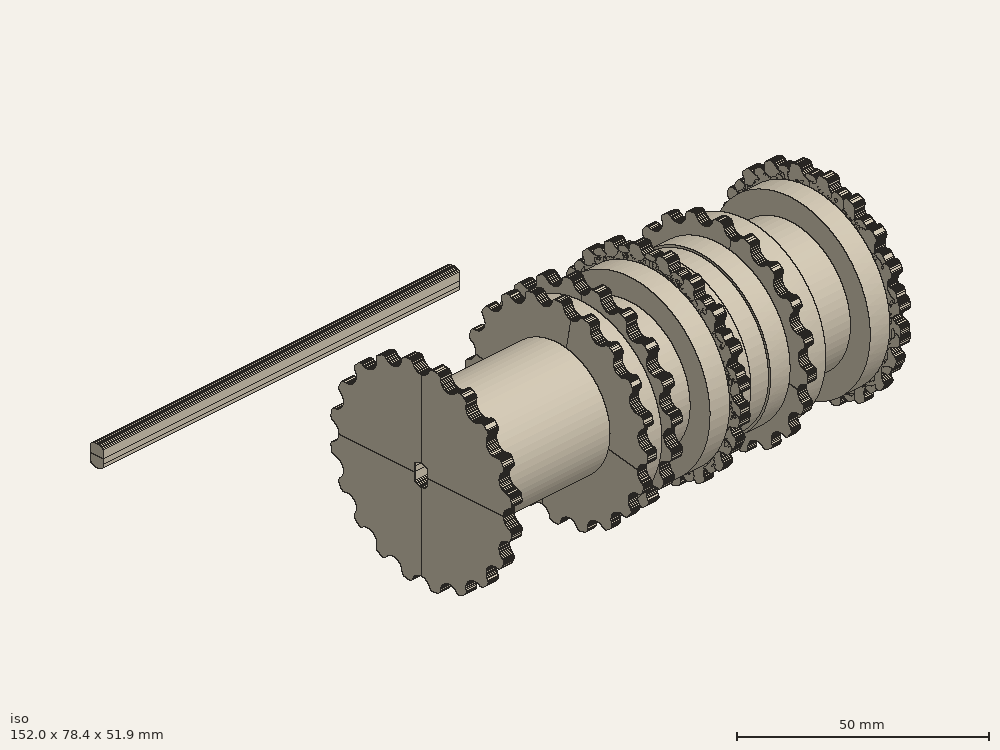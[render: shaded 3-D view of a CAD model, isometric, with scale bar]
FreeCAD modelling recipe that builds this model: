
FCSTD DOCUMENT  (FreeCAD 0.18R4 (GitTag))
Label: ведущий каток
License: All rights reserved
LicenseURL: http://en.wikipedia.org/wiki/All_rights_reserved
objects: Sketcher::SketchObject×33, PartDesign::Pad×23, PartDesign::PolarPattern×19, PartDesign::Body×15, Part::Cut×10, Part::Cylinder×8, Part::MultiFuse×6, App::MeasureDistance×4, PartDesign::Pocket×4, Mesh::Feature×3
note: 145 computed .brp shape members not serialized (recipe doc carries the construction recipe); baked Part::Feature solids carry a one-line shape summary decoded from their .brp

FEATURE [Mesh::Feature] vedushhee_koleso_WALL_E  label="vedushhee_koleso_WALL-E"
FEATURE [Sketcher::SketchObject] Sketch001
  MapMode = 5
  Placement = pos=(0,0,0) rot=(0.57735,0.57735,0.57735;2.0944rad)
  Support = -> [YZ_Plane001]
  sketch-geometry (20):
    g0: LineSegment StartX=1.84977 StartY=-2.03462 StartZ=0 EndX=1.64219 EndY=-2.20542 EndZ=0
    g1: LineSegment StartX=1.64219 StartY=-2.20542 StartZ=0 EndX=1.4178 EndY=-2.35642 EndZ=0
    g2: LineSegment StartX=1.4178 StartY=-2.35642 StartZ=0 EndX=1.1786 EndY=-2.48192 EndZ=0
    g3: LineSegment StartX=1.1786 StartY=-2.48192 StartZ=0 EndX=0.933165 EndY=-2.58946 EndZ=0
    g4: LineSegment StartX=0.933165 StartY=-2.58946 StartZ=0 EndX=0.669297 EndY=-2.66615 EndZ=0
    g5: LineSegment StartX=0.669297 StartY=-2.66615 StartZ=0 EndX=0.401357 EndY=-2.72007 EndZ=0
    g6: LineSegment StartX=0.401357 StartY=-2.72007 StartZ=0 EndX=0.133198 EndY=-2.74689 EndZ=0
    g7: LineSegment StartX=0.133198 StartY=-2.74689 StartZ=0 EndX=-0.13715 EndY=-2.74708 EndZ=0
    g8: LineSegment StartX=-0.13715 StartY=-2.74708 StartZ=0 EndX=-0.688499 EndY=-2.66151 EndZ=0
    g9: LineSegment StartX=-0.688499 StartY=-2.66151 StartZ=0 EndX=-0.94393 EndY=-2.58392 EndZ=0
    g10: LineSegment StartX=-0.94393 StartY=-2.58392 StartZ=0 EndX=-1.18786 EndY=-2.4818 EndZ=0
    g11: LineSegment StartX=-1.18786 StartY=-2.4818 StartZ=0 EndX=-1.42897 EndY=-2.34335 EndZ=0
    g12: LineSegment StartX=-1.42897 StartY=-2.34335 StartZ=0 EndX=-1.64859 EndY=-2.19653 EndZ=0
    g13: LineSegment StartX=-1.64859 StartY=-2.19653 StartZ=0 EndX=-1.84554 EndY=-2.0342 EndZ=0
    g14: LineSegment StartX=-1.84554 StartY=-2.0342 StartZ=0 EndX=-1.84465 EndY=-1.22163 EndZ=0
    g15: LineSegment StartX=-1.84465 StartY=-1.22163 StartZ=0 EndX=-1.84999 EndY=-0.000151 EndZ=0
    g16: LineSegment StartX=-1.84999 StartY=-0.000151 StartZ=0 EndX=-1.85002 EndY=0.00099 EndZ=0
    g17: LineSegment StartX=-1.85002 StartY=0.00099 StartZ=0 EndX=1.85015 EndY=0.005067 EndZ=0
    g18: LineSegment StartX=1.84931 StartY=-2.02283 StartZ=0 EndX=1.84977 EndY=-2.03462 EndZ=0
    g19: LineSegment StartX=1.85015 StartY=0.005067 StartZ=0 EndX=1.84931 EndY=-2.02283 EndZ=0
  constraints (20):
    c: Coincident(g0,g1)
    c: Coincident(g1,g2)
    c: Coincident(g2,g3)
    c: Coincident(g3,g4)
    c: Coincident(g4,g5)
    c: Coincident(g5,g6)
    c: Coincident(g8,g9)
    c: Coincident(g9,g10)
    c: Coincident(g10,g11)
    c: Coincident(g11,g12)
    c: Coincident(g12,g13)
    c: Coincident(g13,g14)
    c: Coincident(g14,g15)
    c: Coincident(g15,g16)
    c: Coincident(g16,g17)
    c: Coincident(g0,g18)
    c: Coincident(g7,g8)
    c: Coincident(g6,g7)
    c: Coincident(g18,g19)
    c: Coincident(g17,g19)
FEATURE [PartDesign::Pad] Pad001
  Length = 100
  Length2 = 100
  Midplane = true
  Placement = pos=(0,0,0) rot=(0.57735,0.57735,0.57735;2.0944rad)
  Profile = -> Sketch001
  Type = 0
FEATURE [PartDesign::PolarPattern] PolarPattern001
  Angle = 360
  Axis = -> Sketch001 [N_Axis]
  BaseFeature = -> Pad001
  Occurrences = 2
  Originals = -> [Pad001]
  Placement = pos=(0,0,0) rot=(0.57735,0.57735,0.57735;2.0944rad)
FEATURE [PartDesign::Body] Body001
  Group = -> [Sketch001,Pad001,PolarPattern001]
  Origin = -> Origin001
  Tip = -> PolarPattern001
FEATURE [Sketcher::SketchObject] Sketch002
  MapMode = 5
  Placement = pos=(0,0,0) rot=(0.57735,0.57735,0.57735;2.0944rad)
  Support = -> [YZ_Plane002]
  sketch-geometry (20):
    g0: LineSegment StartX=1.84977 StartY=-2.03462 StartZ=0 EndX=1.64219 EndY=-2.20542 EndZ=0
    g1: LineSegment StartX=1.64219 StartY=-2.20542 StartZ=0 EndX=1.4178 EndY=-2.35642 EndZ=0
    g2: LineSegment StartX=1.4178 StartY=-2.35642 StartZ=0 EndX=1.1786 EndY=-2.48192 EndZ=0
    g3: LineSegment StartX=1.1786 StartY=-2.48192 StartZ=0 EndX=0.933165 EndY=-2.58946 EndZ=0
    g4: LineSegment StartX=0.933165 StartY=-2.58946 StartZ=0 EndX=0.669297 EndY=-2.66615 EndZ=0
    g5: LineSegment StartX=0.669297 StartY=-2.66615 StartZ=0 EndX=0.401357 EndY=-2.72007 EndZ=0
    g6: LineSegment StartX=0.401357 StartY=-2.72007 StartZ=0 EndX=0.133198 EndY=-2.74689 EndZ=0
    g7: LineSegment StartX=0.133198 StartY=-2.74689 StartZ=0 EndX=-0.13715 EndY=-2.74708 EndZ=0
    g8: LineSegment StartX=-0.13715 StartY=-2.74708 StartZ=0 EndX=-0.688499 EndY=-2.66151 EndZ=0
    g9: LineSegment StartX=-0.688499 StartY=-2.66151 StartZ=0 EndX=-0.94393 EndY=-2.58392 EndZ=0
    g10: LineSegment StartX=-0.94393 StartY=-2.58392 StartZ=0 EndX=-1.18786 EndY=-2.4818 EndZ=0
    g11: LineSegment StartX=-1.18786 StartY=-2.4818 StartZ=0 EndX=-1.42897 EndY=-2.34335 EndZ=0
    g12: LineSegment StartX=-1.42897 StartY=-2.34335 StartZ=0 EndX=-1.64859 EndY=-2.19653 EndZ=0
    g13: LineSegment StartX=-1.64859 StartY=-2.19653 StartZ=0 EndX=-1.84554 EndY=-2.0342 EndZ=0
    g14: LineSegment StartX=-1.84554 StartY=-2.0342 StartZ=0 EndX=-1.84465 EndY=-1.22163 EndZ=0
    g15: LineSegment StartX=-1.84465 StartY=-1.22163 StartZ=0 EndX=-1.84999 EndY=-0.000151 EndZ=0
    g16: LineSegment StartX=-1.84999 StartY=-0.000151 StartZ=0 EndX=-1.85002 EndY=0.00099 EndZ=0
    g17: LineSegment StartX=-1.85002 StartY=0.00099 StartZ=0 EndX=1.85015 EndY=0.005067 EndZ=0
    g18: LineSegment StartX=1.84931 StartY=-2.02283 StartZ=0 EndX=1.84977 EndY=-2.03462 EndZ=0
    g19: LineSegment StartX=1.85015 StartY=0.005067 StartZ=0 EndX=1.84931 EndY=-2.02283 EndZ=0
  constraints (20):
    c: Coincident(g0,g1)
    c: Coincident(g1,g2)
    c: Coincident(g2,g3)
    c: Coincident(g3,g4)
    c: Coincident(g4,g5)
    c: Coincident(g5,g6)
    c: Coincident(g8,g9)
    c: Coincident(g9,g10)
    c: Coincident(g10,g11)
    c: Coincident(g11,g12)
    c: Coincident(g12,g13)
    c: Coincident(g13,g14)
    c: Coincident(g14,g15)
    c: Coincident(g15,g16)
    c: Coincident(g16,g17)
    c: Coincident(g0,g18)
    c: Coincident(g7,g8)
    c: Coincident(g6,g7)
    c: Coincident(g18,g19)
    c: Coincident(g17,g19)
FEATURE [PartDesign::Pad] Pad002
  Length = 100
  Length2 = 100
  Midplane = true
  Placement = pos=(0,0,0) rot=(0.57735,0.57735,0.57735;2.0944rad)
  Profile = -> Sketch002
  Type = 0
FEATURE [PartDesign::PolarPattern] PolarPattern002
  Angle = 360
  Axis = -> Sketch002 [N_Axis]
  BaseFeature = -> Pad002
  Occurrences = 2
  Originals = -> [Pad002]
  Placement = pos=(0,0,0) rot=(0.57735,0.57735,0.57735;2.0944rad)
FEATURE [PartDesign::Body] Body002
  Group = -> [Sketch002,Pad002,PolarPattern002]
  Origin = -> Origin002
  Placement = pos=(-47,0,1) rot=(0,0,1;0rad)
  Tip = -> PolarPattern002
FEATURE [Part::Cylinder] Cylinder  label="Цилиндр"
  Angle = 360
  AttacherType = Attacher::AttachEngine3D
  Height = 45
  Placement = pos=(0.123253,0,1.01304) rot=(0,-1,0;1.5708rad)
  Radius = 15
FEATURE [Sketcher::SketchObject] Sketch003
  MapMode = 5
  Placement = pos=(0,0,0) rot=(0.57735,0.57735,0.57735;2.0944rad)
  Support = -> [YZ_Plane003]
  sketch-geometry (211):
    g0: LineSegment StartX=0 StartY=0 StartZ=0 EndX=23.0775 EndY=-0.007725 EndZ=0
    g1: LineSegment StartX=23.0775 StartY=-0.007725 StartZ=0 EndX=23.0915 EndY=0.254478 EndZ=0
    g2: LineSegment StartX=23.0915 StartY=0.254478 StartZ=0 EndX=23.1284 EndY=0.508391 EndZ=0
    g3: LineSegment StartX=23.1284 StartY=0.508391 StartZ=0 EndX=23.1869 EndY=0.740712 EndZ=0
    g4: LineSegment StartX=23.1869 StartY=0.740712 StartZ=0 EndX=23.2782 EndY=0.973565 EndZ=0
    g5: LineSegment StartX=23.2782 StartY=0.973565 StartZ=0 EndX=23.3963 EndY=1.22031 EndZ=0
    g6: LineSegment StartX=23.3963 StartY=1.22031 StartZ=0 EndX=23.5215 EndY=1.42239 EndZ=0
    g7: LineSegment StartX=23.5215 StartY=1.42239 StartZ=0 EndX=23.6745 EndY=1.62203 EndZ=0
    g8: LineSegment StartX=23.6745 StartY=1.62203 StartZ=0 EndX=23.8622 EndY=1.81795 EndZ=0
    g9: LineSegment StartX=23.8622 StartY=1.81795 StartZ=0 EndX=24.0428 EndY=1.97182 EndZ=0
    g10: LineSegment StartX=24.0428 StartY=1.97182 StartZ=0 EndX=24.2535 EndY=2.11914 EndZ=0
    g11: LineSegment StartX=24.2535 StartY=2.11914 StartZ=0 EndX=24.4771 EndY=2.24429 EndZ=0
    g12: LineSegment StartX=24.4771 StartY=2.24429 StartZ=0 EndX=24.7643 EndY=2.36841 EndZ=0
    g13: LineSegment StartX=24.7643 StartY=2.36841 StartZ=0 EndX=24.8553 EndY=2.41105 EndZ=0
    g14: LineSegment StartX=24.8553 StartY=2.41105 StartZ=0 EndX=24.9955 EndY=2.50386 EndZ=0
    g15: LineSegment StartX=24.9955 StartY=2.50386 StartZ=0 EndX=25.1151 EndY=2.62736 EndZ=0
    g16: LineSegment StartX=25.1151 StartY=2.62736 StartZ=0 EndX=25.2142 EndY=2.76003 EndZ=0
    g17: LineSegment StartX=25.2142 StartY=2.76003 StartZ=0 EndX=25.2969 EndY=2.93426 EndZ=0
    g18: LineSegment StartX=25.2969 StartY=2.93426 StartZ=0 EndX=25.3426 EndY=3.08419 EndZ=0
    g19: LineSegment StartX=25.3426 StartY=3.08419 StartZ=0 EndX=25.3551 EndY=3.24413 EndZ=0
    g20: LineSegment StartX=25.3551 StartY=3.24413 StartZ=0 EndX=25.349 EndY=3.41794 EndZ=0
    g21: LineSegment StartX=25.349 StartY=3.41794 StartZ=0 EndX=25.3326 EndY=3.53796 EndZ=0
    g22: LineSegment StartX=25.3326 StartY=3.53796 StartZ=0 EndX=25.2546 EndY=4.05249 EndZ=0
    g23: LineSegment StartX=25.2546 StartY=4.05249 StartZ=0 EndX=25.1642 EndY=4.58451 EndZ=0
    g24: LineSegment StartX=25.1642 StartY=4.58451 StartZ=0 EndX=25.1211 EndY=4.74519 EndZ=0
    g25: LineSegment StartX=25.1211 StartY=4.74519 StartZ=0 EndX=25.0493 EndY=4.90009 EndZ=0
    g26: LineSegment StartX=25.0493 StartY=4.90009 StartZ=0 EndX=24.9559 EndY=5.03652 EndZ=0
    g27: LineSegment StartX=24.9559 StartY=5.03652 StartZ=0 EndX=24.8359 EndY=5.16166 EndZ=0
    g28: LineSegment StartX=24.8359 StartY=5.16166 StartZ=0 EndX=24.7064 EndY=5.26066 EndZ=0
    g29: LineSegment StartX=24.7064 StartY=5.26066 StartZ=0 EndX=24.5515 EndY=5.33657 EndZ=0
    g30: LineSegment StartX=24.5515 StartY=5.33657 StartZ=0 EndX=24.3854 EndY=5.38889 EndZ=0
    g31: LineSegment StartX=24.3854 StartY=5.38889 StartZ=0 EndX=23.9661 EndY=5.429 EndZ=0
    g32: LineSegment StartX=23.9661 StartY=5.429 StartZ=0 EndX=23.7168 EndY=5.47721 EndZ=0
    g33: LineSegment StartX=23.7168 StartY=5.47721 StartZ=0 EndX=23.4789 EndY=5.55004 EndZ=0
    g34: LineSegment StartX=23.4789 StartY=5.55004 StartZ=0 EndX=23.244 EndY=5.64749 EndZ=0
    g35: LineSegment StartX=23.244 StartY=5.64749 StartZ=0 EndX=23.0141 EndY=5.77459 EndZ=0
    g36: LineSegment StartX=23.0141 StartY=5.77459 StartZ=0 EndX=22.81 EndY=5.91307 EndZ=0
    g37: LineSegment StartX=22.81 StartY=5.91307 StartZ=0 EndX=22.6171 EndY=6.07925 EndZ=0
    g38: LineSegment StartX=22.6171 StartY=6.07925 StartZ=0 EndX=22.4499 EndY=6.25158 EndZ=0
    g39: LineSegment StartX=22.4499 StartY=6.25158 StartZ=0 EndX=22.2897 EndY=6.45644 EndZ=0
    g40: LineSegment StartX=22.2897 StartY=6.45644 StartZ=0 EndX=22.1484 EndY=6.67133 EndZ=0
    g41: LineSegment StartX=22.1484 StartY=6.67133 StartZ=0 EndX=22.0413 EndY=6.89628 EndZ=0
    g42: LineSegment StartX=22.0413 StartY=6.89628 StartZ=0 EndX=21.9449 EndY=7.13041 EndZ=0
    g43: LineSegment StartX=21.9449 StartY=7.13041 StartZ=0 EndX=21.883 EndY=7.36574 EndZ=0
    g44: LineSegment StartX=21.883 StartY=7.36574 StartZ=0 EndX=21.842 EndY=7.61808 EndZ=0
    g45: LineSegment StartX=21.842 StartY=7.61808 StartZ=0 EndX=21.8244 EndY=7.88752 EndZ=0
    g46: LineSegment StartX=21.8244 StartY=7.88752 StartZ=0 EndX=21.8388 EndY=8.12242 EndZ=0
    g47: LineSegment StartX=21.8388 StartY=8.12242 StartZ=0 EndX=21.8716 EndY=8.3765 EndZ=0
    g48: LineSegment StartX=21.8716 StartY=8.3765 StartZ=0 EndX=21.9322 EndY=8.62371 EndZ=0
    g49: LineSegment StartX=21.9322 StartY=8.62371 StartZ=0 EndX=22.0085 EndY=8.85622 EndZ=0
    g50: LineSegment StartX=22.0085 StartY=8.85622 StartZ=0 EndX=22.1095 EndY=9.0873 EndZ=0
    g51: LineSegment StartX=22.1095 StartY=9.0873 StartZ=0 EndX=22.2564 EndY=9.30001 EndZ=0
    g52: LineSegment StartX=22.2564 StartY=9.30001 StartZ=0 EndX=22.4222 EndY=9.51816 EndZ=0
    g53: LineSegment StartX=22.4222 StartY=9.51816 StartZ=0 EndX=22.5814 EndY=9.69568 EndZ=0
    g54: LineSegment StartX=22.5814 StartY=9.69568 StartZ=0 EndX=22.7773 EndY=9.86401 EndZ=0
    g55: LineSegment StartX=22.7773 StartY=9.86401 StartZ=0 EndX=22.8829 EndY=9.96654 EndZ=0
    g56: LineSegment StartX=22.8829 StartY=9.96654 StartZ=0 EndX=22.9946 EndY=10.1027 EndZ=0
    g57: LineSegment StartX=22.9946 StartY=10.1027 StartZ=0 EndX=23.0728 EndY=10.2473 EndZ=0
    g58: LineSegment StartX=23.0728 StartY=10.2473 StartZ=0 EndX=23.1295 EndY=10.4111 EndZ=0
    g59: LineSegment StartX=23.1295 StartY=10.4111 StartZ=0 EndX=23.1555 EndY=10.5871 EndZ=0
    g60: LineSegment StartX=23.1555 StartY=10.5871 StartZ=0 EndX=23.1416 EndY=10.7621 EndZ=0
    g61: LineSegment StartX=23.1416 StartY=10.7621 StartZ=0 EndX=23.1095 EndY=10.9289 EndZ=0
    g62: LineSegment StartX=23.1095 StartY=10.9289 StartZ=0 EndX=23.0483 EndY=11.0865 EndZ=0
    g63: LineSegment StartX=23.0483 StartY=11.0865 StartZ=0 EndX=22.8718 EndY=11.4442 EndZ=0
    g64: LineSegment StartX=22.8718 StartY=11.4442 StartZ=0 EndX=22.5688 EndY=12.0257 EndZ=0
    g65: LineSegment StartX=22.5688 StartY=12.0257 StartZ=0 EndX=22.5075 EndY=12.152 EndZ=0
    g66: LineSegment StartX=22.5075 StartY=12.152 StartZ=0 EndX=22.4248 EndY=12.279 EndZ=0
    g67: LineSegment StartX=22.4248 StartY=12.279 StartZ=0 EndX=22.3208 EndY=12.3999 EndZ=0
    g68: LineSegment StartX=22.3208 StartY=12.3999 StartZ=0 EndX=22.1769 EndY=12.5009 EndZ=0
    g69: LineSegment StartX=22.1769 StartY=12.5009 StartZ=0 EndX=22.0254 EndY=12.5805 EndZ=0
    g70: LineSegment StartX=22.0254 StartY=12.5805 StartZ=0 EndX=21.8678 EndY=12.6325 EndZ=0
    g71: LineSegment StartX=21.8678 StartY=12.6325 StartZ=0 EndX=21.6949 EndY=12.6601 EndZ=0
    g72: LineSegment StartX=21.6949 StartY=12.6601 StartZ=0 EndX=21.5327 EndY=12.6555 EndZ=0
    g73: LineSegment StartX=21.5327 StartY=12.6555 StartZ=0 EndX=21.1061 EndY=12.5612 EndZ=0
    g74: LineSegment StartX=21.1061 StartY=12.5612 StartZ=0 EndX=20.8582 EndY=12.5352 EndZ=0
    g75: LineSegment StartX=20.8582 StartY=12.5352 StartZ=0 EndX=20.6087 EndY=12.5337 EndZ=0
    g76: LineSegment StartX=20.6087 StartY=12.5337 StartZ=0 EndX=20.3501 EndY=12.5536 EndZ=0
    g77: LineSegment StartX=20.3501 StartY=12.5536 StartZ=0 EndX=20.0854 EndY=12.5979 EndZ=0
    g78: LineSegment StartX=20.0854 StartY=12.5979 StartZ=0 EndX=19.8665 EndY=12.6699 EndZ=0
    g79: LineSegment StartX=19.8665 StartY=12.6699 StartZ=0 EndX=19.614 EndY=12.7678 EndZ=0
    g80: LineSegment StartX=19.614 StartY=12.7678 StartZ=0 EndX=19.4105 EndY=12.881 EndZ=0
    g81: LineSegment StartX=19.4105 StartY=12.881 StartZ=0 EndX=19.1993 EndY=13.0264 EndZ=0
    g82: LineSegment StartX=19.1993 StartY=13.0264 StartZ=0 EndX=18.9927 EndY=13.2018 EndZ=0
    g83: LineSegment StartX=18.9927 StartY=13.2018 StartZ=0 EndX=18.8259 EndY=13.3625 EndZ=0
    g84: LineSegment StartX=18.8259 StartY=13.3625 StartZ=0 EndX=18.6714 EndY=13.5553 EndZ=0
    g85: LineSegment StartX=18.6714 StartY=13.5553 StartZ=0 EndX=18.5367 EndY=13.768 EndZ=0
    g86: LineSegment StartX=18.5367 StartY=13.768 StartZ=0 EndX=18.4051 EndY=14.0083 EndZ=0
    g87: LineSegment StartX=18.4051 StartY=14.0083 StartZ=0 EndX=18.3225 EndY=14.2255 EndZ=0
    g88: LineSegment StartX=18.3225 StartY=14.2255 StartZ=0 EndX=18.2506 EndY=14.4903 EndZ=0
    g89: LineSegment StartX=18.2506 StartY=14.4903 StartZ=0 EndX=18.2154 EndY=14.7183 EndZ=0
    g90: LineSegment StartX=18.2154 StartY=14.7183 StartZ=0 EndX=18.2017 EndY=14.9876 EndZ=0
    g91: LineSegment StartX=18.2017 StartY=14.9876 StartZ=0 EndX=18.1828 EndY=15.2236 EndZ=0
    g92: LineSegment StartX=18.1828 StartY=15.2236 StartZ=0 EndX=18.2304 EndY=15.4722 EndZ=0
    g93: LineSegment StartX=18.2304 StartY=15.4722 StartZ=0 EndX=18.2815 EndY=15.714 EndZ=0
    g94: LineSegment StartX=18.2815 StartY=15.714 StartZ=0 EndX=18.3735 EndY=15.9865 EndZ=0
    g95: LineSegment StartX=18.3735 StartY=15.9865 StartZ=0 EndX=18.4796 EndY=16.216 EndZ=0
    g96: LineSegment StartX=18.4796 StartY=16.216 StartZ=0 EndX=18.6771 EndY=16.5429 EndZ=0
    g97: LineSegment StartX=18.6771 StartY=16.5429 StartZ=0 EndX=18.7452 EndY=16.7132 EndZ=0
    g98: LineSegment StartX=18.7452 StartY=16.7132 StartZ=0 EndX=18.7725 EndY=16.8562 EndZ=0
    g99: LineSegment StartX=18.7725 StartY=16.8562 StartZ=0 EndX=18.7793 EndY=17.0538 EndZ=0
    g100: LineSegment StartX=18.7793 StartY=17.0538 StartZ=0 EndX=18.7515 EndY=17.1989 EndZ=0
    g101: LineSegment StartX=18.7515 StartY=17.1989 StartZ=0 EndX=18.7073 EndY=17.3454 EndZ=0
    g102: LineSegment StartX=18.7073 StartY=17.3454 StartZ=0 EndX=18.6221 EndY=17.4986 EndZ=0
    g103: LineSegment StartX=18.6221 StartY=17.4986 StartZ=0 EndX=18.5404 EndY=17.6076 EndZ=0
    g104: LineSegment StartX=18.5404 StartY=17.6076 StartZ=0 EndX=18.4484 EndY=17.7132 EndZ=0
    g105: LineSegment StartX=18.4484 StartY=17.7132 StartZ=0 EndX=17.7843 EndY=18.3841 EndZ=0
    g106: LineSegment StartX=17.7843 StartY=18.3841 StartZ=0 EndX=17.6004 EndY=18.5476 EndZ=0
    g107: LineSegment StartX=17.6004 StartY=18.5476 StartZ=0 EndX=17.5187 EndY=18.6089 EndZ=0
    g108: LineSegment StartX=17.5187 StartY=18.6089 StartZ=0 EndX=17.3654 EndY=18.6872 EndZ=0
    g109: LineSegment StartX=17.3654 StartY=18.6872 StartZ=0 EndX=17.2156 EndY=18.7383 EndZ=0
    g110: LineSegment StartX=17.2156 StartY=18.7383 StartZ=0 EndX=17.0487 EndY=18.7621 EndZ=0
    g111: LineSegment StartX=17.0487 StartY=18.7621 StartZ=0 EndX=16.8852 EndY=18.7724 EndZ=0
    g112: LineSegment StartX=16.8852 StartY=18.7724 StartZ=0 EndX=16.7183 EndY=18.7417 EndZ=0
    g113: LineSegment StartX=16.7183 StartY=18.7417 StartZ=0 EndX=16.5651 EndY=18.694 EndZ=0
    g114: LineSegment StartX=16.5651 StartY=18.694 StartZ=0 EndX=16.3709 EndY=18.5851 EndZ=0
    g115: LineSegment StartX=16.3709 StartY=18.5851 StartZ=0 EndX=16.1496 EndY=18.4522 EndZ=0
    g116: LineSegment StartX=16.1496 StartY=18.4522 StartZ=0 EndX=15.9752 EndY=18.3739 EndZ=0
    g117: LineSegment StartX=15.9752 StartY=18.3739 StartZ=0 EndX=15.7423 EndY=18.2963 EndZ=0
    g118: LineSegment StartX=15.7423 StartY=18.2963 StartZ=0 EndX=15.5003 EndY=18.2233 EndZ=0
    g119: LineSegment StartX=15.5003 StartY=18.2233 StartZ=0 EndX=15.2492 EndY=18.1982 EndZ=0
    g120: LineSegment StartX=15.2492 StartY=18.1982 StartZ=0 EndX=14.973 EndY=18.2004 EndZ=0
    g121: LineSegment StartX=14.973 StartY=18.2004 StartZ=0 EndX=14.7241 EndY=18.2141 EndZ=0
    g122: LineSegment StartX=14.7241 StartY=18.2141 StartZ=0 EndX=14.4685 EndY=18.2484 EndZ=0
    g123: LineSegment StartX=14.4685 StartY=18.2484 StartZ=0 EndX=14.2265 EndY=18.3192 EndZ=0
    g124: LineSegment StartX=14.2265 StartY=18.3192 StartZ=0 EndX=13.9799 EndY=18.4196 EndZ=0
    g125: LineSegment StartX=13.9799 StartY=18.4196 StartZ=0 EndX=13.7736 EndY=18.5304 EndZ=0
    g126: LineSegment StartX=13.7736 StartY=18.5304 StartZ=0 EndX=13.5557 EndY=18.6666 EndZ=0
    g127: LineSegment StartX=13.5557 StartY=18.6666 StartZ=0 EndX=13.3683 EndY=18.8267 EndZ=0
    g128: LineSegment StartX=13.3683 StartY=18.8267 StartZ=0 EndX=13.1844 EndY=18.997 EndZ=0
    g129: LineSegment StartX=13.1844 StartY=18.997 StartZ=0 EndX=13.0175 EndY=19.2047 EndZ=0
    g130: LineSegment StartX=13.0175 StartY=19.2047 StartZ=0 EndX=12.9086 EndY=19.4227 EndZ=0
    g131: LineSegment StartX=12.9086 StartY=19.4227 StartZ=0 EndX=12.694 EndY=19.8518 EndZ=0
    g132: LineSegment StartX=12.694 StartY=19.8518 StartZ=0 EndX=12.5986 EndY=20.1266 EndZ=0
    g133: LineSegment StartX=12.5986 StartY=20.1266 StartZ=0 EndX=12.5373 EndY=20.3616 EndZ=0
    g134: LineSegment StartX=12.5373 StartY=20.3616 StartZ=0 EndX=12.5305 EndY=20.6613 EndZ=0
    g135: LineSegment StartX=12.5305 StartY=20.6613 StartZ=0 EndX=12.527 EndY=20.852 EndZ=0
    g136: LineSegment StartX=12.527 StartY=20.852 StartZ=0 EndX=12.5713 EndY=21.1177 EndZ=0
    g137: LineSegment StartX=12.5713 StartY=21.1177 StartZ=0 EndX=12.6565 EndY=21.5025 EndZ=0
    g138: LineSegment StartX=12.6565 StartY=21.5025 StartZ=0 EndX=12.6531 EndY=21.7205 EndZ=0
    g139: LineSegment StartX=12.6531 StartY=21.7205 StartZ=0 EndX=12.6258 EndY=21.8771 EndZ=0
    g140: LineSegment StartX=12.6258 StartY=21.8771 StartZ=0 EndX=12.5747 EndY=22.0542 EndZ=0
    g141: LineSegment StartX=12.5747 StartY=22.0542 StartZ=0 EndX=12.5027 EndY=22.1813 EndZ=0
    g142: LineSegment StartX=12.5027 StartY=22.1813 StartZ=0 EndX=12.3937 EndY=22.3278 EndZ=0
    g143: LineSegment StartX=12.3937 StartY=22.3278 StartZ=0 EndX=12.278 EndY=22.4299 EndZ=0
    g144: LineSegment StartX=12.278 StartY=22.4299 StartZ=0 EndX=12.1179 EndY=22.5287 EndZ=0
    g145: LineSegment StartX=12.1179 StartY=22.5287 StartZ=0 EndX=11.7535 EndY=22.716 EndZ=0
    g146: LineSegment StartX=11.7535 StartY=22.716 StartZ=0 EndX=11.2792 EndY=22.9552 EndZ=0
    g147: LineSegment StartX=11.2792 StartY=22.9552 StartZ=0 EndX=11.0374 EndY=23.0607 EndZ=0
    g148: LineSegment StartX=11.0374 StartY=23.0607 StartZ=0 EndX=10.8875 EndY=23.1289 EndZ=0
    g149: LineSegment StartX=10.8875 StartY=23.1289 StartZ=0 EndX=10.7036 EndY=23.1527 EndZ=0
    g150: LineSegment StartX=10.7036 StartY=23.1527 StartZ=0 EndX=10.5571 EndY=23.1391 EndZ=0
    g151: LineSegment StartX=10.5571 StartY=23.1391 StartZ=0 EndX=10.38 EndY=23.1084 EndZ=0
    g152: LineSegment StartX=10.38 StartY=23.1084 StartZ=0 EndX=10.2643 EndY=23.0641 EndZ=0
    g153: LineSegment StartX=10.2643 StartY=23.0641 StartZ=0 EndX=10.1042 EndY=22.9892 EndZ=0
    g154: LineSegment StartX=10.1042 StartY=22.9892 StartZ=0 EndX=9.97817 EndY=22.9041 EndZ=0
    g155: LineSegment StartX=9.97817 StartY=22.9041 StartZ=0 EndX=9.8181 EndY=22.727 EndZ=0
    g156: LineSegment StartX=9.8181 StartY=22.727 StartZ=0 EndX=9.68528 EndY=22.5839 EndZ=0
    g157: LineSegment StartX=9.68528 StartY=22.5839 StartZ=0 EndX=9.5184 EndY=22.4068 EndZ=0
    g158: LineSegment StartX=9.5184 StartY=22.4068 StartZ=0 EndX=9.29702 EndY=22.2672 EndZ=0
    g159: LineSegment StartX=9.29702 StartY=22.2672 StartZ=0 EndX=9.09042 EndY=22.1273 EndZ=0
    g160: LineSegment StartX=9.09042 StartY=22.1273 StartZ=0 EndX=8.85883 EndY=22.0183 EndZ=0
    g161: LineSegment StartX=8.85883 StartY=22.0183 StartZ=0 EndX=8.60681 EndY=21.9332 EndZ=0
    g162: LineSegment StartX=8.60681 StartY=21.9332 StartZ=0 EndX=8.36841 EndY=21.8719 EndZ=0
    g163: LineSegment StartX=8.36841 StartY=21.8719 StartZ=0 EndX=8.11979 EndY=21.8344 EndZ=0
    g164: LineSegment StartX=8.11979 StartY=21.8344 StartZ=0 EndX=7.84392 EndY=21.8242 EndZ=0
    g165: LineSegment StartX=7.84392 StartY=21.8242 StartZ=0 EndX=7.61915 EndY=21.8446 EndZ=0
    g166: LineSegment StartX=7.61915 StartY=21.8446 StartZ=0 EndX=7.39096 EndY=21.8753 EndZ=0
    g167: LineSegment StartX=7.39096 StartY=21.8753 StartZ=0 EndX=7.10488 EndY=21.9536 EndZ=0
    g168: LineSegment StartX=7.10488 StartY=21.9536 StartZ=0 EndX=6.8801 EndY=22.0387 EndZ=0
    g169: LineSegment StartX=6.8801 StartY=22.0387 StartZ=0 EndX=6.66554 EndY=22.1613 EndZ=0
    g170: LineSegment StartX=6.66554 StartY=22.1613 StartZ=0 EndX=6.44417 EndY=22.2908 EndZ=0
    g171: LineSegment StartX=6.44417 StartY=22.2908 StartZ=0 EndX=6.19215 EndY=22.5087 EndZ=0
    g172: LineSegment StartX=6.19215 StartY=22.5087 StartZ=0 EndX=6.02186 EndY=22.6688 EndZ=0
    g173: LineSegment StartX=6.02186 StartY=22.6688 StartZ=0 EndX=5.87882 EndY=22.8391 EndZ=0
    g174: LineSegment StartX=5.87882 StartY=22.8391 StartZ=0 EndX=5.74259 EndY=23.0809 EndZ=0
    g175: LineSegment StartX=5.74259 StartY=23.0809 StartZ=0 EndX=5.62679 EndY=23.2989 EndZ=0
    g176: LineSegment StartX=5.62679 StartY=23.2989 StartZ=0 EndX=5.54923 EndY=23.4812 EndZ=0
    g177: LineSegment StartX=5.54923 StartY=23.4812 StartZ=0 EndX=5.48987 EndY=23.7141 EndZ=0
    g178: LineSegment StartX=5.48987 StartY=23.7141 StartZ=0 EndX=5.43965 EndY=23.931 EndZ=0
    g179: LineSegment StartX=5.43965 StartY=23.931 StartZ=0 EndX=5.38283 EndY=24.3702 EndZ=0
    g180: LineSegment StartX=5.38283 StartY=24.3702 StartZ=0 EndX=5.34402 EndY=24.5505 EndZ=0
    g181: LineSegment StartX=5.34402 StartY=24.5505 StartZ=0 EndX=5.26412 EndY=24.7012 EndZ=0
    g182: LineSegment StartX=5.26412 StartY=24.7012 StartZ=0 EndX=5.15662 EndY=24.8433 EndZ=0
    g183: LineSegment StartX=5.15662 StartY=24.8433 StartZ=0 EndX=5.03563 EndY=24.9643 EndZ=0
    g184: LineSegment StartX=5.03563 StartY=24.9643 StartZ=0 EndX=4.9055 EndY=25.0534 EndZ=0
    g185: LineSegment StartX=4.9055 StartY=25.0534 StartZ=0 EndX=4.76168 EndY=25.115 EndZ=0
    g186: LineSegment StartX=4.76168 StartY=25.115 StartZ=0 EndX=4.56991 EndY=25.1698 EndZ=0
    g187: LineSegment StartX=4.56991 StartY=25.1698 StartZ=0 EndX=4.22291 EndY=25.2269 EndZ=0
    g188: LineSegment StartX=4.22291 StartY=25.2269 StartZ=0 EndX=3.72501 EndY=25.306 EndZ=0
    g189: LineSegment StartX=3.72501 StartY=25.306 StartZ=0 EndX=3.40823 EndY=25.3504 EndZ=0
    g190: LineSegment StartX=3.40823 StartY=25.3504 StartZ=0 EndX=3.25674 EndY=25.3565 EndZ=0
    g191: LineSegment StartX=3.25674 StartY=25.3565 StartZ=0 EndX=3.08534 EndY=25.3351 EndZ=0
    g192: LineSegment StartX=3.08534 StartY=25.3351 StartZ=0 EndX=2.91854 EndY=25.2876 EndZ=0
    g193: LineSegment StartX=2.91854 StartY=25.2876 StartZ=0 EndX=2.76092 EndY=25.2111 EndZ=0
    g194: LineSegment StartX=2.76092 StartY=25.2111 StartZ=0 EndX=2.62472 EndY=25.1116 EndZ=0
    g195: LineSegment StartX=2.62472 StartY=25.1116 StartZ=0 EndX=2.50842 EndY=24.9984 EndZ=0
    g196: LineSegment StartX=2.50842 StartY=24.9984 StartZ=0 EndX=2.41174 EndY=24.8483 EndZ=0
    g197: LineSegment StartX=2.41174 StartY=24.8483 StartZ=0 EndX=2.30308 EndY=24.582 EndZ=0
    g198: LineSegment StartX=2.30308 StartY=24.582 StartZ=0 EndX=2.25622 EndY=24.4788 EndZ=0
    g199: LineSegment StartX=2.25622 StartY=24.4788 StartZ=0 EndX=2.13227 EndY=24.2646 EndZ=0
    g200: LineSegment StartX=2.13227 StartY=24.2646 StartZ=0 EndX=1.96394 EndY=24.0365 EndZ=0
    g201: LineSegment StartX=1.96394 StartY=24.0365 StartZ=0 EndX=1.80479 EndY=23.856 EndZ=0
    g202: LineSegment StartX=1.80479 StartY=23.856 StartZ=0 EndX=1.62573 EndY=23.6797 EndZ=0
    g203: LineSegment StartX=1.62573 StartY=23.6797 StartZ=0 EndX=1.41955 EndY=23.5197 EndZ=0
    g204: LineSegment StartX=1.41955 StartY=23.5197 StartZ=0 EndX=1.20904 EndY=23.3867 EndZ=0
    g205: LineSegment StartX=1.20904 StartY=23.3867 StartZ=0 EndX=0.984393 EndY=23.2759 EndZ=0
    g206: LineSegment StartX=0.984393 StartY=23.2759 StartZ=0 EndX=0.742307 EndY=23.1856 EndZ=0
    g207: LineSegment StartX=0.742307 StartY=23.1856 StartZ=0 EndX=0.498622 EndY=23.1238 EndZ=0
    g208: LineSegment StartX=0.498622 StartY=23.1238 StartZ=0 EndX=0.250381 EndY=23.0889 EndZ=0
    g209: LineSegment StartX=0.250381 StartY=23.0889 StartZ=0 EndX=-0.006065 EndY=23.0756 EndZ=0
    g210: LineSegment StartX=-0.006065 StartY=23.0756 StartZ=0 EndX=0 EndY=0 EndZ=0
  constraints (212):
    c: Coincident(g0,g1)
    c: Coincident(g1,g2)
    c: Coincident(g2,g3)
    c: Coincident(g3,g4)
    c: Coincident(g4,g5)
    c: Coincident(g5,g6)
    c: Coincident(g6,g7)
    c: Coincident(g7,g8)
    c: Coincident(g8,g9)
    c: Coincident(g9,g10)
    c: Coincident(g10,g11)
    c: Coincident(g11,g12)
    c: Coincident(g12,g13)
    c: Coincident(g13,g14)
    c: Coincident(g14,g15)
    c: Coincident(g15,g16)
    c: Coincident(g16,g17)
    c: Coincident(g17,g18)
    c: Coincident(g18,g19)
    c: Coincident(g19,g20)
    c: Coincident(g20,g21)
    c: Coincident(g21,g22)
    c: Coincident(g22,g23)
    c: Coincident(g23,g24)
    c: Coincident(g24,g25)
    c: Coincident(g25,g26)
    c: Coincident(g26,g27)
    c: Coincident(g27,g28)
    c: Coincident(g28,g29)
    c: Coincident(g29,g30)
    c: Coincident(g30,g31)
    c: Coincident(g31,g32)
    c: Coincident(g32,g33)
    c: Coincident(g33,g34)
    c: Coincident(g34,g35)
    c: Coincident(g35,g36)
    c: Coincident(g36,g37)
    c: Coincident(g37,g38)
    c: Coincident(g38,g39)
    c: Coincident(g39,g40)
    c: Coincident(g40,g41)
    c: Coincident(g41,g42)
    c: Coincident(g42,g43)
    c: Coincident(g43,g44)
    c: Coincident(g44,g45)
    c: Coincident(g45,g46)
    c: Coincident(g46,g47)
    c: Coincident(g47,g48)
    c: Coincident(g48,g49)
    c: Coincident(g49,g50)
    c: Coincident(g50,g51)
    c: Coincident(g51,g52)
    c: Coincident(g52,g53)
    c: Coincident(g53,g54)
    c: Coincident(g54,g55)
    c: Coincident(g55,g56)
    c: Coincident(g56,g57)
    c: Coincident(g57,g58)
    c: Coincident(g58,g59)
    c: Coincident(g59,g60)
    c: Coincident(g60,g61)
    c: Coincident(g61,g62)
    c: Coincident(g62,g63)
    c: Coincident(g63,g64)
    c: Coincident(g64,g65)
    c: Coincident(g65,g66)
    c: Coincident(g66,g67)
    c: Coincident(g67,g68)
    c: Coincident(g68,g69)
    c: Coincident(g69,g70)
    c: Coincident(g70,g71)
    c: Coincident(g71,g72)
    c: Coincident(g72,g73)
    c: Coincident(g73,g74)
    c: Coincident(g74,g75)
    c: Coincident(g75,g76)
    c: Coincident(g76,g77)
    c: Coincident(g77,g78)
    c: Coincident(g78,g79)
    c: Coincident(g79,g80)
    c: Coincident(g80,g81)
    c: Coincident(g81,g82)
    c: Coincident(g82,g83)
    c: Coincident(g83,g84)
    c: Coincident(g84,g85)
    c: Coincident(g85,g86)
    c: Coincident(g86,g87)
    c: Coincident(g87,g88)
    c: Coincident(g88,g89)
    c: Coincident(g89,g90)
    c: Coincident(g90,g91)
    c: Coincident(g91,g92)
    c: Coincident(g92,g93)
    c: Coincident(g93,g94)
    c: Coincident(g94,g95)
    c: Coincident(g95,g96)
    c: Coincident(g96,g97)
    c: Coincident(g97,g98)
    c: Coincident(g98,g99)
    c: Coincident(g99,g100)
    c: Coincident(g100,g101)
    c: Coincident(g101,g102)
    c: Coincident(g102,g103)
    c: Coincident(g103,g104)
    c: Coincident(g104,g105)
    c: Coincident(g105,g106)
    c: Coincident(g106,g107)
    c: Coincident(g107,g108)
    c: Coincident(g108,g109)
    c: Coincident(g109,g110)
    c: Coincident(g110,g111)
    c: Coincident(g111,g112)
    c: Coincident(g112,g113)
    c: Coincident(g113,g114)
    c: Coincident(g114,g115)
    c: Coincident(g115,g116)
    c: Coincident(g116,g117)
    c: Coincident(g117,g118)
    c: Coincident(g118,g119)
    c: Coincident(g119,g120)
    c: Coincident(g120,g121)
    c: Coincident(g121,g122)
    c: Coincident(g122,g123)
    c: Coincident(g123,g124)
    c: Coincident(g124,g125)
    c: Coincident(g125,g126)
    c: Coincident(g126,g127)
    c: Coincident(g127,g128)
    c: Coincident(g128,g129)
    c: Coincident(g129,g130)
    c: Coincident(g130,g131)
    c: Coincident(g131,g132)
    c: Coincident(g132,g133)
    c: Coincident(g133,g134)
    c: Coincident(g134,g135)
    c: Coincident(g135,g136)
    c: Coincident(g136,g137)
    c: Coincident(g137,g138)
    c: Coincident(g138,g139)
    c: Coincident(g139,g140)
    c: Coincident(g140,g141)
    c: Coincident(g141,g142)
    c: Coincident(g142,g143)
    c: Coincident(g143,g144)
    c: Coincident(g144,g145)
    c: Coincident(g145,g146)
    c: Coincident(g146,g147)
    c: Coincident(g147,g148)
    c: Coincident(g148,g149)
    c: Coincident(g149,g150)
    c: Coincident(g150,g151)
    c: Coincident(g151,g152)
    c: Coincident(g152,g153)
    c: Coincident(g153,g154)
    c: Coincident(g154,g155)
    c: Coincident(g155,g156)
    c: Coincident(g156,g157)
    c: Coincident(g157,g158)
    c: Coincident(g158,g159)
    c: Coincident(g159,g160)
    c: Coincident(g160,g161)
    c: Coincident(g161,g162)
    c: Coincident(g162,g163)
    c: Coincident(g163,g164)
    c: Coincident(g164,g165)
    c: Coincident(g165,g166)
    c: Coincident(g166,g167)
    c: Coincident(g167,g168)
    c: Coincident(g168,g169)
    c: Coincident(g169,g170)
    c: Coincident(g170,g171)
    c: Coincident(g171,g172)
    c: Coincident(g172,g173)
    c: Coincident(g173,g174)
    c: Coincident(g174,g175)
    c: Coincident(g175,g176)
    c: Coincident(g176,g177)
    c: Coincident(g177,g178)
    c: Coincident(g178,g179)
    c: Coincident(g179,g180)
    c: Coincident(g180,g181)
    c: Coincident(g181,g182)
    c: Coincident(g182,g183)
    c: Coincident(g183,g184)
    c: Coincident(g184,g185)
    c: Coincident(g185,g186)
    c: Coincident(g186,g187)
    c: Coincident(g187,g188)
    c: Coincident(g188,g189)
    c: Coincident(g189,g190)
    c: Coincident(g190,g191)
    c: Coincident(g191,g192)
    c: Coincident(g192,g193)
    c: Coincident(g193,g194)
    c: Coincident(g194,g195)
    c: Coincident(g195,g196)
    c: Coincident(g196,g197)
    c: Coincident(g197,g198)
    c: Coincident(g198,g199)
    c: Coincident(g199,g200)
    c: Coincident(g200,g201)
    c: Coincident(g201,g202)
    c: Coincident(g202,g203)
    c: Coincident(g203,g204)
    c: Coincident(g204,g205)
    c: Coincident(g205,g206)
    c: Coincident(g206,g207)
    c: Coincident(g207,g208)
    c: Coincident(g208,g209)
    c: Coincident(g0,g210)
    c: Coincident(g0,g-1)
    c: Coincident(g209,g210)
FEATURE [PartDesign::Pad] Pad004
  Length = 3
  Length2 = 100
  Placement = pos=(0,0,0) rot=(0.57735,0.57735,0.57735;2.0944rad)
  Profile = -> Sketch003
  Type = 0
FEATURE [Sketcher::SketchObject] Sketch004
  MapMode = 5
  Placement = pos=(0,0,0) rot=(0.57735,0.57735,0.57735;2.0944rad)
  Support = -> [YZ_Plane004]
  sketch-geometry (20):
    g0: LineSegment StartX=1.84977 StartY=-2.03462 StartZ=0 EndX=1.64219 EndY=-2.20542 EndZ=0
    g1: LineSegment StartX=1.64219 StartY=-2.20542 StartZ=0 EndX=1.4178 EndY=-2.35642 EndZ=0
    g2: LineSegment StartX=1.4178 StartY=-2.35642 StartZ=0 EndX=1.1786 EndY=-2.48192 EndZ=0
    g3: LineSegment StartX=1.1786 StartY=-2.48192 StartZ=0 EndX=0.933165 EndY=-2.58946 EndZ=0
    g4: LineSegment StartX=0.933165 StartY=-2.58946 StartZ=0 EndX=0.669297 EndY=-2.66615 EndZ=0
    g5: LineSegment StartX=0.669297 StartY=-2.66615 StartZ=0 EndX=0.401357 EndY=-2.72007 EndZ=0
    g6: LineSegment StartX=0.401357 StartY=-2.72007 StartZ=0 EndX=0.133198 EndY=-2.74689 EndZ=0
    g7: LineSegment StartX=0.133198 StartY=-2.74689 StartZ=0 EndX=-0.13715 EndY=-2.74708 EndZ=0
    g8: LineSegment StartX=-0.13715 StartY=-2.74708 StartZ=0 EndX=-0.688499 EndY=-2.66151 EndZ=0
    g9: LineSegment StartX=-0.688499 StartY=-2.66151 StartZ=0 EndX=-0.94393 EndY=-2.58392 EndZ=0
    g10: LineSegment StartX=-0.94393 StartY=-2.58392 StartZ=0 EndX=-1.18786 EndY=-2.4818 EndZ=0
    g11: LineSegment StartX=-1.18786 StartY=-2.4818 StartZ=0 EndX=-1.42897 EndY=-2.34335 EndZ=0
    g12: LineSegment StartX=-1.42897 StartY=-2.34335 StartZ=0 EndX=-1.64859 EndY=-2.19653 EndZ=0
    g13: LineSegment StartX=-1.64859 StartY=-2.19653 StartZ=0 EndX=-1.84554 EndY=-2.0342 EndZ=0
    g14: LineSegment StartX=-1.84554 StartY=-2.0342 StartZ=0 EndX=-1.84465 EndY=-1.22163 EndZ=0
    g15: LineSegment StartX=-1.84465 StartY=-1.22163 StartZ=0 EndX=-1.84999 EndY=-0.000151 EndZ=0
    g16: LineSegment StartX=-1.84999 StartY=-0.000151 StartZ=0 EndX=-1.85002 EndY=0.00099 EndZ=0
    g17: LineSegment StartX=-1.85002 StartY=0.00099 StartZ=0 EndX=1.85015 EndY=0.005067 EndZ=0
    g18: LineSegment StartX=1.84931 StartY=-2.02283 StartZ=0 EndX=1.84977 EndY=-2.03462 EndZ=0
    g19: LineSegment StartX=1.85015 StartY=0.005067 StartZ=0 EndX=1.84931 EndY=-2.02283 EndZ=0
  constraints (20):
    c: Coincident(g0,g1)
    c: Coincident(g1,g2)
    c: Coincident(g2,g3)
    c: Coincident(g3,g4)
    c: Coincident(g4,g5)
    c: Coincident(g5,g6)
    c: Coincident(g8,g9)
    c: Coincident(g9,g10)
    c: Coincident(g10,g11)
    c: Coincident(g11,g12)
    c: Coincident(g12,g13)
    c: Coincident(g13,g14)
    c: Coincident(g14,g15)
    c: Coincident(g15,g16)
    c: Coincident(g16,g17)
    c: Coincident(g0,g18)
    c: Coincident(g7,g8)
    c: Coincident(g6,g7)
    c: Coincident(g18,g19)
    c: Coincident(g17,g19)
FEATURE [PartDesign::Pad] Pad003
  Length = 100
  Length2 = 100
  Midplane = true
  Placement = pos=(0,0,0) rot=(0.57735,0.57735,0.57735;2.0944rad)
  Profile = -> Sketch004
  Type = 0
FEATURE [PartDesign::PolarPattern] PolarPattern003
  Angle = 360
  Axis = -> Sketch004 [N_Axis]
  BaseFeature = -> Pad003
  Occurrences = 2
  Originals = -> [Pad003]
  Placement = pos=(0,0,0) rot=(0.57735,0.57735,0.57735;2.0944rad)
FEATURE [PartDesign::Body] Body003
  Group = -> [Sketch004,Pad003,PolarPattern003]
  Origin = -> Origin003
  Tip = -> PolarPattern003
FEATURE [PartDesign::PolarPattern] PolarPattern004
  Angle = 360
  Axis = -> Sketch003 [N_Axis]
  BaseFeature = -> Pad004
  Occurrences = 4
  Originals = -> [Pad004]
  Placement = pos=(0,0,0) rot=(0.57735,0.57735,0.57735;2.0944rad)
FEATURE [PartDesign::Body] Body004
  Group = -> [Sketch003,Pad004,PolarPattern004]
  Origin = -> Origin004
  Tip = -> PolarPattern004
FEATURE [Part::Cut] Cut001
  Base = -> Body004
  Placement = pos=(-45,0,1) rot=(0,0,1;0rad)
  Tool = -> Body003
FEATURE [App::MeasureDistance] Distance  label="Distance: 45,00 mm"
  Distance = 45.0011
  P1 = (-42,-17.3454,19.7073)
  P2 = (3,-17.6076,19.5404)
FEATURE [Part::Cylinder] Cylinder001  label="Цилиндр001"
  Angle = 360
  AttacherType = Attacher::AttachEngine3D
  Height = 45
  Placement = pos=(0.123253,0,1.01304) rot=(0,-1,0;1.5708rad)
  Radius = 15
FEATURE [Sketcher::SketchObject] Sketch005
  MapMode = 5
  Placement = pos=(0,0,0) rot=(0.57735,0.57735,0.57735;2.0944rad)
  Support = -> [YZ_Plane007]
  sketch-geometry (211):
    g0: LineSegment StartX=0 StartY=0 StartZ=0 EndX=23.0775 EndY=-0.007725 EndZ=0
    g1: LineSegment StartX=23.0775 StartY=-0.007725 StartZ=0 EndX=23.0915 EndY=0.254478 EndZ=0
    g2: LineSegment StartX=23.0915 StartY=0.254478 StartZ=0 EndX=23.1284 EndY=0.508391 EndZ=0
    g3: LineSegment StartX=23.1284 StartY=0.508391 StartZ=0 EndX=23.1869 EndY=0.740712 EndZ=0
    g4: LineSegment StartX=23.1869 StartY=0.740712 StartZ=0 EndX=23.2782 EndY=0.973565 EndZ=0
    g5: LineSegment StartX=23.2782 StartY=0.973565 StartZ=0 EndX=23.3963 EndY=1.22031 EndZ=0
    g6: LineSegment StartX=23.3963 StartY=1.22031 StartZ=0 EndX=23.5215 EndY=1.42239 EndZ=0
    g7: LineSegment StartX=23.5215 StartY=1.42239 StartZ=0 EndX=23.6745 EndY=1.62203 EndZ=0
    g8: LineSegment StartX=23.6745 StartY=1.62203 StartZ=0 EndX=23.8622 EndY=1.81795 EndZ=0
    g9: LineSegment StartX=23.8622 StartY=1.81795 StartZ=0 EndX=24.0428 EndY=1.97182 EndZ=0
    g10: LineSegment StartX=24.0428 StartY=1.97182 StartZ=0 EndX=24.2535 EndY=2.11914 EndZ=0
    g11: LineSegment StartX=24.2535 StartY=2.11914 StartZ=0 EndX=24.4771 EndY=2.24429 EndZ=0
    g12: LineSegment StartX=24.4771 StartY=2.24429 StartZ=0 EndX=24.7643 EndY=2.36841 EndZ=0
    g13: LineSegment StartX=24.7643 StartY=2.36841 StartZ=0 EndX=24.8553 EndY=2.41105 EndZ=0
    g14: LineSegment StartX=24.8553 StartY=2.41105 StartZ=0 EndX=24.9955 EndY=2.50386 EndZ=0
    g15: LineSegment StartX=24.9955 StartY=2.50386 StartZ=0 EndX=25.1151 EndY=2.62736 EndZ=0
    g16: LineSegment StartX=25.1151 StartY=2.62736 StartZ=0 EndX=25.2142 EndY=2.76003 EndZ=0
    g17: LineSegment StartX=25.2142 StartY=2.76003 StartZ=0 EndX=25.2969 EndY=2.93426 EndZ=0
    g18: LineSegment StartX=25.2969 StartY=2.93426 StartZ=0 EndX=25.3426 EndY=3.08419 EndZ=0
    g19: LineSegment StartX=25.3426 StartY=3.08419 StartZ=0 EndX=25.3551 EndY=3.24413 EndZ=0
    g20: LineSegment StartX=25.3551 StartY=3.24413 StartZ=0 EndX=25.349 EndY=3.41794 EndZ=0
    g21: LineSegment StartX=25.349 StartY=3.41794 StartZ=0 EndX=25.3326 EndY=3.53796 EndZ=0
    g22: LineSegment StartX=25.3326 StartY=3.53796 StartZ=0 EndX=25.2546 EndY=4.05249 EndZ=0
    g23: LineSegment StartX=25.2546 StartY=4.05249 StartZ=0 EndX=25.1642 EndY=4.58451 EndZ=0
    g24: LineSegment StartX=25.1642 StartY=4.58451 StartZ=0 EndX=25.1211 EndY=4.74519 EndZ=0
    g25: LineSegment StartX=25.1211 StartY=4.74519 StartZ=0 EndX=25.0493 EndY=4.90009 EndZ=0
    g26: LineSegment StartX=25.0493 StartY=4.90009 StartZ=0 EndX=24.9559 EndY=5.03652 EndZ=0
    g27: LineSegment StartX=24.9559 StartY=5.03652 StartZ=0 EndX=24.8359 EndY=5.16166 EndZ=0
    g28: LineSegment StartX=24.8359 StartY=5.16166 StartZ=0 EndX=24.7064 EndY=5.26066 EndZ=0
    g29: LineSegment StartX=24.7064 StartY=5.26066 StartZ=0 EndX=24.5515 EndY=5.33657 EndZ=0
    g30: LineSegment StartX=24.5515 StartY=5.33657 StartZ=0 EndX=24.3854 EndY=5.38889 EndZ=0
    g31: LineSegment StartX=24.3854 StartY=5.38889 StartZ=0 EndX=23.9661 EndY=5.429 EndZ=0
    g32: LineSegment StartX=23.9661 StartY=5.429 StartZ=0 EndX=23.7168 EndY=5.47721 EndZ=0
    g33: LineSegment StartX=23.7168 StartY=5.47721 StartZ=0 EndX=23.4789 EndY=5.55004 EndZ=0
    g34: LineSegment StartX=23.4789 StartY=5.55004 StartZ=0 EndX=23.244 EndY=5.64749 EndZ=0
    g35: LineSegment StartX=23.244 StartY=5.64749 StartZ=0 EndX=23.0141 EndY=5.77459 EndZ=0
    g36: LineSegment StartX=23.0141 StartY=5.77459 StartZ=0 EndX=22.81 EndY=5.91307 EndZ=0
    g37: LineSegment StartX=22.81 StartY=5.91307 StartZ=0 EndX=22.6171 EndY=6.07925 EndZ=0
    g38: LineSegment StartX=22.6171 StartY=6.07925 StartZ=0 EndX=22.4499 EndY=6.25158 EndZ=0
    g39: LineSegment StartX=22.4499 StartY=6.25158 StartZ=0 EndX=22.2897 EndY=6.45644 EndZ=0
    g40: LineSegment StartX=22.2897 StartY=6.45644 StartZ=0 EndX=22.1484 EndY=6.67133 EndZ=0
    g41: LineSegment StartX=22.1484 StartY=6.67133 StartZ=0 EndX=22.0413 EndY=6.89628 EndZ=0
    g42: LineSegment StartX=22.0413 StartY=6.89628 StartZ=0 EndX=21.9449 EndY=7.13041 EndZ=0
    g43: LineSegment StartX=21.9449 StartY=7.13041 StartZ=0 EndX=21.883 EndY=7.36574 EndZ=0
    g44: LineSegment StartX=21.883 StartY=7.36574 StartZ=0 EndX=21.842 EndY=7.61808 EndZ=0
    g45: LineSegment StartX=21.842 StartY=7.61808 StartZ=0 EndX=21.8244 EndY=7.88752 EndZ=0
    g46: LineSegment StartX=21.8244 StartY=7.88752 StartZ=0 EndX=21.8388 EndY=8.12242 EndZ=0
    g47: LineSegment StartX=21.8388 StartY=8.12242 StartZ=0 EndX=21.8716 EndY=8.3765 EndZ=0
    g48: LineSegment StartX=21.8716 StartY=8.3765 StartZ=0 EndX=21.9322 EndY=8.62371 EndZ=0
    g49: LineSegment StartX=21.9322 StartY=8.62371 StartZ=0 EndX=22.0085 EndY=8.85622 EndZ=0
    g50: LineSegment StartX=22.0085 StartY=8.85622 StartZ=0 EndX=22.1095 EndY=9.0873 EndZ=0
    g51: LineSegment StartX=22.1095 StartY=9.0873 StartZ=0 EndX=22.2564 EndY=9.30001 EndZ=0
    g52: LineSegment StartX=22.2564 StartY=9.30001 StartZ=0 EndX=22.4222 EndY=9.51816 EndZ=0
    g53: LineSegment StartX=22.4222 StartY=9.51816 StartZ=0 EndX=22.5814 EndY=9.69568 EndZ=0
    g54: LineSegment StartX=22.5814 StartY=9.69568 StartZ=0 EndX=22.7773 EndY=9.86401 EndZ=0
    g55: LineSegment StartX=22.7773 StartY=9.86401 StartZ=0 EndX=22.8829 EndY=9.96654 EndZ=0
    g56: LineSegment StartX=22.8829 StartY=9.96654 StartZ=0 EndX=22.9946 EndY=10.1027 EndZ=0
    g57: LineSegment StartX=22.9946 StartY=10.1027 StartZ=0 EndX=23.0728 EndY=10.2473 EndZ=0
    g58: LineSegment StartX=23.0728 StartY=10.2473 StartZ=0 EndX=23.1295 EndY=10.4111 EndZ=0
    g59: LineSegment StartX=23.1295 StartY=10.4111 StartZ=0 EndX=23.1555 EndY=10.5871 EndZ=0
    g60: LineSegment StartX=23.1555 StartY=10.5871 StartZ=0 EndX=23.1416 EndY=10.7621 EndZ=0
    g61: LineSegment StartX=23.1416 StartY=10.7621 StartZ=0 EndX=23.1095 EndY=10.9289 EndZ=0
    g62: LineSegment StartX=23.1095 StartY=10.9289 StartZ=0 EndX=23.0483 EndY=11.0865 EndZ=0
    g63: LineSegment StartX=23.0483 StartY=11.0865 StartZ=0 EndX=22.8718 EndY=11.4442 EndZ=0
    g64: LineSegment StartX=22.8718 StartY=11.4442 StartZ=0 EndX=22.5688 EndY=12.0257 EndZ=0
    g65: LineSegment StartX=22.5688 StartY=12.0257 StartZ=0 EndX=22.5075 EndY=12.152 EndZ=0
    g66: LineSegment StartX=22.5075 StartY=12.152 StartZ=0 EndX=22.4248 EndY=12.279 EndZ=0
    g67: LineSegment StartX=22.4248 StartY=12.279 StartZ=0 EndX=22.3208 EndY=12.3999 EndZ=0
    g68: LineSegment StartX=22.3208 StartY=12.3999 StartZ=0 EndX=22.1769 EndY=12.5009 EndZ=0
    g69: LineSegment StartX=22.1769 StartY=12.5009 StartZ=0 EndX=22.0254 EndY=12.5805 EndZ=0
    g70: LineSegment StartX=22.0254 StartY=12.5805 StartZ=0 EndX=21.8678 EndY=12.6325 EndZ=0
    g71: LineSegment StartX=21.8678 StartY=12.6325 StartZ=0 EndX=21.6949 EndY=12.6601 EndZ=0
    g72: LineSegment StartX=21.6949 StartY=12.6601 StartZ=0 EndX=21.5327 EndY=12.6555 EndZ=0
    g73: LineSegment StartX=21.5327 StartY=12.6555 StartZ=0 EndX=21.1061 EndY=12.5612 EndZ=0
    g74: LineSegment StartX=21.1061 StartY=12.5612 StartZ=0 EndX=20.8582 EndY=12.5352 EndZ=0
    g75: LineSegment StartX=20.8582 StartY=12.5352 StartZ=0 EndX=20.6087 EndY=12.5337 EndZ=0
    g76: LineSegment StartX=20.6087 StartY=12.5337 StartZ=0 EndX=20.3501 EndY=12.5536 EndZ=0
    g77: LineSegment StartX=20.3501 StartY=12.5536 StartZ=0 EndX=20.0854 EndY=12.5979 EndZ=0
    g78: LineSegment StartX=20.0854 StartY=12.5979 StartZ=0 EndX=19.8665 EndY=12.6699 EndZ=0
    g79: LineSegment StartX=19.8665 StartY=12.6699 StartZ=0 EndX=19.614 EndY=12.7678 EndZ=0
    g80: LineSegment StartX=19.614 StartY=12.7678 StartZ=0 EndX=19.4105 EndY=12.881 EndZ=0
    g81: LineSegment StartX=19.4105 StartY=12.881 StartZ=0 EndX=19.1993 EndY=13.0264 EndZ=0
    g82: LineSegment StartX=19.1993 StartY=13.0264 StartZ=0 EndX=18.9927 EndY=13.2018 EndZ=0
    g83: LineSegment StartX=18.9927 StartY=13.2018 StartZ=0 EndX=18.8259 EndY=13.3625 EndZ=0
    g84: LineSegment StartX=18.8259 StartY=13.3625 StartZ=0 EndX=18.6714 EndY=13.5553 EndZ=0
    g85: LineSegment StartX=18.6714 StartY=13.5553 StartZ=0 EndX=18.5367 EndY=13.768 EndZ=0
    g86: LineSegment StartX=18.5367 StartY=13.768 StartZ=0 EndX=18.4051 EndY=14.0083 EndZ=0
    g87: LineSegment StartX=18.4051 StartY=14.0083 StartZ=0 EndX=18.3225 EndY=14.2255 EndZ=0
    g88: LineSegment StartX=18.3225 StartY=14.2255 StartZ=0 EndX=18.2506 EndY=14.4903 EndZ=0
    g89: LineSegment StartX=18.2506 StartY=14.4903 StartZ=0 EndX=18.2154 EndY=14.7183 EndZ=0
    g90: LineSegment StartX=18.2154 StartY=14.7183 StartZ=0 EndX=18.2017 EndY=14.9876 EndZ=0
    g91: LineSegment StartX=18.2017 StartY=14.9876 StartZ=0 EndX=18.1828 EndY=15.2236 EndZ=0
    g92: LineSegment StartX=18.1828 StartY=15.2236 StartZ=0 EndX=18.2304 EndY=15.4722 EndZ=0
    g93: LineSegment StartX=18.2304 StartY=15.4722 StartZ=0 EndX=18.2815 EndY=15.714 EndZ=0
    g94: LineSegment StartX=18.2815 StartY=15.714 StartZ=0 EndX=18.3735 EndY=15.9865 EndZ=0
    g95: LineSegment StartX=18.3735 StartY=15.9865 StartZ=0 EndX=18.4796 EndY=16.216 EndZ=0
    g96: LineSegment StartX=18.4796 StartY=16.216 StartZ=0 EndX=18.6771 EndY=16.5429 EndZ=0
    g97: LineSegment StartX=18.6771 StartY=16.5429 StartZ=0 EndX=18.7452 EndY=16.7132 EndZ=0
    g98: LineSegment StartX=18.7452 StartY=16.7132 StartZ=0 EndX=18.7725 EndY=16.8562 EndZ=0
    g99: LineSegment StartX=18.7725 StartY=16.8562 StartZ=0 EndX=18.7793 EndY=17.0538 EndZ=0
    g100: LineSegment StartX=18.7793 StartY=17.0538 StartZ=0 EndX=18.7515 EndY=17.1989 EndZ=0
    g101: LineSegment StartX=18.7515 StartY=17.1989 StartZ=0 EndX=18.7073 EndY=17.3454 EndZ=0
    g102: LineSegment StartX=18.7073 StartY=17.3454 StartZ=0 EndX=18.6221 EndY=17.4986 EndZ=0
    g103: LineSegment StartX=18.6221 StartY=17.4986 StartZ=0 EndX=18.5404 EndY=17.6076 EndZ=0
    g104: LineSegment StartX=18.5404 StartY=17.6076 StartZ=0 EndX=18.4484 EndY=17.7132 EndZ=0
    g105: LineSegment StartX=18.4484 StartY=17.7132 StartZ=0 EndX=17.7843 EndY=18.3841 EndZ=0
    g106: LineSegment StartX=17.7843 StartY=18.3841 StartZ=0 EndX=17.6004 EndY=18.5476 EndZ=0
    g107: LineSegment StartX=17.6004 StartY=18.5476 StartZ=0 EndX=17.5187 EndY=18.6089 EndZ=0
    g108: LineSegment StartX=17.5187 StartY=18.6089 StartZ=0 EndX=17.3654 EndY=18.6872 EndZ=0
    g109: LineSegment StartX=17.3654 StartY=18.6872 StartZ=0 EndX=17.2156 EndY=18.7383 EndZ=0
    g110: LineSegment StartX=17.2156 StartY=18.7383 StartZ=0 EndX=17.0487 EndY=18.7621 EndZ=0
    g111: LineSegment StartX=17.0487 StartY=18.7621 StartZ=0 EndX=16.8852 EndY=18.7724 EndZ=0
    g112: LineSegment StartX=16.8852 StartY=18.7724 StartZ=0 EndX=16.7183 EndY=18.7417 EndZ=0
    g113: LineSegment StartX=16.7183 StartY=18.7417 StartZ=0 EndX=16.5651 EndY=18.694 EndZ=0
    g114: LineSegment StartX=16.5651 StartY=18.694 StartZ=0 EndX=16.3709 EndY=18.5851 EndZ=0
    g115: LineSegment StartX=16.3709 StartY=18.5851 StartZ=0 EndX=16.1496 EndY=18.4522 EndZ=0
    g116: LineSegment StartX=16.1496 StartY=18.4522 StartZ=0 EndX=15.9752 EndY=18.3739 EndZ=0
    g117: LineSegment StartX=15.9752 StartY=18.3739 StartZ=0 EndX=15.7423 EndY=18.2963 EndZ=0
    g118: LineSegment StartX=15.7423 StartY=18.2963 StartZ=0 EndX=15.5003 EndY=18.2233 EndZ=0
    g119: LineSegment StartX=15.5003 StartY=18.2233 StartZ=0 EndX=15.2492 EndY=18.1982 EndZ=0
    g120: LineSegment StartX=15.2492 StartY=18.1982 StartZ=0 EndX=14.973 EndY=18.2004 EndZ=0
    g121: LineSegment StartX=14.973 StartY=18.2004 StartZ=0 EndX=14.7241 EndY=18.2141 EndZ=0
    g122: LineSegment StartX=14.7241 StartY=18.2141 StartZ=0 EndX=14.4685 EndY=18.2484 EndZ=0
    g123: LineSegment StartX=14.4685 StartY=18.2484 StartZ=0 EndX=14.2265 EndY=18.3192 EndZ=0
    g124: LineSegment StartX=14.2265 StartY=18.3192 StartZ=0 EndX=13.9799 EndY=18.4196 EndZ=0
    g125: LineSegment StartX=13.9799 StartY=18.4196 StartZ=0 EndX=13.7736 EndY=18.5304 EndZ=0
    g126: LineSegment StartX=13.7736 StartY=18.5304 StartZ=0 EndX=13.5557 EndY=18.6666 EndZ=0
    g127: LineSegment StartX=13.5557 StartY=18.6666 StartZ=0 EndX=13.3683 EndY=18.8267 EndZ=0
    g128: LineSegment StartX=13.3683 StartY=18.8267 StartZ=0 EndX=13.1844 EndY=18.997 EndZ=0
    g129: LineSegment StartX=13.1844 StartY=18.997 StartZ=0 EndX=13.0175 EndY=19.2047 EndZ=0
    g130: LineSegment StartX=13.0175 StartY=19.2047 StartZ=0 EndX=12.9086 EndY=19.4227 EndZ=0
    g131: LineSegment StartX=12.9086 StartY=19.4227 StartZ=0 EndX=12.694 EndY=19.8518 EndZ=0
    g132: LineSegment StartX=12.694 StartY=19.8518 StartZ=0 EndX=12.5986 EndY=20.1266 EndZ=0
    g133: LineSegment StartX=12.5986 StartY=20.1266 StartZ=0 EndX=12.5373 EndY=20.3616 EndZ=0
    g134: LineSegment StartX=12.5373 StartY=20.3616 StartZ=0 EndX=12.5305 EndY=20.6613 EndZ=0
    g135: LineSegment StartX=12.5305 StartY=20.6613 StartZ=0 EndX=12.527 EndY=20.852 EndZ=0
    g136: LineSegment StartX=12.527 StartY=20.852 StartZ=0 EndX=12.5713 EndY=21.1177 EndZ=0
    g137: LineSegment StartX=12.5713 StartY=21.1177 StartZ=0 EndX=12.6565 EndY=21.5025 EndZ=0
    g138: LineSegment StartX=12.6565 StartY=21.5025 StartZ=0 EndX=12.6531 EndY=21.7205 EndZ=0
    g139: LineSegment StartX=12.6531 StartY=21.7205 StartZ=0 EndX=12.6258 EndY=21.8771 EndZ=0
    g140: LineSegment StartX=12.6258 StartY=21.8771 StartZ=0 EndX=12.5747 EndY=22.0542 EndZ=0
    g141: LineSegment StartX=12.5747 StartY=22.0542 StartZ=0 EndX=12.5027 EndY=22.1813 EndZ=0
    g142: LineSegment StartX=12.5027 StartY=22.1813 StartZ=0 EndX=12.3937 EndY=22.3278 EndZ=0
    g143: LineSegment StartX=12.3937 StartY=22.3278 StartZ=0 EndX=12.278 EndY=22.4299 EndZ=0
    g144: LineSegment StartX=12.278 StartY=22.4299 StartZ=0 EndX=12.1179 EndY=22.5287 EndZ=0
    g145: LineSegment StartX=12.1179 StartY=22.5287 StartZ=0 EndX=11.7535 EndY=22.716 EndZ=0
    g146: LineSegment StartX=11.7535 StartY=22.716 StartZ=0 EndX=11.2792 EndY=22.9552 EndZ=0
    g147: LineSegment StartX=11.2792 StartY=22.9552 StartZ=0 EndX=11.0374 EndY=23.0607 EndZ=0
    g148: LineSegment StartX=11.0374 StartY=23.0607 StartZ=0 EndX=10.8875 EndY=23.1289 EndZ=0
    g149: LineSegment StartX=10.8875 StartY=23.1289 StartZ=0 EndX=10.7036 EndY=23.1527 EndZ=0
    g150: LineSegment StartX=10.7036 StartY=23.1527 StartZ=0 EndX=10.5571 EndY=23.1391 EndZ=0
    g151: LineSegment StartX=10.5571 StartY=23.1391 StartZ=0 EndX=10.38 EndY=23.1084 EndZ=0
    g152: LineSegment StartX=10.38 StartY=23.1084 StartZ=0 EndX=10.2643 EndY=23.0641 EndZ=0
    g153: LineSegment StartX=10.2643 StartY=23.0641 StartZ=0 EndX=10.1042 EndY=22.9892 EndZ=0
    g154: LineSegment StartX=10.1042 StartY=22.9892 StartZ=0 EndX=9.97817 EndY=22.9041 EndZ=0
    g155: LineSegment StartX=9.97817 StartY=22.9041 StartZ=0 EndX=9.8181 EndY=22.727 EndZ=0
    g156: LineSegment StartX=9.8181 StartY=22.727 StartZ=0 EndX=9.68528 EndY=22.5839 EndZ=0
    g157: LineSegment StartX=9.68528 StartY=22.5839 StartZ=0 EndX=9.5184 EndY=22.4068 EndZ=0
    g158: LineSegment StartX=9.5184 StartY=22.4068 StartZ=0 EndX=9.29702 EndY=22.2672 EndZ=0
    g159: LineSegment StartX=9.29702 StartY=22.2672 StartZ=0 EndX=9.09042 EndY=22.1273 EndZ=0
    g160: LineSegment StartX=9.09042 StartY=22.1273 StartZ=0 EndX=8.85883 EndY=22.0183 EndZ=0
    g161: LineSegment StartX=8.85883 StartY=22.0183 StartZ=0 EndX=8.60681 EndY=21.9332 EndZ=0
    g162: LineSegment StartX=8.60681 StartY=21.9332 StartZ=0 EndX=8.36841 EndY=21.8719 EndZ=0
    g163: LineSegment StartX=8.36841 StartY=21.8719 StartZ=0 EndX=8.11979 EndY=21.8344 EndZ=0
    g164: LineSegment StartX=8.11979 StartY=21.8344 StartZ=0 EndX=7.84392 EndY=21.8242 EndZ=0
    g165: LineSegment StartX=7.84392 StartY=21.8242 StartZ=0 EndX=7.61915 EndY=21.8446 EndZ=0
    g166: LineSegment StartX=7.61915 StartY=21.8446 StartZ=0 EndX=7.39096 EndY=21.8753 EndZ=0
    g167: LineSegment StartX=7.39096 StartY=21.8753 StartZ=0 EndX=7.10488 EndY=21.9536 EndZ=0
    g168: LineSegment StartX=7.10488 StartY=21.9536 StartZ=0 EndX=6.8801 EndY=22.0387 EndZ=0
    g169: LineSegment StartX=6.8801 StartY=22.0387 StartZ=0 EndX=6.66554 EndY=22.1613 EndZ=0
    g170: LineSegment StartX=6.66554 StartY=22.1613 StartZ=0 EndX=6.44417 EndY=22.2908 EndZ=0
    g171: LineSegment StartX=6.44417 StartY=22.2908 StartZ=0 EndX=6.19215 EndY=22.5087 EndZ=0
    g172: LineSegment StartX=6.19215 StartY=22.5087 StartZ=0 EndX=6.02186 EndY=22.6688 EndZ=0
    g173: LineSegment StartX=6.02186 StartY=22.6688 StartZ=0 EndX=5.87882 EndY=22.8391 EndZ=0
    g174: LineSegment StartX=5.87882 StartY=22.8391 StartZ=0 EndX=5.74259 EndY=23.0809 EndZ=0
    g175: LineSegment StartX=5.74259 StartY=23.0809 StartZ=0 EndX=5.62679 EndY=23.2989 EndZ=0
    g176: LineSegment StartX=5.62679 StartY=23.2989 StartZ=0 EndX=5.54923 EndY=23.4812 EndZ=0
    g177: LineSegment StartX=5.54923 StartY=23.4812 StartZ=0 EndX=5.48987 EndY=23.7141 EndZ=0
    g178: LineSegment StartX=5.48987 StartY=23.7141 StartZ=0 EndX=5.43965 EndY=23.931 EndZ=0
    g179: LineSegment StartX=5.43965 StartY=23.931 StartZ=0 EndX=5.38283 EndY=24.3702 EndZ=0
    g180: LineSegment StartX=5.38283 StartY=24.3702 StartZ=0 EndX=5.34402 EndY=24.5505 EndZ=0
    g181: LineSegment StartX=5.34402 StartY=24.5505 StartZ=0 EndX=5.26412 EndY=24.7012 EndZ=0
    g182: LineSegment StartX=5.26412 StartY=24.7012 StartZ=0 EndX=5.15662 EndY=24.8433 EndZ=0
    g183: LineSegment StartX=5.15662 StartY=24.8433 StartZ=0 EndX=5.03563 EndY=24.9643 EndZ=0
    g184: LineSegment StartX=5.03563 StartY=24.9643 StartZ=0 EndX=4.9055 EndY=25.0534 EndZ=0
    g185: LineSegment StartX=4.9055 StartY=25.0534 StartZ=0 EndX=4.76168 EndY=25.115 EndZ=0
    g186: LineSegment StartX=4.76168 StartY=25.115 StartZ=0 EndX=4.56991 EndY=25.1698 EndZ=0
    g187: LineSegment StartX=4.56991 StartY=25.1698 StartZ=0 EndX=4.22291 EndY=25.2269 EndZ=0
    g188: LineSegment StartX=4.22291 StartY=25.2269 StartZ=0 EndX=3.72501 EndY=25.306 EndZ=0
    g189: LineSegment StartX=3.72501 StartY=25.306 StartZ=0 EndX=3.40823 EndY=25.3504 EndZ=0
    g190: LineSegment StartX=3.40823 StartY=25.3504 StartZ=0 EndX=3.25674 EndY=25.3565 EndZ=0
    g191: LineSegment StartX=3.25674 StartY=25.3565 StartZ=0 EndX=3.08534 EndY=25.3351 EndZ=0
    g192: LineSegment StartX=3.08534 StartY=25.3351 StartZ=0 EndX=2.91854 EndY=25.2876 EndZ=0
    g193: LineSegment StartX=2.91854 StartY=25.2876 StartZ=0 EndX=2.76092 EndY=25.2111 EndZ=0
    g194: LineSegment StartX=2.76092 StartY=25.2111 StartZ=0 EndX=2.62472 EndY=25.1116 EndZ=0
    g195: LineSegment StartX=2.62472 StartY=25.1116 StartZ=0 EndX=2.50842 EndY=24.9984 EndZ=0
    g196: LineSegment StartX=2.50842 StartY=24.9984 StartZ=0 EndX=2.41174 EndY=24.8483 EndZ=0
    g197: LineSegment StartX=2.41174 StartY=24.8483 StartZ=0 EndX=2.30308 EndY=24.582 EndZ=0
    g198: LineSegment StartX=2.30308 StartY=24.582 StartZ=0 EndX=2.25622 EndY=24.4788 EndZ=0
    g199: LineSegment StartX=2.25622 StartY=24.4788 StartZ=0 EndX=2.13227 EndY=24.2646 EndZ=0
    g200: LineSegment StartX=2.13227 StartY=24.2646 StartZ=0 EndX=1.96394 EndY=24.0365 EndZ=0
    g201: LineSegment StartX=1.96394 StartY=24.0365 StartZ=0 EndX=1.80479 EndY=23.856 EndZ=0
    g202: LineSegment StartX=1.80479 StartY=23.856 StartZ=0 EndX=1.62573 EndY=23.6797 EndZ=0
    g203: LineSegment StartX=1.62573 StartY=23.6797 StartZ=0 EndX=1.41955 EndY=23.5197 EndZ=0
    g204: LineSegment StartX=1.41955 StartY=23.5197 StartZ=0 EndX=1.20904 EndY=23.3867 EndZ=0
    g205: LineSegment StartX=1.20904 StartY=23.3867 StartZ=0 EndX=0.984393 EndY=23.2759 EndZ=0
    g206: LineSegment StartX=0.984393 StartY=23.2759 StartZ=0 EndX=0.742307 EndY=23.1856 EndZ=0
    g207: LineSegment StartX=0.742307 StartY=23.1856 StartZ=0 EndX=0.498622 EndY=23.1238 EndZ=0
    g208: LineSegment StartX=0.498622 StartY=23.1238 StartZ=0 EndX=0.250381 EndY=23.0889 EndZ=0
    g209: LineSegment StartX=0.250381 StartY=23.0889 StartZ=0 EndX=-0.006065 EndY=23.0756 EndZ=0
    g210: LineSegment StartX=-0.006065 StartY=23.0756 StartZ=0 EndX=0 EndY=0 EndZ=0
  constraints (212):
    c: Coincident(g0,g1)
    c: Coincident(g1,g2)
    c: Coincident(g2,g3)
    c: Coincident(g3,g4)
    c: Coincident(g4,g5)
    c: Coincident(g5,g6)
    c: Coincident(g6,g7)
    c: Coincident(g7,g8)
    c: Coincident(g8,g9)
    c: Coincident(g9,g10)
    c: Coincident(g10,g11)
    c: Coincident(g11,g12)
    c: Coincident(g12,g13)
    c: Coincident(g13,g14)
    c: Coincident(g14,g15)
    c: Coincident(g15,g16)
    c: Coincident(g16,g17)
    c: Coincident(g17,g18)
    c: Coincident(g18,g19)
    c: Coincident(g19,g20)
    c: Coincident(g20,g21)
    c: Coincident(g21,g22)
    c: Coincident(g22,g23)
    c: Coincident(g23,g24)
    c: Coincident(g24,g25)
    c: Coincident(g25,g26)
    c: Coincident(g26,g27)
    c: Coincident(g27,g28)
    c: Coincident(g28,g29)
    c: Coincident(g29,g30)
    c: Coincident(g30,g31)
    c: Coincident(g31,g32)
    c: Coincident(g32,g33)
    c: Coincident(g33,g34)
    c: Coincident(g34,g35)
    c: Coincident(g35,g36)
    c: Coincident(g36,g37)
    c: Coincident(g37,g38)
    c: Coincident(g38,g39)
    c: Coincident(g39,g40)
    c: Coincident(g40,g41)
    c: Coincident(g41,g42)
    c: Coincident(g42,g43)
    c: Coincident(g43,g44)
    c: Coincident(g44,g45)
    c: Coincident(g45,g46)
    c: Coincident(g46,g47)
    c: Coincident(g47,g48)
    c: Coincident(g48,g49)
    c: Coincident(g49,g50)
    c: Coincident(g50,g51)
    c: Coincident(g51,g52)
    c: Coincident(g52,g53)
    c: Coincident(g53,g54)
    c: Coincident(g54,g55)
    c: Coincident(g55,g56)
    c: Coincident(g56,g57)
    c: Coincident(g57,g58)
    c: Coincident(g58,g59)
    c: Coincident(g59,g60)
    c: Coincident(g60,g61)
    c: Coincident(g61,g62)
    c: Coincident(g62,g63)
    c: Coincident(g63,g64)
    c: Coincident(g64,g65)
    c: Coincident(g65,g66)
    c: Coincident(g66,g67)
    c: Coincident(g67,g68)
    c: Coincident(g68,g69)
    c: Coincident(g69,g70)
    c: Coincident(g70,g71)
    c: Coincident(g71,g72)
    c: Coincident(g72,g73)
    c: Coincident(g73,g74)
    c: Coincident(g74,g75)
    c: Coincident(g75,g76)
    c: Coincident(g76,g77)
    c: Coincident(g77,g78)
    c: Coincident(g78,g79)
    c: Coincident(g79,g80)
    c: Coincident(g80,g81)
    c: Coincident(g81,g82)
    c: Coincident(g82,g83)
    c: Coincident(g83,g84)
    c: Coincident(g84,g85)
    c: Coincident(g85,g86)
    c: Coincident(g86,g87)
    c: Coincident(g87,g88)
    c: Coincident(g88,g89)
    c: Coincident(g89,g90)
    c: Coincident(g90,g91)
    c: Coincident(g91,g92)
    c: Coincident(g92,g93)
    c: Coincident(g93,g94)
    c: Coincident(g94,g95)
    c: Coincident(g95,g96)
    c: Coincident(g96,g97)
    c: Coincident(g97,g98)
    c: Coincident(g98,g99)
    c: Coincident(g99,g100)
    c: Coincident(g100,g101)
    c: Coincident(g101,g102)
    c: Coincident(g102,g103)
    c: Coincident(g103,g104)
    c: Coincident(g104,g105)
    c: Coincident(g105,g106)
    c: Coincident(g106,g107)
    c: Coincident(g107,g108)
    c: Coincident(g108,g109)
    c: Coincident(g109,g110)
    c: Coincident(g110,g111)
    c: Coincident(g111,g112)
    c: Coincident(g112,g113)
    c: Coincident(g113,g114)
    c: Coincident(g114,g115)
    c: Coincident(g115,g116)
    c: Coincident(g116,g117)
    c: Coincident(g117,g118)
    c: Coincident(g118,g119)
    c: Coincident(g119,g120)
    c: Coincident(g120,g121)
    c: Coincident(g121,g122)
    c: Coincident(g122,g123)
    c: Coincident(g123,g124)
    c: Coincident(g124,g125)
    c: Coincident(g125,g126)
    c: Coincident(g126,g127)
    c: Coincident(g127,g128)
    c: Coincident(g128,g129)
    c: Coincident(g129,g130)
    c: Coincident(g130,g131)
    c: Coincident(g131,g132)
    c: Coincident(g132,g133)
    c: Coincident(g133,g134)
    c: Coincident(g134,g135)
    c: Coincident(g135,g136)
    c: Coincident(g136,g137)
    c: Coincident(g137,g138)
    c: Coincident(g138,g139)
    c: Coincident(g139,g140)
    c: Coincident(g140,g141)
    c: Coincident(g141,g142)
    c: Coincident(g142,g143)
    c: Coincident(g143,g144)
    c: Coincident(g144,g145)
    c: Coincident(g145,g146)
    c: Coincident(g146,g147)
    c: Coincident(g147,g148)
    c: Coincident(g148,g149)
    c: Coincident(g149,g150)
    c: Coincident(g150,g151)
    c: Coincident(g151,g152)
    c: Coincident(g152,g153)
    c: Coincident(g153,g154)
    c: Coincident(g154,g155)
    c: Coincident(g155,g156)
    c: Coincident(g156,g157)
    c: Coincident(g157,g158)
    c: Coincident(g158,g159)
    c: Coincident(g159,g160)
    c: Coincident(g160,g161)
    c: Coincident(g161,g162)
    c: Coincident(g162,g163)
    c: Coincident(g163,g164)
    c: Coincident(g164,g165)
    c: Coincident(g165,g166)
    c: Coincident(g166,g167)
    c: Coincident(g167,g168)
    c: Coincident(g168,g169)
    c: Coincident(g169,g170)
    c: Coincident(g170,g171)
    c: Coincident(g171,g172)
    c: Coincident(g172,g173)
    c: Coincident(g173,g174)
    c: Coincident(g174,g175)
    c: Coincident(g175,g176)
    c: Coincident(g176,g177)
    c: Coincident(g177,g178)
    c: Coincident(g178,g179)
    c: Coincident(g179,g180)
    c: Coincident(g180,g181)
    c: Coincident(g181,g182)
    c: Coincident(g182,g183)
    c: Coincident(g183,g184)
    c: Coincident(g184,g185)
    c: Coincident(g185,g186)
    c: Coincident(g186,g187)
    c: Coincident(g187,g188)
    c: Coincident(g188,g189)
    c: Coincident(g189,g190)
    c: Coincident(g190,g191)
    c: Coincident(g191,g192)
    c: Coincident(g192,g193)
    c: Coincident(g193,g194)
    c: Coincident(g194,g195)
    c: Coincident(g195,g196)
    c: Coincident(g196,g197)
    c: Coincident(g197,g198)
    c: Coincident(g198,g199)
    c: Coincident(g199,g200)
    c: Coincident(g200,g201)
    c: Coincident(g201,g202)
    c: Coincident(g202,g203)
    c: Coincident(g203,g204)
    c: Coincident(g204,g205)
    c: Coincident(g205,g206)
    c: Coincident(g206,g207)
    c: Coincident(g207,g208)
    c: Coincident(g208,g209)
    c: Coincident(g0,g210)
    c: Coincident(g0,g-1)
    c: Coincident(g209,g210)
FEATURE [PartDesign::Pad] Pad006
  Length = 3
  Length2 = 100
  Placement = pos=(0,0,0) rot=(0.57735,0.57735,0.57735;2.0944rad)
  Profile = -> Sketch005
  Type = 0
FEATURE [Sketcher::SketchObject] Sketch006
  MapMode = 5
  Placement = pos=(0,0,0) rot=(0.57735,0.57735,0.57735;2.0944rad)
  Support = -> [YZ_Plane008]
  sketch-geometry (20):
    g0: LineSegment StartX=1.84977 StartY=-2.03462 StartZ=0 EndX=1.64219 EndY=-2.20542 EndZ=0
    g1: LineSegment StartX=1.64219 StartY=-2.20542 StartZ=0 EndX=1.4178 EndY=-2.35642 EndZ=0
    g2: LineSegment StartX=1.4178 StartY=-2.35642 StartZ=0 EndX=1.1786 EndY=-2.48192 EndZ=0
    g3: LineSegment StartX=1.1786 StartY=-2.48192 StartZ=0 EndX=0.933165 EndY=-2.58946 EndZ=0
    g4: LineSegment StartX=0.933165 StartY=-2.58946 StartZ=0 EndX=0.669297 EndY=-2.66615 EndZ=0
    g5: LineSegment StartX=0.669297 StartY=-2.66615 StartZ=0 EndX=0.401357 EndY=-2.72007 EndZ=0
    g6: LineSegment StartX=0.401357 StartY=-2.72007 StartZ=0 EndX=0.133198 EndY=-2.74689 EndZ=0
    g7: LineSegment StartX=0.133198 StartY=-2.74689 StartZ=0 EndX=-0.13715 EndY=-2.74708 EndZ=0
    g8: LineSegment StartX=-0.13715 StartY=-2.74708 StartZ=0 EndX=-0.688499 EndY=-2.66151 EndZ=0
    g9: LineSegment StartX=-0.688499 StartY=-2.66151 StartZ=0 EndX=-0.94393 EndY=-2.58392 EndZ=0
    g10: LineSegment StartX=-0.94393 StartY=-2.58392 StartZ=0 EndX=-1.18786 EndY=-2.4818 EndZ=0
    g11: LineSegment StartX=-1.18786 StartY=-2.4818 StartZ=0 EndX=-1.42897 EndY=-2.34335 EndZ=0
    g12: LineSegment StartX=-1.42897 StartY=-2.34335 StartZ=0 EndX=-1.64859 EndY=-2.19653 EndZ=0
    g13: LineSegment StartX=-1.64859 StartY=-2.19653 StartZ=0 EndX=-1.84554 EndY=-2.0342 EndZ=0
    g14: LineSegment StartX=-1.84554 StartY=-2.0342 StartZ=0 EndX=-1.84465 EndY=-1.22163 EndZ=0
    g15: LineSegment StartX=-1.84465 StartY=-1.22163 StartZ=0 EndX=-1.84999 EndY=-0.000151 EndZ=0
    g16: LineSegment StartX=-1.84999 StartY=-0.000151 StartZ=0 EndX=-1.85002 EndY=0.00099 EndZ=0
    g17: LineSegment StartX=-1.85002 StartY=0.00099 StartZ=0 EndX=1.85015 EndY=0.005067 EndZ=0
    g18: LineSegment StartX=1.84931 StartY=-2.02283 StartZ=0 EndX=1.84977 EndY=-2.03462 EndZ=0
    g19: LineSegment StartX=1.85015 StartY=0.005067 StartZ=0 EndX=1.84931 EndY=-2.02283 EndZ=0
  constraints (20):
    c: Coincident(g0,g1)
    c: Coincident(g1,g2)
    c: Coincident(g2,g3)
    c: Coincident(g3,g4)
    c: Coincident(g4,g5)
    c: Coincident(g5,g6)
    c: Coincident(g8,g9)
    c: Coincident(g9,g10)
    c: Coincident(g10,g11)
    c: Coincident(g11,g12)
    c: Coincident(g12,g13)
    c: Coincident(g13,g14)
    c: Coincident(g14,g15)
    c: Coincident(g15,g16)
    c: Coincident(g16,g17)
    c: Coincident(g0,g18)
    c: Coincident(g7,g8)
    c: Coincident(g6,g7)
    c: Coincident(g18,g19)
    c: Coincident(g17,g19)
FEATURE [PartDesign::Pad] Pad005
  Length = 100
  Length2 = 100
  Midplane = true
  Placement = pos=(0,0,0) rot=(0.57735,0.57735,0.57735;2.0944rad)
  Profile = -> Sketch006
  Type = 0
FEATURE [PartDesign::PolarPattern] PolarPattern005
  Angle = 360
  Axis = -> Sketch006 [N_Axis]
  BaseFeature = -> Pad005
  Occurrences = 2
  Originals = -> [Pad005]
  Placement = pos=(0,0,0) rot=(0.57735,0.57735,0.57735;2.0944rad)
FEATURE [PartDesign::Body] Body005
  Group = -> [Sketch006,Pad005,PolarPattern005]
  Origin = -> Origin005
  Tip = -> PolarPattern005
FEATURE [PartDesign::PolarPattern] PolarPattern006
  Angle = 360
  Axis = -> Sketch005 [N_Axis]
  BaseFeature = -> Pad006
  Occurrences = 4
  Originals = -> [Pad006]
  Placement = pos=(0,0,0) rot=(0.57735,0.57735,0.57735;2.0944rad)
FEATURE [PartDesign::Body] Body006
  Group = -> [Sketch005,Pad006,PolarPattern006]
  Origin = -> Origin008
  Tip = -> PolarPattern006
FEATURE [Part::Cut] Cut003
  Base = -> Body006
  Placement = pos=(0,0,1) rot=(0,0,1;0rad)
  Tool = -> Body005
FEATURE [Sketcher::SketchObject] Sketch007
  MapMode = 5
  Placement = pos=(0,0,0) rot=(0.57735,0.57735,0.57735;2.0944rad)
  Support = -> [YZ_Plane005]
  sketch-geometry (20):
    g0: LineSegment StartX=1.84977 StartY=-2.03462 StartZ=0 EndX=1.64219 EndY=-2.20542 EndZ=0
    g1: LineSegment StartX=1.64219 StartY=-2.20542 StartZ=0 EndX=1.4178 EndY=-2.35642 EndZ=0
    g2: LineSegment StartX=1.4178 StartY=-2.35642 StartZ=0 EndX=1.1786 EndY=-2.48192 EndZ=0
    g3: LineSegment StartX=1.1786 StartY=-2.48192 StartZ=0 EndX=0.933165 EndY=-2.58946 EndZ=0
    g4: LineSegment StartX=0.933165 StartY=-2.58946 StartZ=0 EndX=0.669297 EndY=-2.66615 EndZ=0
    g5: LineSegment StartX=0.669297 StartY=-2.66615 StartZ=0 EndX=0.401357 EndY=-2.72007 EndZ=0
    g6: LineSegment StartX=0.401357 StartY=-2.72007 StartZ=0 EndX=0.133198 EndY=-2.74689 EndZ=0
    g7: LineSegment StartX=0.133198 StartY=-2.74689 StartZ=0 EndX=-0.13715 EndY=-2.74708 EndZ=0
    g8: LineSegment StartX=-0.13715 StartY=-2.74708 StartZ=0 EndX=-0.688499 EndY=-2.66151 EndZ=0
    g9: LineSegment StartX=-0.688499 StartY=-2.66151 StartZ=0 EndX=-0.94393 EndY=-2.58392 EndZ=0
    g10: LineSegment StartX=-0.94393 StartY=-2.58392 StartZ=0 EndX=-1.18786 EndY=-2.4818 EndZ=0
    g11: LineSegment StartX=-1.18786 StartY=-2.4818 StartZ=0 EndX=-1.42897 EndY=-2.34335 EndZ=0
    g12: LineSegment StartX=-1.42897 StartY=-2.34335 StartZ=0 EndX=-1.64859 EndY=-2.19653 EndZ=0
    g13: LineSegment StartX=-1.64859 StartY=-2.19653 StartZ=0 EndX=-1.84554 EndY=-2.0342 EndZ=0
    g14: LineSegment StartX=-1.84554 StartY=-2.0342 StartZ=0 EndX=-1.84465 EndY=-1.22163 EndZ=0
    g15: LineSegment StartX=-1.84465 StartY=-1.22163 StartZ=0 EndX=-1.84999 EndY=-0.000151 EndZ=0
    g16: LineSegment StartX=-1.84999 StartY=-0.000151 StartZ=0 EndX=-1.85002 EndY=0.00099 EndZ=0
    g17: LineSegment StartX=-1.85002 StartY=0.00099 StartZ=0 EndX=1.85015 EndY=0.005067 EndZ=0
    g18: LineSegment StartX=1.84931 StartY=-2.02283 StartZ=0 EndX=1.84977 EndY=-2.03462 EndZ=0
    g19: LineSegment StartX=1.85015 StartY=0.005067 StartZ=0 EndX=1.84931 EndY=-2.02283 EndZ=0
  constraints (20):
    c: Coincident(g0,g1)
    c: Coincident(g1,g2)
    c: Coincident(g2,g3)
    c: Coincident(g3,g4)
    c: Coincident(g4,g5)
    c: Coincident(g5,g6)
    c: Coincident(g8,g9)
    c: Coincident(g9,g10)
    c: Coincident(g10,g11)
    c: Coincident(g11,g12)
    c: Coincident(g12,g13)
    c: Coincident(g13,g14)
    c: Coincident(g14,g15)
    c: Coincident(g15,g16)
    c: Coincident(g16,g17)
    c: Coincident(g0,g18)
    c: Coincident(g7,g8)
    c: Coincident(g6,g7)
    c: Coincident(g18,g19)
    c: Coincident(g17,g19)
FEATURE [PartDesign::Pad] Pad008
  Length = 100
  Length2 = 100
  Midplane = true
  Placement = pos=(0,0,0) rot=(0.57735,0.57735,0.57735;2.0944rad)
  Profile = -> Sketch007
  Type = 0
FEATURE [PartDesign::PolarPattern] PolarPattern007
  Angle = 360
  Axis = -> Sketch007 [N_Axis]
  BaseFeature = -> Pad008
  Occurrences = 2
  Originals = -> [Pad008]
  Placement = pos=(0,0,0) rot=(0.57735,0.57735,0.57735;2.0944rad)
FEATURE [PartDesign::Body] Body008
  Group = -> [Sketch007,Pad008,PolarPattern007]
  Origin = -> Origin007
  Tip = -> PolarPattern007
FEATURE [Sketcher::SketchObject] Sketch008
  MapMode = 5
  Placement = pos=(0,0,0) rot=(0.57735,0.57735,0.57735;2.0944rad)
  Support = -> [YZ_Plane006]
  sketch-geometry (211):
    g0: LineSegment StartX=0 StartY=0 StartZ=0 EndX=23.0775 EndY=-0.007725 EndZ=0
    g1: LineSegment StartX=23.0775 StartY=-0.007725 StartZ=0 EndX=23.0915 EndY=0.254478 EndZ=0
    g2: LineSegment StartX=23.0915 StartY=0.254478 StartZ=0 EndX=23.1284 EndY=0.508391 EndZ=0
    g3: LineSegment StartX=23.1284 StartY=0.508391 StartZ=0 EndX=23.1869 EndY=0.740712 EndZ=0
    g4: LineSegment StartX=23.1869 StartY=0.740712 StartZ=0 EndX=23.2782 EndY=0.973565 EndZ=0
    g5: LineSegment StartX=23.2782 StartY=0.973565 StartZ=0 EndX=23.3963 EndY=1.22031 EndZ=0
    g6: LineSegment StartX=23.3963 StartY=1.22031 StartZ=0 EndX=23.5215 EndY=1.42239 EndZ=0
    g7: LineSegment StartX=23.5215 StartY=1.42239 StartZ=0 EndX=23.6745 EndY=1.62203 EndZ=0
    g8: LineSegment StartX=23.6745 StartY=1.62203 StartZ=0 EndX=23.8622 EndY=1.81795 EndZ=0
    g9: LineSegment StartX=23.8622 StartY=1.81795 StartZ=0 EndX=24.0428 EndY=1.97182 EndZ=0
    g10: LineSegment StartX=24.0428 StartY=1.97182 StartZ=0 EndX=24.2535 EndY=2.11914 EndZ=0
    g11: LineSegment StartX=24.2535 StartY=2.11914 StartZ=0 EndX=24.4771 EndY=2.24429 EndZ=0
    g12: LineSegment StartX=24.4771 StartY=2.24429 StartZ=0 EndX=24.7643 EndY=2.36841 EndZ=0
    g13: LineSegment StartX=24.7643 StartY=2.36841 StartZ=0 EndX=24.8553 EndY=2.41105 EndZ=0
    g14: LineSegment StartX=24.8553 StartY=2.41105 StartZ=0 EndX=24.9955 EndY=2.50386 EndZ=0
    g15: LineSegment StartX=24.9955 StartY=2.50386 StartZ=0 EndX=25.1151 EndY=2.62736 EndZ=0
    g16: LineSegment StartX=25.1151 StartY=2.62736 StartZ=0 EndX=25.2142 EndY=2.76003 EndZ=0
    g17: LineSegment StartX=25.2142 StartY=2.76003 StartZ=0 EndX=25.2969 EndY=2.93426 EndZ=0
    g18: LineSegment StartX=25.2969 StartY=2.93426 StartZ=0 EndX=25.3426 EndY=3.08419 EndZ=0
    g19: LineSegment StartX=25.3426 StartY=3.08419 StartZ=0 EndX=25.3551 EndY=3.24413 EndZ=0
    g20: LineSegment StartX=25.3551 StartY=3.24413 StartZ=0 EndX=25.349 EndY=3.41794 EndZ=0
    g21: LineSegment StartX=25.349 StartY=3.41794 StartZ=0 EndX=25.3326 EndY=3.53796 EndZ=0
    g22: LineSegment StartX=25.3326 StartY=3.53796 StartZ=0 EndX=25.2546 EndY=4.05249 EndZ=0
    g23: LineSegment StartX=25.2546 StartY=4.05249 StartZ=0 EndX=25.1642 EndY=4.58451 EndZ=0
    g24: LineSegment StartX=25.1642 StartY=4.58451 StartZ=0 EndX=25.1211 EndY=4.74519 EndZ=0
    g25: LineSegment StartX=25.1211 StartY=4.74519 StartZ=0 EndX=25.0493 EndY=4.90009 EndZ=0
    g26: LineSegment StartX=25.0493 StartY=4.90009 StartZ=0 EndX=24.9559 EndY=5.03652 EndZ=0
    g27: LineSegment StartX=24.9559 StartY=5.03652 StartZ=0 EndX=24.8359 EndY=5.16166 EndZ=0
    g28: LineSegment StartX=24.8359 StartY=5.16166 StartZ=0 EndX=24.7064 EndY=5.26066 EndZ=0
    g29: LineSegment StartX=24.7064 StartY=5.26066 StartZ=0 EndX=24.5515 EndY=5.33657 EndZ=0
    g30: LineSegment StartX=24.5515 StartY=5.33657 StartZ=0 EndX=24.3854 EndY=5.38889 EndZ=0
    g31: LineSegment StartX=24.3854 StartY=5.38889 StartZ=0 EndX=23.9661 EndY=5.429 EndZ=0
    g32: LineSegment StartX=23.9661 StartY=5.429 StartZ=0 EndX=23.7168 EndY=5.47721 EndZ=0
    g33: LineSegment StartX=23.7168 StartY=5.47721 StartZ=0 EndX=23.4789 EndY=5.55004 EndZ=0
    g34: LineSegment StartX=23.4789 StartY=5.55004 StartZ=0 EndX=23.244 EndY=5.64749 EndZ=0
    g35: LineSegment StartX=23.244 StartY=5.64749 StartZ=0 EndX=23.0141 EndY=5.77459 EndZ=0
    g36: LineSegment StartX=23.0141 StartY=5.77459 StartZ=0 EndX=22.81 EndY=5.91307 EndZ=0
    g37: LineSegment StartX=22.81 StartY=5.91307 StartZ=0 EndX=22.6171 EndY=6.07925 EndZ=0
    g38: LineSegment StartX=22.6171 StartY=6.07925 StartZ=0 EndX=22.4499 EndY=6.25158 EndZ=0
    g39: LineSegment StartX=22.4499 StartY=6.25158 StartZ=0 EndX=22.2897 EndY=6.45644 EndZ=0
    g40: LineSegment StartX=22.2897 StartY=6.45644 StartZ=0 EndX=22.1484 EndY=6.67133 EndZ=0
    g41: LineSegment StartX=22.1484 StartY=6.67133 StartZ=0 EndX=22.0413 EndY=6.89628 EndZ=0
    g42: LineSegment StartX=22.0413 StartY=6.89628 StartZ=0 EndX=21.9449 EndY=7.13041 EndZ=0
    g43: LineSegment StartX=21.9449 StartY=7.13041 StartZ=0 EndX=21.883 EndY=7.36574 EndZ=0
    g44: LineSegment StartX=21.883 StartY=7.36574 StartZ=0 EndX=21.842 EndY=7.61808 EndZ=0
    g45: LineSegment StartX=21.842 StartY=7.61808 StartZ=0 EndX=21.8244 EndY=7.88752 EndZ=0
    g46: LineSegment StartX=21.8244 StartY=7.88752 StartZ=0 EndX=21.8388 EndY=8.12242 EndZ=0
    g47: LineSegment StartX=21.8388 StartY=8.12242 StartZ=0 EndX=21.8716 EndY=8.3765 EndZ=0
    g48: LineSegment StartX=21.8716 StartY=8.3765 StartZ=0 EndX=21.9322 EndY=8.62371 EndZ=0
    g49: LineSegment StartX=21.9322 StartY=8.62371 StartZ=0 EndX=22.0085 EndY=8.85622 EndZ=0
    g50: LineSegment StartX=22.0085 StartY=8.85622 StartZ=0 EndX=22.1095 EndY=9.0873 EndZ=0
    g51: LineSegment StartX=22.1095 StartY=9.0873 StartZ=0 EndX=22.2564 EndY=9.30001 EndZ=0
    g52: LineSegment StartX=22.2564 StartY=9.30001 StartZ=0 EndX=22.4222 EndY=9.51816 EndZ=0
    g53: LineSegment StartX=22.4222 StartY=9.51816 StartZ=0 EndX=22.5814 EndY=9.69568 EndZ=0
    g54: LineSegment StartX=22.5814 StartY=9.69568 StartZ=0 EndX=22.7773 EndY=9.86401 EndZ=0
    g55: LineSegment StartX=22.7773 StartY=9.86401 StartZ=0 EndX=22.8829 EndY=9.96654 EndZ=0
    g56: LineSegment StartX=22.8829 StartY=9.96654 StartZ=0 EndX=22.9946 EndY=10.1027 EndZ=0
    g57: LineSegment StartX=22.9946 StartY=10.1027 StartZ=0 EndX=23.0728 EndY=10.2473 EndZ=0
    g58: LineSegment StartX=23.0728 StartY=10.2473 StartZ=0 EndX=23.1295 EndY=10.4111 EndZ=0
    g59: LineSegment StartX=23.1295 StartY=10.4111 StartZ=0 EndX=23.1555 EndY=10.5871 EndZ=0
    g60: LineSegment StartX=23.1555 StartY=10.5871 StartZ=0 EndX=23.1416 EndY=10.7621 EndZ=0
    g61: LineSegment StartX=23.1416 StartY=10.7621 StartZ=0 EndX=23.1095 EndY=10.9289 EndZ=0
    g62: LineSegment StartX=23.1095 StartY=10.9289 StartZ=0 EndX=23.0483 EndY=11.0865 EndZ=0
    g63: LineSegment StartX=23.0483 StartY=11.0865 StartZ=0 EndX=22.8718 EndY=11.4442 EndZ=0
    g64: LineSegment StartX=22.8718 StartY=11.4442 StartZ=0 EndX=22.5688 EndY=12.0257 EndZ=0
    g65: LineSegment StartX=22.5688 StartY=12.0257 StartZ=0 EndX=22.5075 EndY=12.152 EndZ=0
    g66: LineSegment StartX=22.5075 StartY=12.152 StartZ=0 EndX=22.4248 EndY=12.279 EndZ=0
    g67: LineSegment StartX=22.4248 StartY=12.279 StartZ=0 EndX=22.3208 EndY=12.3999 EndZ=0
    g68: LineSegment StartX=22.3208 StartY=12.3999 StartZ=0 EndX=22.1769 EndY=12.5009 EndZ=0
    g69: LineSegment StartX=22.1769 StartY=12.5009 StartZ=0 EndX=22.0254 EndY=12.5805 EndZ=0
    g70: LineSegment StartX=22.0254 StartY=12.5805 StartZ=0 EndX=21.8678 EndY=12.6325 EndZ=0
    g71: LineSegment StartX=21.8678 StartY=12.6325 StartZ=0 EndX=21.6949 EndY=12.6601 EndZ=0
    g72: LineSegment StartX=21.6949 StartY=12.6601 StartZ=0 EndX=21.5327 EndY=12.6555 EndZ=0
    g73: LineSegment StartX=21.5327 StartY=12.6555 StartZ=0 EndX=21.1061 EndY=12.5612 EndZ=0
    g74: LineSegment StartX=21.1061 StartY=12.5612 StartZ=0 EndX=20.8582 EndY=12.5352 EndZ=0
    g75: LineSegment StartX=20.8582 StartY=12.5352 StartZ=0 EndX=20.6087 EndY=12.5337 EndZ=0
    g76: LineSegment StartX=20.6087 StartY=12.5337 StartZ=0 EndX=20.3501 EndY=12.5536 EndZ=0
    g77: LineSegment StartX=20.3501 StartY=12.5536 StartZ=0 EndX=20.0854 EndY=12.5979 EndZ=0
    g78: LineSegment StartX=20.0854 StartY=12.5979 StartZ=0 EndX=19.8665 EndY=12.6699 EndZ=0
    g79: LineSegment StartX=19.8665 StartY=12.6699 StartZ=0 EndX=19.614 EndY=12.7678 EndZ=0
    g80: LineSegment StartX=19.614 StartY=12.7678 StartZ=0 EndX=19.4105 EndY=12.881 EndZ=0
    g81: LineSegment StartX=19.4105 StartY=12.881 StartZ=0 EndX=19.1993 EndY=13.0264 EndZ=0
    g82: LineSegment StartX=19.1993 StartY=13.0264 StartZ=0 EndX=18.9927 EndY=13.2018 EndZ=0
    g83: LineSegment StartX=18.9927 StartY=13.2018 StartZ=0 EndX=18.8259 EndY=13.3625 EndZ=0
    g84: LineSegment StartX=18.8259 StartY=13.3625 StartZ=0 EndX=18.6714 EndY=13.5553 EndZ=0
    g85: LineSegment StartX=18.6714 StartY=13.5553 StartZ=0 EndX=18.5367 EndY=13.768 EndZ=0
    g86: LineSegment StartX=18.5367 StartY=13.768 StartZ=0 EndX=18.4051 EndY=14.0083 EndZ=0
    g87: LineSegment StartX=18.4051 StartY=14.0083 StartZ=0 EndX=18.3225 EndY=14.2255 EndZ=0
    g88: LineSegment StartX=18.3225 StartY=14.2255 StartZ=0 EndX=18.2506 EndY=14.4903 EndZ=0
    g89: LineSegment StartX=18.2506 StartY=14.4903 StartZ=0 EndX=18.2154 EndY=14.7183 EndZ=0
    g90: LineSegment StartX=18.2154 StartY=14.7183 StartZ=0 EndX=18.2017 EndY=14.9876 EndZ=0
    g91: LineSegment StartX=18.2017 StartY=14.9876 StartZ=0 EndX=18.1828 EndY=15.2236 EndZ=0
    g92: LineSegment StartX=18.1828 StartY=15.2236 StartZ=0 EndX=18.2304 EndY=15.4722 EndZ=0
    g93: LineSegment StartX=18.2304 StartY=15.4722 StartZ=0 EndX=18.2815 EndY=15.714 EndZ=0
    g94: LineSegment StartX=18.2815 StartY=15.714 StartZ=0 EndX=18.3735 EndY=15.9865 EndZ=0
    g95: LineSegment StartX=18.3735 StartY=15.9865 StartZ=0 EndX=18.4796 EndY=16.216 EndZ=0
    g96: LineSegment StartX=18.4796 StartY=16.216 StartZ=0 EndX=18.6771 EndY=16.5429 EndZ=0
    g97: LineSegment StartX=18.6771 StartY=16.5429 StartZ=0 EndX=18.7452 EndY=16.7132 EndZ=0
    g98: LineSegment StartX=18.7452 StartY=16.7132 StartZ=0 EndX=18.7725 EndY=16.8562 EndZ=0
    g99: LineSegment StartX=18.7725 StartY=16.8562 StartZ=0 EndX=18.7793 EndY=17.0538 EndZ=0
    g100: LineSegment StartX=18.7793 StartY=17.0538 StartZ=0 EndX=18.7515 EndY=17.1989 EndZ=0
    g101: LineSegment StartX=18.7515 StartY=17.1989 StartZ=0 EndX=18.7073 EndY=17.3454 EndZ=0
    g102: LineSegment StartX=18.7073 StartY=17.3454 StartZ=0 EndX=18.6221 EndY=17.4986 EndZ=0
    g103: LineSegment StartX=18.6221 StartY=17.4986 StartZ=0 EndX=18.5404 EndY=17.6076 EndZ=0
    g104: LineSegment StartX=18.5404 StartY=17.6076 StartZ=0 EndX=18.4484 EndY=17.7132 EndZ=0
    g105: LineSegment StartX=18.4484 StartY=17.7132 StartZ=0 EndX=17.7843 EndY=18.3841 EndZ=0
    g106: LineSegment StartX=17.7843 StartY=18.3841 StartZ=0 EndX=17.6004 EndY=18.5476 EndZ=0
    g107: LineSegment StartX=17.6004 StartY=18.5476 StartZ=0 EndX=17.5187 EndY=18.6089 EndZ=0
    g108: LineSegment StartX=17.5187 StartY=18.6089 StartZ=0 EndX=17.3654 EndY=18.6872 EndZ=0
    g109: LineSegment StartX=17.3654 StartY=18.6872 StartZ=0 EndX=17.2156 EndY=18.7383 EndZ=0
    g110: LineSegment StartX=17.2156 StartY=18.7383 StartZ=0 EndX=17.0487 EndY=18.7621 EndZ=0
    g111: LineSegment StartX=17.0487 StartY=18.7621 StartZ=0 EndX=16.8852 EndY=18.7724 EndZ=0
    g112: LineSegment StartX=16.8852 StartY=18.7724 StartZ=0 EndX=16.7183 EndY=18.7417 EndZ=0
    g113: LineSegment StartX=16.7183 StartY=18.7417 StartZ=0 EndX=16.5651 EndY=18.694 EndZ=0
    g114: LineSegment StartX=16.5651 StartY=18.694 StartZ=0 EndX=16.3709 EndY=18.5851 EndZ=0
    g115: LineSegment StartX=16.3709 StartY=18.5851 StartZ=0 EndX=16.1496 EndY=18.4522 EndZ=0
    g116: LineSegment StartX=16.1496 StartY=18.4522 StartZ=0 EndX=15.9752 EndY=18.3739 EndZ=0
    g117: LineSegment StartX=15.9752 StartY=18.3739 StartZ=0 EndX=15.7423 EndY=18.2963 EndZ=0
    g118: LineSegment StartX=15.7423 StartY=18.2963 StartZ=0 EndX=15.5003 EndY=18.2233 EndZ=0
    g119: LineSegment StartX=15.5003 StartY=18.2233 StartZ=0 EndX=15.2492 EndY=18.1982 EndZ=0
    g120: LineSegment StartX=15.2492 StartY=18.1982 StartZ=0 EndX=14.973 EndY=18.2004 EndZ=0
    g121: LineSegment StartX=14.973 StartY=18.2004 StartZ=0 EndX=14.7241 EndY=18.2141 EndZ=0
    g122: LineSegment StartX=14.7241 StartY=18.2141 StartZ=0 EndX=14.4685 EndY=18.2484 EndZ=0
    g123: LineSegment StartX=14.4685 StartY=18.2484 StartZ=0 EndX=14.2265 EndY=18.3192 EndZ=0
    g124: LineSegment StartX=14.2265 StartY=18.3192 StartZ=0 EndX=13.9799 EndY=18.4196 EndZ=0
    g125: LineSegment StartX=13.9799 StartY=18.4196 StartZ=0 EndX=13.7736 EndY=18.5304 EndZ=0
    g126: LineSegment StartX=13.7736 StartY=18.5304 StartZ=0 EndX=13.5557 EndY=18.6666 EndZ=0
    g127: LineSegment StartX=13.5557 StartY=18.6666 StartZ=0 EndX=13.3683 EndY=18.8267 EndZ=0
    g128: LineSegment StartX=13.3683 StartY=18.8267 StartZ=0 EndX=13.1844 EndY=18.997 EndZ=0
    g129: LineSegment StartX=13.1844 StartY=18.997 StartZ=0 EndX=13.0175 EndY=19.2047 EndZ=0
    g130: LineSegment StartX=13.0175 StartY=19.2047 StartZ=0 EndX=12.9086 EndY=19.4227 EndZ=0
    g131: LineSegment StartX=12.9086 StartY=19.4227 StartZ=0 EndX=12.694 EndY=19.8518 EndZ=0
    g132: LineSegment StartX=12.694 StartY=19.8518 StartZ=0 EndX=12.5986 EndY=20.1266 EndZ=0
    g133: LineSegment StartX=12.5986 StartY=20.1266 StartZ=0 EndX=12.5373 EndY=20.3616 EndZ=0
    g134: LineSegment StartX=12.5373 StartY=20.3616 StartZ=0 EndX=12.5305 EndY=20.6613 EndZ=0
    g135: LineSegment StartX=12.5305 StartY=20.6613 StartZ=0 EndX=12.527 EndY=20.852 EndZ=0
    g136: LineSegment StartX=12.527 StartY=20.852 StartZ=0 EndX=12.5713 EndY=21.1177 EndZ=0
    g137: LineSegment StartX=12.5713 StartY=21.1177 StartZ=0 EndX=12.6565 EndY=21.5025 EndZ=0
    g138: LineSegment StartX=12.6565 StartY=21.5025 StartZ=0 EndX=12.6531 EndY=21.7205 EndZ=0
    g139: LineSegment StartX=12.6531 StartY=21.7205 StartZ=0 EndX=12.6258 EndY=21.8771 EndZ=0
    g140: LineSegment StartX=12.6258 StartY=21.8771 StartZ=0 EndX=12.5747 EndY=22.0542 EndZ=0
    g141: LineSegment StartX=12.5747 StartY=22.0542 StartZ=0 EndX=12.5027 EndY=22.1813 EndZ=0
    g142: LineSegment StartX=12.5027 StartY=22.1813 StartZ=0 EndX=12.3937 EndY=22.3278 EndZ=0
    g143: LineSegment StartX=12.3937 StartY=22.3278 StartZ=0 EndX=12.278 EndY=22.4299 EndZ=0
    g144: LineSegment StartX=12.278 StartY=22.4299 StartZ=0 EndX=12.1179 EndY=22.5287 EndZ=0
    g145: LineSegment StartX=12.1179 StartY=22.5287 StartZ=0 EndX=11.7535 EndY=22.716 EndZ=0
    g146: LineSegment StartX=11.7535 StartY=22.716 StartZ=0 EndX=11.2792 EndY=22.9552 EndZ=0
    g147: LineSegment StartX=11.2792 StartY=22.9552 StartZ=0 EndX=11.0374 EndY=23.0607 EndZ=0
    g148: LineSegment StartX=11.0374 StartY=23.0607 StartZ=0 EndX=10.8875 EndY=23.1289 EndZ=0
    g149: LineSegment StartX=10.8875 StartY=23.1289 StartZ=0 EndX=10.7036 EndY=23.1527 EndZ=0
    g150: LineSegment StartX=10.7036 StartY=23.1527 StartZ=0 EndX=10.5571 EndY=23.1391 EndZ=0
    g151: LineSegment StartX=10.5571 StartY=23.1391 StartZ=0 EndX=10.38 EndY=23.1084 EndZ=0
    g152: LineSegment StartX=10.38 StartY=23.1084 StartZ=0 EndX=10.2643 EndY=23.0641 EndZ=0
    g153: LineSegment StartX=10.2643 StartY=23.0641 StartZ=0 EndX=10.1042 EndY=22.9892 EndZ=0
    g154: LineSegment StartX=10.1042 StartY=22.9892 StartZ=0 EndX=9.97817 EndY=22.9041 EndZ=0
    g155: LineSegment StartX=9.97817 StartY=22.9041 StartZ=0 EndX=9.8181 EndY=22.727 EndZ=0
    g156: LineSegment StartX=9.8181 StartY=22.727 StartZ=0 EndX=9.68528 EndY=22.5839 EndZ=0
    g157: LineSegment StartX=9.68528 StartY=22.5839 StartZ=0 EndX=9.5184 EndY=22.4068 EndZ=0
    g158: LineSegment StartX=9.5184 StartY=22.4068 StartZ=0 EndX=9.29702 EndY=22.2672 EndZ=0
    g159: LineSegment StartX=9.29702 StartY=22.2672 StartZ=0 EndX=9.09042 EndY=22.1273 EndZ=0
    g160: LineSegment StartX=9.09042 StartY=22.1273 StartZ=0 EndX=8.85883 EndY=22.0183 EndZ=0
    g161: LineSegment StartX=8.85883 StartY=22.0183 StartZ=0 EndX=8.60681 EndY=21.9332 EndZ=0
    g162: LineSegment StartX=8.60681 StartY=21.9332 StartZ=0 EndX=8.36841 EndY=21.8719 EndZ=0
    g163: LineSegment StartX=8.36841 StartY=21.8719 StartZ=0 EndX=8.11979 EndY=21.8344 EndZ=0
    g164: LineSegment StartX=8.11979 StartY=21.8344 StartZ=0 EndX=7.84392 EndY=21.8242 EndZ=0
    g165: LineSegment StartX=7.84392 StartY=21.8242 StartZ=0 EndX=7.61915 EndY=21.8446 EndZ=0
    g166: LineSegment StartX=7.61915 StartY=21.8446 StartZ=0 EndX=7.39096 EndY=21.8753 EndZ=0
    g167: LineSegment StartX=7.39096 StartY=21.8753 StartZ=0 EndX=7.10488 EndY=21.9536 EndZ=0
    g168: LineSegment StartX=7.10488 StartY=21.9536 StartZ=0 EndX=6.8801 EndY=22.0387 EndZ=0
    g169: LineSegment StartX=6.8801 StartY=22.0387 StartZ=0 EndX=6.66554 EndY=22.1613 EndZ=0
    g170: LineSegment StartX=6.66554 StartY=22.1613 StartZ=0 EndX=6.44417 EndY=22.2908 EndZ=0
    g171: LineSegment StartX=6.44417 StartY=22.2908 StartZ=0 EndX=6.19215 EndY=22.5087 EndZ=0
    g172: LineSegment StartX=6.19215 StartY=22.5087 StartZ=0 EndX=6.02186 EndY=22.6688 EndZ=0
    g173: LineSegment StartX=6.02186 StartY=22.6688 StartZ=0 EndX=5.87882 EndY=22.8391 EndZ=0
    g174: LineSegment StartX=5.87882 StartY=22.8391 StartZ=0 EndX=5.74259 EndY=23.0809 EndZ=0
    g175: LineSegment StartX=5.74259 StartY=23.0809 StartZ=0 EndX=5.62679 EndY=23.2989 EndZ=0
    g176: LineSegment StartX=5.62679 StartY=23.2989 StartZ=0 EndX=5.54923 EndY=23.4812 EndZ=0
    g177: LineSegment StartX=5.54923 StartY=23.4812 StartZ=0 EndX=5.48987 EndY=23.7141 EndZ=0
    g178: LineSegment StartX=5.48987 StartY=23.7141 StartZ=0 EndX=5.43965 EndY=23.931 EndZ=0
    g179: LineSegment StartX=5.43965 StartY=23.931 StartZ=0 EndX=5.38283 EndY=24.3702 EndZ=0
    g180: LineSegment StartX=5.38283 StartY=24.3702 StartZ=0 EndX=5.34402 EndY=24.5505 EndZ=0
    g181: LineSegment StartX=5.34402 StartY=24.5505 StartZ=0 EndX=5.26412 EndY=24.7012 EndZ=0
    g182: LineSegment StartX=5.26412 StartY=24.7012 StartZ=0 EndX=5.15662 EndY=24.8433 EndZ=0
    g183: LineSegment StartX=5.15662 StartY=24.8433 StartZ=0 EndX=5.03563 EndY=24.9643 EndZ=0
    g184: LineSegment StartX=5.03563 StartY=24.9643 StartZ=0 EndX=4.9055 EndY=25.0534 EndZ=0
    g185: LineSegment StartX=4.9055 StartY=25.0534 StartZ=0 EndX=4.76168 EndY=25.115 EndZ=0
    g186: LineSegment StartX=4.76168 StartY=25.115 StartZ=0 EndX=4.56991 EndY=25.1698 EndZ=0
    g187: LineSegment StartX=4.56991 StartY=25.1698 StartZ=0 EndX=4.22291 EndY=25.2269 EndZ=0
    g188: LineSegment StartX=4.22291 StartY=25.2269 StartZ=0 EndX=3.72501 EndY=25.306 EndZ=0
    g189: LineSegment StartX=3.72501 StartY=25.306 StartZ=0 EndX=3.40823 EndY=25.3504 EndZ=0
    g190: LineSegment StartX=3.40823 StartY=25.3504 StartZ=0 EndX=3.25674 EndY=25.3565 EndZ=0
    g191: LineSegment StartX=3.25674 StartY=25.3565 StartZ=0 EndX=3.08534 EndY=25.3351 EndZ=0
    g192: LineSegment StartX=3.08534 StartY=25.3351 StartZ=0 EndX=2.91854 EndY=25.2876 EndZ=0
    g193: LineSegment StartX=2.91854 StartY=25.2876 StartZ=0 EndX=2.76092 EndY=25.2111 EndZ=0
    g194: LineSegment StartX=2.76092 StartY=25.2111 StartZ=0 EndX=2.62472 EndY=25.1116 EndZ=0
    g195: LineSegment StartX=2.62472 StartY=25.1116 StartZ=0 EndX=2.50842 EndY=24.9984 EndZ=0
    g196: LineSegment StartX=2.50842 StartY=24.9984 StartZ=0 EndX=2.41174 EndY=24.8483 EndZ=0
    g197: LineSegment StartX=2.41174 StartY=24.8483 StartZ=0 EndX=2.30308 EndY=24.582 EndZ=0
    g198: LineSegment StartX=2.30308 StartY=24.582 StartZ=0 EndX=2.25622 EndY=24.4788 EndZ=0
    g199: LineSegment StartX=2.25622 StartY=24.4788 StartZ=0 EndX=2.13227 EndY=24.2646 EndZ=0
    g200: LineSegment StartX=2.13227 StartY=24.2646 StartZ=0 EndX=1.96394 EndY=24.0365 EndZ=0
    g201: LineSegment StartX=1.96394 StartY=24.0365 StartZ=0 EndX=1.80479 EndY=23.856 EndZ=0
    g202: LineSegment StartX=1.80479 StartY=23.856 StartZ=0 EndX=1.62573 EndY=23.6797 EndZ=0
    g203: LineSegment StartX=1.62573 StartY=23.6797 StartZ=0 EndX=1.41955 EndY=23.5197 EndZ=0
    g204: LineSegment StartX=1.41955 StartY=23.5197 StartZ=0 EndX=1.20904 EndY=23.3867 EndZ=0
    g205: LineSegment StartX=1.20904 StartY=23.3867 StartZ=0 EndX=0.984393 EndY=23.2759 EndZ=0
    g206: LineSegment StartX=0.984393 StartY=23.2759 StartZ=0 EndX=0.742307 EndY=23.1856 EndZ=0
    g207: LineSegment StartX=0.742307 StartY=23.1856 StartZ=0 EndX=0.498622 EndY=23.1238 EndZ=0
    g208: LineSegment StartX=0.498622 StartY=23.1238 StartZ=0 EndX=0.250381 EndY=23.0889 EndZ=0
    g209: LineSegment StartX=0.250381 StartY=23.0889 StartZ=0 EndX=-0.006065 EndY=23.0756 EndZ=0
    g210: LineSegment StartX=-0.006065 StartY=23.0756 StartZ=0 EndX=0 EndY=0 EndZ=0
  constraints (212):
    c: Coincident(g0,g1)
    c: Coincident(g1,g2)
    c: Coincident(g2,g3)
    c: Coincident(g3,g4)
    c: Coincident(g4,g5)
    c: Coincident(g5,g6)
    c: Coincident(g6,g7)
    c: Coincident(g7,g8)
    c: Coincident(g8,g9)
    c: Coincident(g9,g10)
    c: Coincident(g10,g11)
    c: Coincident(g11,g12)
    c: Coincident(g12,g13)
    c: Coincident(g13,g14)
    c: Coincident(g14,g15)
    c: Coincident(g15,g16)
    c: Coincident(g16,g17)
    c: Coincident(g17,g18)
    c: Coincident(g18,g19)
    c: Coincident(g19,g20)
    c: Coincident(g20,g21)
    c: Coincident(g21,g22)
    c: Coincident(g22,g23)
    c: Coincident(g23,g24)
    c: Coincident(g24,g25)
    c: Coincident(g25,g26)
    c: Coincident(g26,g27)
    c: Coincident(g27,g28)
    c: Coincident(g28,g29)
    c: Coincident(g29,g30)
    c: Coincident(g30,g31)
    c: Coincident(g31,g32)
    c: Coincident(g32,g33)
    c: Coincident(g33,g34)
    c: Coincident(g34,g35)
    c: Coincident(g35,g36)
    c: Coincident(g36,g37)
    c: Coincident(g37,g38)
    c: Coincident(g38,g39)
    c: Coincident(g39,g40)
    c: Coincident(g40,g41)
    c: Coincident(g41,g42)
    c: Coincident(g42,g43)
    c: Coincident(g43,g44)
    c: Coincident(g44,g45)
    c: Coincident(g45,g46)
    c: Coincident(g46,g47)
    c: Coincident(g47,g48)
    c: Coincident(g48,g49)
    c: Coincident(g49,g50)
    c: Coincident(g50,g51)
    c: Coincident(g51,g52)
    c: Coincident(g52,g53)
    c: Coincident(g53,g54)
    c: Coincident(g54,g55)
    c: Coincident(g55,g56)
    c: Coincident(g56,g57)
    c: Coincident(g57,g58)
    c: Coincident(g58,g59)
    c: Coincident(g59,g60)
    c: Coincident(g60,g61)
    c: Coincident(g61,g62)
    c: Coincident(g62,g63)
    c: Coincident(g63,g64)
    c: Coincident(g64,g65)
    c: Coincident(g65,g66)
    c: Coincident(g66,g67)
    c: Coincident(g67,g68)
    c: Coincident(g68,g69)
    c: Coincident(g69,g70)
    c: Coincident(g70,g71)
    c: Coincident(g71,g72)
    c: Coincident(g72,g73)
    c: Coincident(g73,g74)
    c: Coincident(g74,g75)
    c: Coincident(g75,g76)
    c: Coincident(g76,g77)
    c: Coincident(g77,g78)
    c: Coincident(g78,g79)
    c: Coincident(g79,g80)
    c: Coincident(g80,g81)
    c: Coincident(g81,g82)
    c: Coincident(g82,g83)
    c: Coincident(g83,g84)
    c: Coincident(g84,g85)
    c: Coincident(g85,g86)
    c: Coincident(g86,g87)
    c: Coincident(g87,g88)
    c: Coincident(g88,g89)
    c: Coincident(g89,g90)
    c: Coincident(g90,g91)
    c: Coincident(g91,g92)
    c: Coincident(g92,g93)
    c: Coincident(g93,g94)
    c: Coincident(g94,g95)
    c: Coincident(g95,g96)
    c: Coincident(g96,g97)
    c: Coincident(g97,g98)
    c: Coincident(g98,g99)
    c: Coincident(g99,g100)
    c: Coincident(g100,g101)
    c: Coincident(g101,g102)
    c: Coincident(g102,g103)
    c: Coincident(g103,g104)
    c: Coincident(g104,g105)
    c: Coincident(g105,g106)
    c: Coincident(g106,g107)
    c: Coincident(g107,g108)
    c: Coincident(g108,g109)
    c: Coincident(g109,g110)
    c: Coincident(g110,g111)
    c: Coincident(g111,g112)
    c: Coincident(g112,g113)
    c: Coincident(g113,g114)
    c: Coincident(g114,g115)
    c: Coincident(g115,g116)
    c: Coincident(g116,g117)
    c: Coincident(g117,g118)
    c: Coincident(g118,g119)
    c: Coincident(g119,g120)
    c: Coincident(g120,g121)
    c: Coincident(g121,g122)
    c: Coincident(g122,g123)
    c: Coincident(g123,g124)
    c: Coincident(g124,g125)
    c: Coincident(g125,g126)
    c: Coincident(g126,g127)
    c: Coincident(g127,g128)
    c: Coincident(g128,g129)
    c: Coincident(g129,g130)
    c: Coincident(g130,g131)
    c: Coincident(g131,g132)
    c: Coincident(g132,g133)
    c: Coincident(g133,g134)
    c: Coincident(g134,g135)
    c: Coincident(g135,g136)
    c: Coincident(g136,g137)
    c: Coincident(g137,g138)
    c: Coincident(g138,g139)
    c: Coincident(g139,g140)
    c: Coincident(g140,g141)
    c: Coincident(g141,g142)
    c: Coincident(g142,g143)
    c: Coincident(g143,g144)
    c: Coincident(g144,g145)
    c: Coincident(g145,g146)
    c: Coincident(g146,g147)
    c: Coincident(g147,g148)
    c: Coincident(g148,g149)
    c: Coincident(g149,g150)
    c: Coincident(g150,g151)
    c: Coincident(g151,g152)
    c: Coincident(g152,g153)
    c: Coincident(g153,g154)
    c: Coincident(g154,g155)
    c: Coincident(g155,g156)
    c: Coincident(g156,g157)
    c: Coincident(g157,g158)
    c: Coincident(g158,g159)
    c: Coincident(g159,g160)
    c: Coincident(g160,g161)
    c: Coincident(g161,g162)
    c: Coincident(g162,g163)
    c: Coincident(g163,g164)
    c: Coincident(g164,g165)
    c: Coincident(g165,g166)
    c: Coincident(g166,g167)
    c: Coincident(g167,g168)
    c: Coincident(g168,g169)
    c: Coincident(g169,g170)
    c: Coincident(g170,g171)
    c: Coincident(g171,g172)
    c: Coincident(g172,g173)
    c: Coincident(g173,g174)
    c: Coincident(g174,g175)
    c: Coincident(g175,g176)
    c: Coincident(g176,g177)
    c: Coincident(g177,g178)
    c: Coincident(g178,g179)
    c: Coincident(g179,g180)
    c: Coincident(g180,g181)
    c: Coincident(g181,g182)
    c: Coincident(g182,g183)
    c: Coincident(g183,g184)
    c: Coincident(g184,g185)
    c: Coincident(g185,g186)
    c: Coincident(g186,g187)
    c: Coincident(g187,g188)
    c: Coincident(g188,g189)
    c: Coincident(g189,g190)
    c: Coincident(g190,g191)
    c: Coincident(g191,g192)
    c: Coincident(g192,g193)
    c: Coincident(g193,g194)
    c: Coincident(g194,g195)
    c: Coincident(g195,g196)
    c: Coincident(g196,g197)
    c: Coincident(g197,g198)
    c: Coincident(g198,g199)
    c: Coincident(g199,g200)
    c: Coincident(g200,g201)
    c: Coincident(g201,g202)
    c: Coincident(g202,g203)
    c: Coincident(g203,g204)
    c: Coincident(g204,g205)
    c: Coincident(g205,g206)
    c: Coincident(g206,g207)
    c: Coincident(g207,g208)
    c: Coincident(g208,g209)
    c: Coincident(g0,g210)
    c: Coincident(g0,g-1)
    c: Coincident(g209,g210)
FEATURE [PartDesign::Pad] Pad007
  Length = 3
  Length2 = 100
  Placement = pos=(0,0,0) rot=(0.57735,0.57735,0.57735;2.0944rad)
  Profile = -> Sketch008
  Type = 0
FEATURE [PartDesign::PolarPattern] PolarPattern008
  Angle = 360
  Axis = -> Sketch008 [N_Axis]
  BaseFeature = -> Pad007
  Occurrences = 4
  Originals = -> [Pad007]
  Placement = pos=(0,0,0) rot=(0.57735,0.57735,0.57735;2.0944rad)
FEATURE [PartDesign::Body] Body007
  Group = -> [Sketch008,Pad007,PolarPattern008]
  Origin = -> Origin006
  Tip = -> PolarPattern008
FEATURE [Part::Cut] Cut002
  Base = -> Body007
  Placement = pos=(-45,0,1) rot=(0,0,1;0rad)
  Tool = -> Body008
FEATURE [Part::MultiFuse] Fusion001
  Placement = pos=(-64,0,0) rot=(0,0,1;0rad)
  Shapes = -> [Cut003,Cylinder001,Cut002]
FEATURE [App::MeasureDistance] Distance001  label="Distance: 16,00 mm"
  Distance = 16
  P1 = (-45,-17.7439,19.418)
  P2 = (-61,-17.7439,19.418)
FEATURE [Sketcher::SketchObject] Sketch009
  MapMode = 5
  Placement = pos=(0,0,0) rot=(0.57735,0.57735,0.57735;2.0944rad)
  Support = -> [YZ_Plane009]
  sketch-geometry (20):
    g0: LineSegment StartX=1.84977 StartY=-2.03462 StartZ=0 EndX=1.64219 EndY=-2.20542 EndZ=0
    g1: LineSegment StartX=1.64219 StartY=-2.20542 StartZ=0 EndX=1.4178 EndY=-2.35642 EndZ=0
    g2: LineSegment StartX=1.4178 StartY=-2.35642 StartZ=0 EndX=1.1786 EndY=-2.48192 EndZ=0
    g3: LineSegment StartX=1.1786 StartY=-2.48192 StartZ=0 EndX=0.933165 EndY=-2.58946 EndZ=0
    g4: LineSegment StartX=0.933165 StartY=-2.58946 StartZ=0 EndX=0.669297 EndY=-2.66615 EndZ=0
    g5: LineSegment StartX=0.669297 StartY=-2.66615 StartZ=0 EndX=0.401357 EndY=-2.72007 EndZ=0
    g6: LineSegment StartX=0.401357 StartY=-2.72007 StartZ=0 EndX=0.133198 EndY=-2.74689 EndZ=0
    g7: LineSegment StartX=0.133198 StartY=-2.74689 StartZ=0 EndX=-0.13715 EndY=-2.74708 EndZ=0
    g8: LineSegment StartX=-0.13715 StartY=-2.74708 StartZ=0 EndX=-0.688499 EndY=-2.66151 EndZ=0
    g9: LineSegment StartX=-0.688499 StartY=-2.66151 StartZ=0 EndX=-0.94393 EndY=-2.58392 EndZ=0
    g10: LineSegment StartX=-0.94393 StartY=-2.58392 StartZ=0 EndX=-1.18786 EndY=-2.4818 EndZ=0
    g11: LineSegment StartX=-1.18786 StartY=-2.4818 StartZ=0 EndX=-1.42897 EndY=-2.34335 EndZ=0
    g12: LineSegment StartX=-1.42897 StartY=-2.34335 StartZ=0 EndX=-1.64859 EndY=-2.19653 EndZ=0
    g13: LineSegment StartX=-1.64859 StartY=-2.19653 StartZ=0 EndX=-1.84554 EndY=-2.0342 EndZ=0
    g14: LineSegment StartX=-1.84554 StartY=-2.0342 StartZ=0 EndX=-1.84465 EndY=-1.22163 EndZ=0
    g15: LineSegment StartX=-1.84465 StartY=-1.22163 StartZ=0 EndX=-1.84999 EndY=-0.000151 EndZ=0
    g16: LineSegment StartX=-1.84999 StartY=-0.000151 StartZ=0 EndX=-1.85002 EndY=0.00099 EndZ=0
    g17: LineSegment StartX=-1.85002 StartY=0.00099 StartZ=0 EndX=1.85015 EndY=0.005067 EndZ=0
    g18: LineSegment StartX=1.84931 StartY=-2.02283 StartZ=0 EndX=1.84977 EndY=-2.03462 EndZ=0
    g19: LineSegment StartX=1.85015 StartY=0.005067 StartZ=0 EndX=1.84931 EndY=-2.02283 EndZ=0
  constraints (20):
    c: Coincident(g0,g1)
    c: Coincident(g1,g2)
    c: Coincident(g2,g3)
    c: Coincident(g3,g4)
    c: Coincident(g4,g5)
    c: Coincident(g5,g6)
    c: Coincident(g8,g9)
    c: Coincident(g9,g10)
    c: Coincident(g10,g11)
    c: Coincident(g11,g12)
    c: Coincident(g12,g13)
    c: Coincident(g13,g14)
    c: Coincident(g14,g15)
    c: Coincident(g15,g16)
    c: Coincident(g16,g17)
    c: Coincident(g0,g18)
    c: Coincident(g7,g8)
    c: Coincident(g6,g7)
    c: Coincident(g18,g19)
    c: Coincident(g17,g19)
FEATURE [PartDesign::Pad] Pad009
  Length = 100
  Length2 = 100
  Midplane = true
  Placement = pos=(0,0,0) rot=(0.57735,0.57735,0.57735;2.0944rad)
  Profile = -> Sketch009
  Type = 0
FEATURE [PartDesign::PolarPattern] PolarPattern009
  Angle = 360
  Axis = -> Sketch009 [N_Axis]
  BaseFeature = -> Pad009
  Occurrences = 2
  Originals = -> [Pad009]
  Placement = pos=(0,0,0) rot=(0.57735,0.57735,0.57735;2.0944rad)
FEATURE [PartDesign::Body] Body009
  Group = -> [Sketch009,Pad009,PolarPattern009]
  Origin = -> Origin009
  Placement = pos=(-99,0,1) rot=(0,0,1;0rad)
  Tip = -> PolarPattern009
FEATURE [Sketcher::SketchObject] Sketch010
  MapMode = 5
  Placement = pos=(0,0,0) rot=(0.57735,0.57735,0.57735;2.0944rad)
  Support = -> [YZ_Plane010]
  sketch-geometry (20):
    g0: LineSegment StartX=1.84977 StartY=-2.03462 StartZ=0 EndX=1.64219 EndY=-2.20542 EndZ=0
    g1: LineSegment StartX=1.64219 StartY=-2.20542 StartZ=0 EndX=1.4178 EndY=-2.35642 EndZ=0
    g2: LineSegment StartX=1.4178 StartY=-2.35642 StartZ=0 EndX=1.1786 EndY=-2.48192 EndZ=0
    g3: LineSegment StartX=1.1786 StartY=-2.48192 StartZ=0 EndX=0.933165 EndY=-2.58946 EndZ=0
    g4: LineSegment StartX=0.933165 StartY=-2.58946 StartZ=0 EndX=0.669297 EndY=-2.66615 EndZ=0
    g5: LineSegment StartX=0.669297 StartY=-2.66615 StartZ=0 EndX=0.401357 EndY=-2.72007 EndZ=0
    g6: LineSegment StartX=0.401357 StartY=-2.72007 StartZ=0 EndX=0.133198 EndY=-2.74689 EndZ=0
    g7: LineSegment StartX=0.133198 StartY=-2.74689 StartZ=0 EndX=-0.13715 EndY=-2.74708 EndZ=0
    g8: LineSegment StartX=-0.13715 StartY=-2.74708 StartZ=0 EndX=-0.688499 EndY=-2.66151 EndZ=0
    g9: LineSegment StartX=-0.688499 StartY=-2.66151 StartZ=0 EndX=-0.94393 EndY=-2.58392 EndZ=0
    g10: LineSegment StartX=-0.94393 StartY=-2.58392 StartZ=0 EndX=-1.18786 EndY=-2.4818 EndZ=0
    g11: LineSegment StartX=-1.18786 StartY=-2.4818 StartZ=0 EndX=-1.42897 EndY=-2.34335 EndZ=0
    g12: LineSegment StartX=-1.42897 StartY=-2.34335 StartZ=0 EndX=-1.64859 EndY=-2.19653 EndZ=0
    g13: LineSegment StartX=-1.64859 StartY=-2.19653 StartZ=0 EndX=-1.84554 EndY=-2.0342 EndZ=0
    g14: LineSegment StartX=-1.84554 StartY=-2.0342 StartZ=0 EndX=-1.84465 EndY=-1.22163 EndZ=0
    g15: LineSegment StartX=-1.84465 StartY=-1.22163 StartZ=0 EndX=-1.84999 EndY=-0.000151 EndZ=0
    g16: LineSegment StartX=-1.84999 StartY=-0.000151 StartZ=0 EndX=-1.85002 EndY=0.00099 EndZ=0
    g17: LineSegment StartX=-1.85002 StartY=0.00099 StartZ=0 EndX=1.85015 EndY=0.005067 EndZ=0
    g18: LineSegment StartX=1.84931 StartY=-2.02283 StartZ=0 EndX=1.84977 EndY=-2.03462 EndZ=0
    g19: LineSegment StartX=1.85015 StartY=0.005067 StartZ=0 EndX=1.84931 EndY=-2.02283 EndZ=0
  constraints (20):
    c: Coincident(g0,g1)
    c: Coincident(g1,g2)
    c: Coincident(g2,g3)
    c: Coincident(g3,g4)
    c: Coincident(g4,g5)
    c: Coincident(g5,g6)
    c: Coincident(g8,g9)
    c: Coincident(g9,g10)
    c: Coincident(g10,g11)
    c: Coincident(g11,g12)
    c: Coincident(g12,g13)
    c: Coincident(g13,g14)
    c: Coincident(g14,g15)
    c: Coincident(g15,g16)
    c: Coincident(g16,g17)
    c: Coincident(g0,g18)
    c: Coincident(g7,g8)
    c: Coincident(g6,g7)
    c: Coincident(g18,g19)
    c: Coincident(g17,g19)
FEATURE [PartDesign::Pad] Pad010
  Length = 100
  Length2 = 100
  Midplane = true
  Placement = pos=(0,0,0) rot=(0.57735,0.57735,0.57735;2.0944rad)
  Profile = -> Sketch010
  Type = 0
FEATURE [PartDesign::PolarPattern] PolarPattern010
  Angle = 360
  Axis = -> Sketch010 [N_Axis]
  BaseFeature = -> Pad010
  Occurrences = 2
  Originals = -> [Pad010]
  Placement = pos=(0,0,0) rot=(0.57735,0.57735,0.57735;2.0944rad)
FEATURE [PartDesign::Body] Body010
  Group = -> [Sketch010,Pad010,PolarPattern010]
  Origin = -> Origin010
  Placement = pos=(-99,51,1) rot=(0,0,1;0rad)
  Tip = -> PolarPattern010
FEATURE [Part::Cut] Cut005
  Base = -> Fusion001
  Tool = -> Body009
FEATURE [Part::Cylinder] Cylinder002  label="Цилиндр002"
  Angle = 360
  AttacherType = Attacher::AttachEngine3D
  Height = 36
  Placement = pos=(-2.98716,0,0.971139) rot=(0,-1,0;1.55334rad)
  Radius = 10
FEATURE [Part::Cylinder] Cylinder003  label="Цилиндр003"
  Angle = 360
  AttacherType = Attacher::AttachEngine3D
  Height = 36
  Placement = pos=(-66.99,0,0.971139) rot=(0,-1,0;1.55334rad)
  Radius = 10
FEATURE [Part::Cut] Cut006
  Base = -> Cut005
  Tool = -> Cylinder003
FEATURE [Part::Cylinder] Cylinder004  label="Цилиндр004"
  Angle = 360
  AttacherType = Attacher::AttachEngine3D
  Height = 18
  Placement = pos=(-62.8,55,1) rot=(0,1,0;1.5708rad)
  Radius = 5
FEATURE [Part::Cylinder] Cylinder005  label="Цилиндр005"
  Angle = 360
  AttacherType = Attacher::AttachEngine3D
  Height = 18
  Placement = pos=(-62.8,55,1) rot=(0,1,0;1.5708rad)
  Radius = 15
FEATURE [Part::Cut] Cut008
  Base = -> Cylinder005
  Placement = pos=(0,-55,0) rot=(0,0,1;0rad)
  Tool = -> Cylinder004
FEATURE [Sketcher::SketchObject] Sketch013
  MapMode = 5
  Placement = pos=(0,0,0) rot=(0.57735,0.57735,0.57735;2.0944rad)
  Support = -> [YZ_Plane014]
  sketch-geometry (211):
    g0: LineSegment StartX=0 StartY=0 StartZ=0 EndX=23.0775 EndY=-0.007725 EndZ=0
    g1: LineSegment StartX=23.0775 StartY=-0.007725 StartZ=0 EndX=23.0915 EndY=0.254478 EndZ=0
    g2: LineSegment StartX=23.0915 StartY=0.254478 StartZ=0 EndX=23.1284 EndY=0.508391 EndZ=0
    g3: LineSegment StartX=23.1284 StartY=0.508391 StartZ=0 EndX=23.1869 EndY=0.740712 EndZ=0
    g4: LineSegment StartX=23.1869 StartY=0.740712 StartZ=0 EndX=23.2782 EndY=0.973565 EndZ=0
    g5: LineSegment StartX=23.2782 StartY=0.973565 StartZ=0 EndX=23.3963 EndY=1.22031 EndZ=0
    g6: LineSegment StartX=23.3963 StartY=1.22031 StartZ=0 EndX=23.5215 EndY=1.42239 EndZ=0
    g7: LineSegment StartX=23.5215 StartY=1.42239 StartZ=0 EndX=23.6745 EndY=1.62203 EndZ=0
    g8: LineSegment StartX=23.6745 StartY=1.62203 StartZ=0 EndX=23.8622 EndY=1.81795 EndZ=0
    g9: LineSegment StartX=23.8622 StartY=1.81795 StartZ=0 EndX=24.0428 EndY=1.97182 EndZ=0
    g10: LineSegment StartX=24.0428 StartY=1.97182 StartZ=0 EndX=24.2535 EndY=2.11914 EndZ=0
    g11: LineSegment StartX=24.2535 StartY=2.11914 StartZ=0 EndX=24.4771 EndY=2.24429 EndZ=0
    g12: LineSegment StartX=24.4771 StartY=2.24429 StartZ=0 EndX=24.7643 EndY=2.36841 EndZ=0
    g13: LineSegment StartX=24.7643 StartY=2.36841 StartZ=0 EndX=24.8553 EndY=2.41105 EndZ=0
    g14: LineSegment StartX=24.8553 StartY=2.41105 StartZ=0 EndX=24.9955 EndY=2.50386 EndZ=0
    g15: LineSegment StartX=24.9955 StartY=2.50386 StartZ=0 EndX=25.1151 EndY=2.62736 EndZ=0
    g16: LineSegment StartX=25.1151 StartY=2.62736 StartZ=0 EndX=25.2142 EndY=2.76003 EndZ=0
    g17: LineSegment StartX=25.2142 StartY=2.76003 StartZ=0 EndX=25.2969 EndY=2.93426 EndZ=0
    g18: LineSegment StartX=25.2969 StartY=2.93426 StartZ=0 EndX=25.3426 EndY=3.08419 EndZ=0
    g19: LineSegment StartX=25.3426 StartY=3.08419 StartZ=0 EndX=25.3551 EndY=3.24413 EndZ=0
    g20: LineSegment StartX=25.3551 StartY=3.24413 StartZ=0 EndX=25.349 EndY=3.41794 EndZ=0
    g21: LineSegment StartX=25.349 StartY=3.41794 StartZ=0 EndX=25.3326 EndY=3.53796 EndZ=0
    g22: LineSegment StartX=25.3326 StartY=3.53796 StartZ=0 EndX=25.2546 EndY=4.05249 EndZ=0
    g23: LineSegment StartX=25.2546 StartY=4.05249 StartZ=0 EndX=25.1642 EndY=4.58451 EndZ=0
    g24: LineSegment StartX=25.1642 StartY=4.58451 StartZ=0 EndX=25.1211 EndY=4.74519 EndZ=0
    g25: LineSegment StartX=25.1211 StartY=4.74519 StartZ=0 EndX=25.0493 EndY=4.90009 EndZ=0
    g26: LineSegment StartX=25.0493 StartY=4.90009 StartZ=0 EndX=24.9559 EndY=5.03652 EndZ=0
    g27: LineSegment StartX=24.9559 StartY=5.03652 StartZ=0 EndX=24.8359 EndY=5.16166 EndZ=0
    g28: LineSegment StartX=24.8359 StartY=5.16166 StartZ=0 EndX=24.7064 EndY=5.26066 EndZ=0
    g29: LineSegment StartX=24.7064 StartY=5.26066 StartZ=0 EndX=24.5515 EndY=5.33657 EndZ=0
    g30: LineSegment StartX=24.5515 StartY=5.33657 StartZ=0 EndX=24.3854 EndY=5.38889 EndZ=0
    g31: LineSegment StartX=24.3854 StartY=5.38889 StartZ=0 EndX=23.9661 EndY=5.429 EndZ=0
    g32: LineSegment StartX=23.9661 StartY=5.429 StartZ=0 EndX=23.7168 EndY=5.47721 EndZ=0
    g33: LineSegment StartX=23.7168 StartY=5.47721 StartZ=0 EndX=23.4789 EndY=5.55004 EndZ=0
    g34: LineSegment StartX=23.4789 StartY=5.55004 StartZ=0 EndX=23.244 EndY=5.64749 EndZ=0
    g35: LineSegment StartX=23.244 StartY=5.64749 StartZ=0 EndX=23.0141 EndY=5.77459 EndZ=0
    g36: LineSegment StartX=23.0141 StartY=5.77459 StartZ=0 EndX=22.81 EndY=5.91307 EndZ=0
    g37: LineSegment StartX=22.81 StartY=5.91307 StartZ=0 EndX=22.6171 EndY=6.07925 EndZ=0
    g38: LineSegment StartX=22.6171 StartY=6.07925 StartZ=0 EndX=22.4499 EndY=6.25158 EndZ=0
    g39: LineSegment StartX=22.4499 StartY=6.25158 StartZ=0 EndX=22.2897 EndY=6.45644 EndZ=0
    g40: LineSegment StartX=22.2897 StartY=6.45644 StartZ=0 EndX=22.1484 EndY=6.67133 EndZ=0
    g41: LineSegment StartX=22.1484 StartY=6.67133 StartZ=0 EndX=22.0413 EndY=6.89628 EndZ=0
    g42: LineSegment StartX=22.0413 StartY=6.89628 StartZ=0 EndX=21.9449 EndY=7.13041 EndZ=0
    g43: LineSegment StartX=21.9449 StartY=7.13041 StartZ=0 EndX=21.883 EndY=7.36574 EndZ=0
    g44: LineSegment StartX=21.883 StartY=7.36574 StartZ=0 EndX=21.842 EndY=7.61808 EndZ=0
    g45: LineSegment StartX=21.842 StartY=7.61808 StartZ=0 EndX=21.8244 EndY=7.88752 EndZ=0
    g46: LineSegment StartX=21.8244 StartY=7.88752 StartZ=0 EndX=21.8388 EndY=8.12242 EndZ=0
    g47: LineSegment StartX=21.8388 StartY=8.12242 StartZ=0 EndX=21.8716 EndY=8.3765 EndZ=0
    g48: LineSegment StartX=21.8716 StartY=8.3765 StartZ=0 EndX=21.9322 EndY=8.62371 EndZ=0
    g49: LineSegment StartX=21.9322 StartY=8.62371 StartZ=0 EndX=22.0085 EndY=8.85622 EndZ=0
    g50: LineSegment StartX=22.0085 StartY=8.85622 StartZ=0 EndX=22.1095 EndY=9.0873 EndZ=0
    g51: LineSegment StartX=22.1095 StartY=9.0873 StartZ=0 EndX=22.2564 EndY=9.30001 EndZ=0
    g52: LineSegment StartX=22.2564 StartY=9.30001 StartZ=0 EndX=22.4222 EndY=9.51816 EndZ=0
    g53: LineSegment StartX=22.4222 StartY=9.51816 StartZ=0 EndX=22.5814 EndY=9.69568 EndZ=0
    g54: LineSegment StartX=22.5814 StartY=9.69568 StartZ=0 EndX=22.7773 EndY=9.86401 EndZ=0
    g55: LineSegment StartX=22.7773 StartY=9.86401 StartZ=0 EndX=22.8829 EndY=9.96654 EndZ=0
    g56: LineSegment StartX=22.8829 StartY=9.96654 StartZ=0 EndX=22.9946 EndY=10.1027 EndZ=0
    g57: LineSegment StartX=22.9946 StartY=10.1027 StartZ=0 EndX=23.0728 EndY=10.2473 EndZ=0
    g58: LineSegment StartX=23.0728 StartY=10.2473 StartZ=0 EndX=23.1295 EndY=10.4111 EndZ=0
    g59: LineSegment StartX=23.1295 StartY=10.4111 StartZ=0 EndX=23.1555 EndY=10.5871 EndZ=0
    g60: LineSegment StartX=23.1555 StartY=10.5871 StartZ=0 EndX=23.1416 EndY=10.7621 EndZ=0
    g61: LineSegment StartX=23.1416 StartY=10.7621 StartZ=0 EndX=23.1095 EndY=10.9289 EndZ=0
    g62: LineSegment StartX=23.1095 StartY=10.9289 StartZ=0 EndX=23.0483 EndY=11.0865 EndZ=0
    g63: LineSegment StartX=23.0483 StartY=11.0865 StartZ=0 EndX=22.8718 EndY=11.4442 EndZ=0
    g64: LineSegment StartX=22.8718 StartY=11.4442 StartZ=0 EndX=22.5688 EndY=12.0257 EndZ=0
    g65: LineSegment StartX=22.5688 StartY=12.0257 StartZ=0 EndX=22.5075 EndY=12.152 EndZ=0
    g66: LineSegment StartX=22.5075 StartY=12.152 StartZ=0 EndX=22.4248 EndY=12.279 EndZ=0
    g67: LineSegment StartX=22.4248 StartY=12.279 StartZ=0 EndX=22.3208 EndY=12.3999 EndZ=0
    g68: LineSegment StartX=22.3208 StartY=12.3999 StartZ=0 EndX=22.1769 EndY=12.5009 EndZ=0
    g69: LineSegment StartX=22.1769 StartY=12.5009 StartZ=0 EndX=22.0254 EndY=12.5805 EndZ=0
    g70: LineSegment StartX=22.0254 StartY=12.5805 StartZ=0 EndX=21.8678 EndY=12.6325 EndZ=0
    g71: LineSegment StartX=21.8678 StartY=12.6325 StartZ=0 EndX=21.6949 EndY=12.6601 EndZ=0
    g72: LineSegment StartX=21.6949 StartY=12.6601 StartZ=0 EndX=21.5327 EndY=12.6555 EndZ=0
    g73: LineSegment StartX=21.5327 StartY=12.6555 StartZ=0 EndX=21.1061 EndY=12.5612 EndZ=0
    g74: LineSegment StartX=21.1061 StartY=12.5612 StartZ=0 EndX=20.8582 EndY=12.5352 EndZ=0
    g75: LineSegment StartX=20.8582 StartY=12.5352 StartZ=0 EndX=20.6087 EndY=12.5337 EndZ=0
    g76: LineSegment StartX=20.6087 StartY=12.5337 StartZ=0 EndX=20.3501 EndY=12.5536 EndZ=0
    g77: LineSegment StartX=20.3501 StartY=12.5536 StartZ=0 EndX=20.0854 EndY=12.5979 EndZ=0
    g78: LineSegment StartX=20.0854 StartY=12.5979 StartZ=0 EndX=19.8665 EndY=12.6699 EndZ=0
    g79: LineSegment StartX=19.8665 StartY=12.6699 StartZ=0 EndX=19.614 EndY=12.7678 EndZ=0
    g80: LineSegment StartX=19.614 StartY=12.7678 StartZ=0 EndX=19.4105 EndY=12.881 EndZ=0
    g81: LineSegment StartX=19.4105 StartY=12.881 StartZ=0 EndX=19.1993 EndY=13.0264 EndZ=0
    g82: LineSegment StartX=19.1993 StartY=13.0264 StartZ=0 EndX=18.9927 EndY=13.2018 EndZ=0
    g83: LineSegment StartX=18.9927 StartY=13.2018 StartZ=0 EndX=18.8259 EndY=13.3625 EndZ=0
    g84: LineSegment StartX=18.8259 StartY=13.3625 StartZ=0 EndX=18.6714 EndY=13.5553 EndZ=0
    g85: LineSegment StartX=18.6714 StartY=13.5553 StartZ=0 EndX=18.5367 EndY=13.768 EndZ=0
    g86: LineSegment StartX=18.5367 StartY=13.768 StartZ=0 EndX=18.4051 EndY=14.0083 EndZ=0
    g87: LineSegment StartX=18.4051 StartY=14.0083 StartZ=0 EndX=18.3225 EndY=14.2255 EndZ=0
    g88: LineSegment StartX=18.3225 StartY=14.2255 StartZ=0 EndX=18.2506 EndY=14.4903 EndZ=0
    g89: LineSegment StartX=18.2506 StartY=14.4903 StartZ=0 EndX=18.2154 EndY=14.7183 EndZ=0
    g90: LineSegment StartX=18.2154 StartY=14.7183 StartZ=0 EndX=18.2017 EndY=14.9876 EndZ=0
    g91: LineSegment StartX=18.2017 StartY=14.9876 StartZ=0 EndX=18.1828 EndY=15.2236 EndZ=0
    g92: LineSegment StartX=18.1828 StartY=15.2236 StartZ=0 EndX=18.2304 EndY=15.4722 EndZ=0
    g93: LineSegment StartX=18.2304 StartY=15.4722 StartZ=0 EndX=18.2815 EndY=15.714 EndZ=0
    g94: LineSegment StartX=18.2815 StartY=15.714 StartZ=0 EndX=18.3735 EndY=15.9865 EndZ=0
    g95: LineSegment StartX=18.3735 StartY=15.9865 StartZ=0 EndX=18.4796 EndY=16.216 EndZ=0
    g96: LineSegment StartX=18.4796 StartY=16.216 StartZ=0 EndX=18.6771 EndY=16.5429 EndZ=0
    g97: LineSegment StartX=18.6771 StartY=16.5429 StartZ=0 EndX=18.7452 EndY=16.7132 EndZ=0
    g98: LineSegment StartX=18.7452 StartY=16.7132 StartZ=0 EndX=18.7725 EndY=16.8562 EndZ=0
    g99: LineSegment StartX=18.7725 StartY=16.8562 StartZ=0 EndX=18.7793 EndY=17.0538 EndZ=0
    g100: LineSegment StartX=18.7793 StartY=17.0538 StartZ=0 EndX=18.7515 EndY=17.1989 EndZ=0
    g101: LineSegment StartX=18.7515 StartY=17.1989 StartZ=0 EndX=18.7073 EndY=17.3454 EndZ=0
    g102: LineSegment StartX=18.7073 StartY=17.3454 StartZ=0 EndX=18.6221 EndY=17.4986 EndZ=0
    g103: LineSegment StartX=18.6221 StartY=17.4986 StartZ=0 EndX=18.5404 EndY=17.6076 EndZ=0
    g104: LineSegment StartX=18.5404 StartY=17.6076 StartZ=0 EndX=18.4484 EndY=17.7132 EndZ=0
    g105: LineSegment StartX=18.4484 StartY=17.7132 StartZ=0 EndX=17.7843 EndY=18.3841 EndZ=0
    g106: LineSegment StartX=17.7843 StartY=18.3841 StartZ=0 EndX=17.6004 EndY=18.5476 EndZ=0
    g107: LineSegment StartX=17.6004 StartY=18.5476 StartZ=0 EndX=17.5187 EndY=18.6089 EndZ=0
    g108: LineSegment StartX=17.5187 StartY=18.6089 StartZ=0 EndX=17.3654 EndY=18.6872 EndZ=0
    g109: LineSegment StartX=17.3654 StartY=18.6872 StartZ=0 EndX=17.2156 EndY=18.7383 EndZ=0
    g110: LineSegment StartX=17.2156 StartY=18.7383 StartZ=0 EndX=17.0487 EndY=18.7621 EndZ=0
    g111: LineSegment StartX=17.0487 StartY=18.7621 StartZ=0 EndX=16.8852 EndY=18.7724 EndZ=0
    g112: LineSegment StartX=16.8852 StartY=18.7724 StartZ=0 EndX=16.7183 EndY=18.7417 EndZ=0
    g113: LineSegment StartX=16.7183 StartY=18.7417 StartZ=0 EndX=16.5651 EndY=18.694 EndZ=0
    g114: LineSegment StartX=16.5651 StartY=18.694 StartZ=0 EndX=16.3709 EndY=18.5851 EndZ=0
    g115: LineSegment StartX=16.3709 StartY=18.5851 StartZ=0 EndX=16.1496 EndY=18.4522 EndZ=0
    g116: LineSegment StartX=16.1496 StartY=18.4522 StartZ=0 EndX=15.9752 EndY=18.3739 EndZ=0
    g117: LineSegment StartX=15.9752 StartY=18.3739 StartZ=0 EndX=15.7423 EndY=18.2963 EndZ=0
    g118: LineSegment StartX=15.7423 StartY=18.2963 StartZ=0 EndX=15.5003 EndY=18.2233 EndZ=0
    g119: LineSegment StartX=15.5003 StartY=18.2233 StartZ=0 EndX=15.2492 EndY=18.1982 EndZ=0
    g120: LineSegment StartX=15.2492 StartY=18.1982 StartZ=0 EndX=14.973 EndY=18.2004 EndZ=0
    g121: LineSegment StartX=14.973 StartY=18.2004 StartZ=0 EndX=14.7241 EndY=18.2141 EndZ=0
    g122: LineSegment StartX=14.7241 StartY=18.2141 StartZ=0 EndX=14.4685 EndY=18.2484 EndZ=0
    g123: LineSegment StartX=14.4685 StartY=18.2484 StartZ=0 EndX=14.2265 EndY=18.3192 EndZ=0
    g124: LineSegment StartX=14.2265 StartY=18.3192 StartZ=0 EndX=13.9799 EndY=18.4196 EndZ=0
    g125: LineSegment StartX=13.9799 StartY=18.4196 StartZ=0 EndX=13.7736 EndY=18.5304 EndZ=0
    g126: LineSegment StartX=13.7736 StartY=18.5304 StartZ=0 EndX=13.5557 EndY=18.6666 EndZ=0
    g127: LineSegment StartX=13.5557 StartY=18.6666 StartZ=0 EndX=13.3683 EndY=18.8267 EndZ=0
    g128: LineSegment StartX=13.3683 StartY=18.8267 StartZ=0 EndX=13.1844 EndY=18.997 EndZ=0
    g129: LineSegment StartX=13.1844 StartY=18.997 StartZ=0 EndX=13.0175 EndY=19.2047 EndZ=0
    g130: LineSegment StartX=13.0175 StartY=19.2047 StartZ=0 EndX=12.9086 EndY=19.4227 EndZ=0
    g131: LineSegment StartX=12.9086 StartY=19.4227 StartZ=0 EndX=12.694 EndY=19.8518 EndZ=0
    g132: LineSegment StartX=12.694 StartY=19.8518 StartZ=0 EndX=12.5986 EndY=20.1266 EndZ=0
    g133: LineSegment StartX=12.5986 StartY=20.1266 StartZ=0 EndX=12.5373 EndY=20.3616 EndZ=0
    g134: LineSegment StartX=12.5373 StartY=20.3616 StartZ=0 EndX=12.5305 EndY=20.6613 EndZ=0
    g135: LineSegment StartX=12.5305 StartY=20.6613 StartZ=0 EndX=12.527 EndY=20.852 EndZ=0
    g136: LineSegment StartX=12.527 StartY=20.852 StartZ=0 EndX=12.5713 EndY=21.1177 EndZ=0
    g137: LineSegment StartX=12.5713 StartY=21.1177 StartZ=0 EndX=12.6565 EndY=21.5025 EndZ=0
    g138: LineSegment StartX=12.6565 StartY=21.5025 StartZ=0 EndX=12.6531 EndY=21.7205 EndZ=0
    g139: LineSegment StartX=12.6531 StartY=21.7205 StartZ=0 EndX=12.6258 EndY=21.8771 EndZ=0
    g140: LineSegment StartX=12.6258 StartY=21.8771 StartZ=0 EndX=12.5747 EndY=22.0542 EndZ=0
    g141: LineSegment StartX=12.5747 StartY=22.0542 StartZ=0 EndX=12.5027 EndY=22.1813 EndZ=0
    g142: LineSegment StartX=12.5027 StartY=22.1813 StartZ=0 EndX=12.3937 EndY=22.3278 EndZ=0
    g143: LineSegment StartX=12.3937 StartY=22.3278 StartZ=0 EndX=12.278 EndY=22.4299 EndZ=0
    g144: LineSegment StartX=12.278 StartY=22.4299 StartZ=0 EndX=12.1179 EndY=22.5287 EndZ=0
    g145: LineSegment StartX=12.1179 StartY=22.5287 StartZ=0 EndX=11.7535 EndY=22.716 EndZ=0
    g146: LineSegment StartX=11.7535 StartY=22.716 StartZ=0 EndX=11.2792 EndY=22.9552 EndZ=0
    g147: LineSegment StartX=11.2792 StartY=22.9552 StartZ=0 EndX=11.0374 EndY=23.0607 EndZ=0
    g148: LineSegment StartX=11.0374 StartY=23.0607 StartZ=0 EndX=10.8875 EndY=23.1289 EndZ=0
    g149: LineSegment StartX=10.8875 StartY=23.1289 StartZ=0 EndX=10.7036 EndY=23.1527 EndZ=0
    g150: LineSegment StartX=10.7036 StartY=23.1527 StartZ=0 EndX=10.5571 EndY=23.1391 EndZ=0
    g151: LineSegment StartX=10.5571 StartY=23.1391 StartZ=0 EndX=10.38 EndY=23.1084 EndZ=0
    g152: LineSegment StartX=10.38 StartY=23.1084 StartZ=0 EndX=10.2643 EndY=23.0641 EndZ=0
    g153: LineSegment StartX=10.2643 StartY=23.0641 StartZ=0 EndX=10.1042 EndY=22.9892 EndZ=0
    g154: LineSegment StartX=10.1042 StartY=22.9892 StartZ=0 EndX=9.97817 EndY=22.9041 EndZ=0
    g155: LineSegment StartX=9.97817 StartY=22.9041 StartZ=0 EndX=9.8181 EndY=22.727 EndZ=0
    g156: LineSegment StartX=9.8181 StartY=22.727 StartZ=0 EndX=9.68528 EndY=22.5839 EndZ=0
    g157: LineSegment StartX=9.68528 StartY=22.5839 StartZ=0 EndX=9.5184 EndY=22.4068 EndZ=0
    g158: LineSegment StartX=9.5184 StartY=22.4068 StartZ=0 EndX=9.29702 EndY=22.2672 EndZ=0
    g159: LineSegment StartX=9.29702 StartY=22.2672 StartZ=0 EndX=9.09042 EndY=22.1273 EndZ=0
    g160: LineSegment StartX=9.09042 StartY=22.1273 StartZ=0 EndX=8.85883 EndY=22.0183 EndZ=0
    g161: LineSegment StartX=8.85883 StartY=22.0183 StartZ=0 EndX=8.60681 EndY=21.9332 EndZ=0
    g162: LineSegment StartX=8.60681 StartY=21.9332 StartZ=0 EndX=8.36841 EndY=21.8719 EndZ=0
    g163: LineSegment StartX=8.36841 StartY=21.8719 StartZ=0 EndX=8.11979 EndY=21.8344 EndZ=0
    g164: LineSegment StartX=8.11979 StartY=21.8344 StartZ=0 EndX=7.84392 EndY=21.8242 EndZ=0
    g165: LineSegment StartX=7.84392 StartY=21.8242 StartZ=0 EndX=7.61915 EndY=21.8446 EndZ=0
    g166: LineSegment StartX=7.61915 StartY=21.8446 StartZ=0 EndX=7.39096 EndY=21.8753 EndZ=0
    g167: LineSegment StartX=7.39096 StartY=21.8753 StartZ=0 EndX=7.10488 EndY=21.9536 EndZ=0
    g168: LineSegment StartX=7.10488 StartY=21.9536 StartZ=0 EndX=6.8801 EndY=22.0387 EndZ=0
    g169: LineSegment StartX=6.8801 StartY=22.0387 StartZ=0 EndX=6.66554 EndY=22.1613 EndZ=0
    g170: LineSegment StartX=6.66554 StartY=22.1613 StartZ=0 EndX=6.44417 EndY=22.2908 EndZ=0
    g171: LineSegment StartX=6.44417 StartY=22.2908 StartZ=0 EndX=6.19215 EndY=22.5087 EndZ=0
    g172: LineSegment StartX=6.19215 StartY=22.5087 StartZ=0 EndX=6.02186 EndY=22.6688 EndZ=0
    g173: LineSegment StartX=6.02186 StartY=22.6688 StartZ=0 EndX=5.87882 EndY=22.8391 EndZ=0
    g174: LineSegment StartX=5.87882 StartY=22.8391 StartZ=0 EndX=5.74259 EndY=23.0809 EndZ=0
    g175: LineSegment StartX=5.74259 StartY=23.0809 StartZ=0 EndX=5.62679 EndY=23.2989 EndZ=0
    g176: LineSegment StartX=5.62679 StartY=23.2989 StartZ=0 EndX=5.54923 EndY=23.4812 EndZ=0
    g177: LineSegment StartX=5.54923 StartY=23.4812 StartZ=0 EndX=5.48987 EndY=23.7141 EndZ=0
    g178: LineSegment StartX=5.48987 StartY=23.7141 StartZ=0 EndX=5.43965 EndY=23.931 EndZ=0
    g179: LineSegment StartX=5.43965 StartY=23.931 StartZ=0 EndX=5.38283 EndY=24.3702 EndZ=0
    g180: LineSegment StartX=5.38283 StartY=24.3702 StartZ=0 EndX=5.34402 EndY=24.5505 EndZ=0
    g181: LineSegment StartX=5.34402 StartY=24.5505 StartZ=0 EndX=5.26412 EndY=24.7012 EndZ=0
    g182: LineSegment StartX=5.26412 StartY=24.7012 StartZ=0 EndX=5.15662 EndY=24.8433 EndZ=0
    g183: LineSegment StartX=5.15662 StartY=24.8433 StartZ=0 EndX=5.03563 EndY=24.9643 EndZ=0
    g184: LineSegment StartX=5.03563 StartY=24.9643 StartZ=0 EndX=4.9055 EndY=25.0534 EndZ=0
    g185: LineSegment StartX=4.9055 StartY=25.0534 StartZ=0 EndX=4.76168 EndY=25.115 EndZ=0
    g186: LineSegment StartX=4.76168 StartY=25.115 StartZ=0 EndX=4.56991 EndY=25.1698 EndZ=0
    g187: LineSegment StartX=4.56991 StartY=25.1698 StartZ=0 EndX=4.22291 EndY=25.2269 EndZ=0
    g188: LineSegment StartX=4.22291 StartY=25.2269 StartZ=0 EndX=3.72501 EndY=25.306 EndZ=0
    g189: LineSegment StartX=3.72501 StartY=25.306 StartZ=0 EndX=3.40823 EndY=25.3504 EndZ=0
    g190: LineSegment StartX=3.40823 StartY=25.3504 StartZ=0 EndX=3.25674 EndY=25.3565 EndZ=0
    g191: LineSegment StartX=3.25674 StartY=25.3565 StartZ=0 EndX=3.08534 EndY=25.3351 EndZ=0
    g192: LineSegment StartX=3.08534 StartY=25.3351 StartZ=0 EndX=2.91854 EndY=25.2876 EndZ=0
    g193: LineSegment StartX=2.91854 StartY=25.2876 StartZ=0 EndX=2.76092 EndY=25.2111 EndZ=0
    g194: LineSegment StartX=2.76092 StartY=25.2111 StartZ=0 EndX=2.62472 EndY=25.1116 EndZ=0
    g195: LineSegment StartX=2.62472 StartY=25.1116 StartZ=0 EndX=2.50842 EndY=24.9984 EndZ=0
    g196: LineSegment StartX=2.50842 StartY=24.9984 StartZ=0 EndX=2.41174 EndY=24.8483 EndZ=0
    g197: LineSegment StartX=2.41174 StartY=24.8483 StartZ=0 EndX=2.30308 EndY=24.582 EndZ=0
    g198: LineSegment StartX=2.30308 StartY=24.582 StartZ=0 EndX=2.25622 EndY=24.4788 EndZ=0
    g199: LineSegment StartX=2.25622 StartY=24.4788 StartZ=0 EndX=2.13227 EndY=24.2646 EndZ=0
    g200: LineSegment StartX=2.13227 StartY=24.2646 StartZ=0 EndX=1.96394 EndY=24.0365 EndZ=0
    g201: LineSegment StartX=1.96394 StartY=24.0365 StartZ=0 EndX=1.80479 EndY=23.856 EndZ=0
    g202: LineSegment StartX=1.80479 StartY=23.856 StartZ=0 EndX=1.62573 EndY=23.6797 EndZ=0
    g203: LineSegment StartX=1.62573 StartY=23.6797 StartZ=0 EndX=1.41955 EndY=23.5197 EndZ=0
    g204: LineSegment StartX=1.41955 StartY=23.5197 StartZ=0 EndX=1.20904 EndY=23.3867 EndZ=0
    g205: LineSegment StartX=1.20904 StartY=23.3867 StartZ=0 EndX=0.984393 EndY=23.2759 EndZ=0
    g206: LineSegment StartX=0.984393 StartY=23.2759 StartZ=0 EndX=0.742307 EndY=23.1856 EndZ=0
    g207: LineSegment StartX=0.742307 StartY=23.1856 StartZ=0 EndX=0.498622 EndY=23.1238 EndZ=0
    g208: LineSegment StartX=0.498622 StartY=23.1238 StartZ=0 EndX=0.250381 EndY=23.0889 EndZ=0
    g209: LineSegment StartX=0.250381 StartY=23.0889 StartZ=0 EndX=-0.006065 EndY=23.0756 EndZ=0
    g210: LineSegment StartX=-0.006065 StartY=23.0756 StartZ=0 EndX=0 EndY=0 EndZ=0
  constraints (212):
    c: Coincident(g0,g1)
    c: Coincident(g1,g2)
    c: Coincident(g2,g3)
    c: Coincident(g3,g4)
    c: Coincident(g4,g5)
    c: Coincident(g5,g6)
    c: Coincident(g6,g7)
    c: Coincident(g7,g8)
    c: Coincident(g8,g9)
    c: Coincident(g9,g10)
    c: Coincident(g10,g11)
    c: Coincident(g11,g12)
    c: Coincident(g12,g13)
    c: Coincident(g13,g14)
    c: Coincident(g14,g15)
    c: Coincident(g15,g16)
    c: Coincident(g16,g17)
    c: Coincident(g17,g18)
    c: Coincident(g18,g19)
    c: Coincident(g19,g20)
    c: Coincident(g20,g21)
    c: Coincident(g21,g22)
    c: Coincident(g22,g23)
    c: Coincident(g23,g24)
    c: Coincident(g24,g25)
    c: Coincident(g25,g26)
    c: Coincident(g26,g27)
    c: Coincident(g27,g28)
    c: Coincident(g28,g29)
    c: Coincident(g29,g30)
    c: Coincident(g30,g31)
    c: Coincident(g31,g32)
    c: Coincident(g32,g33)
    c: Coincident(g33,g34)
    c: Coincident(g34,g35)
    c: Coincident(g35,g36)
    c: Coincident(g36,g37)
    c: Coincident(g37,g38)
    c: Coincident(g38,g39)
    c: Coincident(g39,g40)
    c: Coincident(g40,g41)
    c: Coincident(g41,g42)
    c: Coincident(g42,g43)
    c: Coincident(g43,g44)
    c: Coincident(g44,g45)
    c: Coincident(g45,g46)
    c: Coincident(g46,g47)
    c: Coincident(g47,g48)
    c: Coincident(g48,g49)
    c: Coincident(g49,g50)
    c: Coincident(g50,g51)
    c: Coincident(g51,g52)
    c: Coincident(g52,g53)
    c: Coincident(g53,g54)
    c: Coincident(g54,g55)
    c: Coincident(g55,g56)
    c: Coincident(g56,g57)
    c: Coincident(g57,g58)
    c: Coincident(g58,g59)
    c: Coincident(g59,g60)
    c: Coincident(g60,g61)
    c: Coincident(g61,g62)
    c: Coincident(g62,g63)
    c: Coincident(g63,g64)
    c: Coincident(g64,g65)
    c: Coincident(g65,g66)
    c: Coincident(g66,g67)
    c: Coincident(g67,g68)
    c: Coincident(g68,g69)
    c: Coincident(g69,g70)
    c: Coincident(g70,g71)
    c: Coincident(g71,g72)
    c: Coincident(g72,g73)
    c: Coincident(g73,g74)
    c: Coincident(g74,g75)
    c: Coincident(g75,g76)
    c: Coincident(g76,g77)
    c: Coincident(g77,g78)
    c: Coincident(g78,g79)
    c: Coincident(g79,g80)
    c: Coincident(g80,g81)
    c: Coincident(g81,g82)
    c: Coincident(g82,g83)
    c: Coincident(g83,g84)
    c: Coincident(g84,g85)
    c: Coincident(g85,g86)
    c: Coincident(g86,g87)
    c: Coincident(g87,g88)
    c: Coincident(g88,g89)
    c: Coincident(g89,g90)
    c: Coincident(g90,g91)
    c: Coincident(g91,g92)
    c: Coincident(g92,g93)
    c: Coincident(g93,g94)
    c: Coincident(g94,g95)
    c: Coincident(g95,g96)
    c: Coincident(g96,g97)
    c: Coincident(g97,g98)
    c: Coincident(g98,g99)
    c: Coincident(g99,g100)
    c: Coincident(g100,g101)
    c: Coincident(g101,g102)
    c: Coincident(g102,g103)
    c: Coincident(g103,g104)
    c: Coincident(g104,g105)
    c: Coincident(g105,g106)
    c: Coincident(g106,g107)
    c: Coincident(g107,g108)
    c: Coincident(g108,g109)
    c: Coincident(g109,g110)
    c: Coincident(g110,g111)
    c: Coincident(g111,g112)
    c: Coincident(g112,g113)
    c: Coincident(g113,g114)
    c: Coincident(g114,g115)
    c: Coincident(g115,g116)
    c: Coincident(g116,g117)
    c: Coincident(g117,g118)
    c: Coincident(g118,g119)
    c: Coincident(g119,g120)
    c: Coincident(g120,g121)
    c: Coincident(g121,g122)
    c: Coincident(g122,g123)
    c: Coincident(g123,g124)
    c: Coincident(g124,g125)
    c: Coincident(g125,g126)
    c: Coincident(g126,g127)
    c: Coincident(g127,g128)
    c: Coincident(g128,g129)
    c: Coincident(g129,g130)
    c: Coincident(g130,g131)
    c: Coincident(g131,g132)
    c: Coincident(g132,g133)
    c: Coincident(g133,g134)
    c: Coincident(g134,g135)
    c: Coincident(g135,g136)
    c: Coincident(g136,g137)
    c: Coincident(g137,g138)
    c: Coincident(g138,g139)
    c: Coincident(g139,g140)
    c: Coincident(g140,g141)
    c: Coincident(g141,g142)
    c: Coincident(g142,g143)
    c: Coincident(g143,g144)
    c: Coincident(g144,g145)
    c: Coincident(g145,g146)
    c: Coincident(g146,g147)
    c: Coincident(g147,g148)
    c: Coincident(g148,g149)
    c: Coincident(g149,g150)
    c: Coincident(g150,g151)
    c: Coincident(g151,g152)
    c: Coincident(g152,g153)
    c: Coincident(g153,g154)
    c: Coincident(g154,g155)
    c: Coincident(g155,g156)
    c: Coincident(g156,g157)
    c: Coincident(g157,g158)
    c: Coincident(g158,g159)
    c: Coincident(g159,g160)
    c: Coincident(g160,g161)
    c: Coincident(g161,g162)
    c: Coincident(g162,g163)
    c: Coincident(g163,g164)
    c: Coincident(g164,g165)
    c: Coincident(g165,g166)
    c: Coincident(g166,g167)
    c: Coincident(g167,g168)
    c: Coincident(g168,g169)
    c: Coincident(g169,g170)
    c: Coincident(g170,g171)
    c: Coincident(g171,g172)
    c: Coincident(g172,g173)
    c: Coincident(g173,g174)
    c: Coincident(g174,g175)
    c: Coincident(g175,g176)
    c: Coincident(g176,g177)
    c: Coincident(g177,g178)
    c: Coincident(g178,g179)
    c: Coincident(g179,g180)
    c: Coincident(g180,g181)
    c: Coincident(g181,g182)
    c: Coincident(g182,g183)
    c: Coincident(g183,g184)
    c: Coincident(g184,g185)
    c: Coincident(g185,g186)
    c: Coincident(g186,g187)
    c: Coincident(g187,g188)
    c: Coincident(g188,g189)
    c: Coincident(g189,g190)
    c: Coincident(g190,g191)
    c: Coincident(g191,g192)
    c: Coincident(g192,g193)
    c: Coincident(g193,g194)
    c: Coincident(g194,g195)
    c: Coincident(g195,g196)
    c: Coincident(g196,g197)
    c: Coincident(g197,g198)
    c: Coincident(g198,g199)
    c: Coincident(g199,g200)
    c: Coincident(g200,g201)
    c: Coincident(g201,g202)
    c: Coincident(g202,g203)
    c: Coincident(g203,g204)
    c: Coincident(g204,g205)
    c: Coincident(g205,g206)
    c: Coincident(g206,g207)
    c: Coincident(g207,g208)
    c: Coincident(g208,g209)
    c: Coincident(g0,g210)
    c: Coincident(g0,g-1)
    c: Coincident(g209,g210)
FEATURE [Sketcher::SketchObject] Sketch012
  MapMode = 5
  Placement = pos=(0,0,0) rot=(0.57735,0.57735,0.57735;2.0944rad)
  Support = -> [YZ_Plane014]
  sketch-geometry (20):
    g0: LineSegment StartX=1.84977 StartY=-2.03462 StartZ=0 EndX=1.64219 EndY=-2.20542 EndZ=0
    g1: LineSegment StartX=1.64219 StartY=-2.20542 StartZ=0 EndX=1.4178 EndY=-2.35642 EndZ=0
    g2: LineSegment StartX=1.4178 StartY=-2.35642 StartZ=0 EndX=1.1786 EndY=-2.48192 EndZ=0
    g3: LineSegment StartX=1.1786 StartY=-2.48192 StartZ=0 EndX=0.933165 EndY=-2.58946 EndZ=0
    g4: LineSegment StartX=0.933165 StartY=-2.58946 StartZ=0 EndX=0.669297 EndY=-2.66615 EndZ=0
    g5: LineSegment StartX=0.669297 StartY=-2.66615 StartZ=0 EndX=0.401357 EndY=-2.72007 EndZ=0
    g6: LineSegment StartX=0.401357 StartY=-2.72007 StartZ=0 EndX=0.133198 EndY=-2.74689 EndZ=0
    g7: LineSegment StartX=0.133198 StartY=-2.74689 StartZ=0 EndX=-0.13715 EndY=-2.74708 EndZ=0
    g8: LineSegment StartX=-0.13715 StartY=-2.74708 StartZ=0 EndX=-0.688499 EndY=-2.66151 EndZ=0
    g9: LineSegment StartX=-0.688499 StartY=-2.66151 StartZ=0 EndX=-0.94393 EndY=-2.58392 EndZ=0
    g10: LineSegment StartX=-0.94393 StartY=-2.58392 StartZ=0 EndX=-1.18786 EndY=-2.4818 EndZ=0
    g11: LineSegment StartX=-1.18786 StartY=-2.4818 StartZ=0 EndX=-1.42897 EndY=-2.34335 EndZ=0
    g12: LineSegment StartX=-1.42897 StartY=-2.34335 StartZ=0 EndX=-1.64859 EndY=-2.19653 EndZ=0
    g13: LineSegment StartX=-1.64859 StartY=-2.19653 StartZ=0 EndX=-1.84554 EndY=-2.0342 EndZ=0
    g14: LineSegment StartX=-1.84554 StartY=-2.0342 StartZ=0 EndX=-1.84465 EndY=-1.22163 EndZ=0
    g15: LineSegment StartX=-1.84465 StartY=-1.22163 StartZ=0 EndX=-1.84999 EndY=-0.000151 EndZ=0
    g16: LineSegment StartX=-1.84999 StartY=-0.000151 StartZ=0 EndX=-1.85002 EndY=0.00099 EndZ=0
    g17: LineSegment StartX=-1.85002 StartY=0.00099 StartZ=0 EndX=1.85015 EndY=0.005067 EndZ=0
    g18: LineSegment StartX=1.84931 StartY=-2.02283 StartZ=0 EndX=1.84977 EndY=-2.03462 EndZ=0
    g19: LineSegment StartX=1.85015 StartY=0.005067 StartZ=0 EndX=1.84931 EndY=-2.02283 EndZ=0
  constraints (20):
    c: Coincident(g0,g1)
    c: Coincident(g1,g2)
    c: Coincident(g2,g3)
    c: Coincident(g3,g4)
    c: Coincident(g4,g5)
    c: Coincident(g5,g6)
    c: Coincident(g8,g9)
    c: Coincident(g9,g10)
    c: Coincident(g10,g11)
    c: Coincident(g11,g12)
    c: Coincident(g12,g13)
    c: Coincident(g13,g14)
    c: Coincident(g14,g15)
    c: Coincident(g15,g16)
    c: Coincident(g16,g17)
    c: Coincident(g0,g18)
    c: Coincident(g7,g8)
    c: Coincident(g6,g7)
    c: Coincident(g18,g19)
    c: Coincident(g17,g19)
FEATURE [PartDesign::Pad] Pad011
  Length = 2.5
  Length2 = 100
  Placement = pos=(0,0,0) rot=(0.57735,0.57735,0.57735;2.0944rad)
  Profile = -> Sketch013
  Type = 0
FEATURE [PartDesign::PolarPattern] PolarPattern011
  Angle = 360
  Axis = -> Sketch013 [N_Axis]
  BaseFeature = -> Pad011
  Occurrences = 4
  Originals = -> [Pad011]
  Placement = pos=(0,0,0) rot=(0.57735,0.57735,0.57735;2.0944rad)
FEATURE [Sketcher::SketchObject] Sketch
  MapMode = 45
  Placement = pos=(0,0,0) rot=(0.57735,0.57735,0.57735;2.0944rad)
  Support = -> [Sketch012,PolarPattern011]
  sketch-geometry (211):
    g0: LineSegment StartX=0 StartY=0 StartZ=0 EndX=23.0775 EndY=-0.007725 EndZ=0
    g1: LineSegment StartX=23.0775 StartY=-0.007725 StartZ=0 EndX=23.0915 EndY=0.254478 EndZ=0
    g2: LineSegment StartX=23.0915 StartY=0.254478 StartZ=0 EndX=23.1284 EndY=0.508391 EndZ=0
    g3: LineSegment StartX=23.1284 StartY=0.508391 StartZ=0 EndX=23.1869 EndY=0.740712 EndZ=0
    g4: LineSegment StartX=23.1869 StartY=0.740712 StartZ=0 EndX=23.2782 EndY=0.973565 EndZ=0
    g5: LineSegment StartX=23.2782 StartY=0.973565 StartZ=0 EndX=23.3963 EndY=1.22031 EndZ=0
    g6: LineSegment StartX=23.3963 StartY=1.22031 StartZ=0 EndX=23.5215 EndY=1.42239 EndZ=0
    g7: LineSegment StartX=23.5215 StartY=1.42239 StartZ=0 EndX=23.6745 EndY=1.62203 EndZ=0
    g8: LineSegment StartX=23.6745 StartY=1.62203 StartZ=0 EndX=23.8622 EndY=1.81795 EndZ=0
    g9: LineSegment StartX=23.8622 StartY=1.81795 StartZ=0 EndX=24.0428 EndY=1.97182 EndZ=0
    g10: LineSegment StartX=24.0428 StartY=1.97182 StartZ=0 EndX=24.2535 EndY=2.11914 EndZ=0
    g11: LineSegment StartX=24.2535 StartY=2.11914 StartZ=0 EndX=24.4771 EndY=2.24429 EndZ=0
    g12: LineSegment StartX=24.4771 StartY=2.24429 StartZ=0 EndX=24.7643 EndY=2.36841 EndZ=0
    g13: LineSegment StartX=24.7643 StartY=2.36841 StartZ=0 EndX=24.8553 EndY=2.41105 EndZ=0
    g14: LineSegment StartX=24.8553 StartY=2.41105 StartZ=0 EndX=24.9955 EndY=2.50386 EndZ=0
    g15: LineSegment StartX=24.9955 StartY=2.50386 StartZ=0 EndX=25.1151 EndY=2.62736 EndZ=0
    g16: LineSegment StartX=25.1151 StartY=2.62736 StartZ=0 EndX=25.2142 EndY=2.76003 EndZ=0
    g17: LineSegment StartX=25.2142 StartY=2.76003 StartZ=0 EndX=25.2969 EndY=2.93426 EndZ=0
    g18: LineSegment StartX=25.2969 StartY=2.93426 StartZ=0 EndX=25.3426 EndY=3.08419 EndZ=0
    g19: LineSegment StartX=25.3426 StartY=3.08419 StartZ=0 EndX=25.3551 EndY=3.24413 EndZ=0
    g20: LineSegment StartX=25.3551 StartY=3.24413 StartZ=0 EndX=25.349 EndY=3.41794 EndZ=0
    g21: LineSegment StartX=25.349 StartY=3.41794 StartZ=0 EndX=25.3326 EndY=3.53796 EndZ=0
    g22: LineSegment StartX=25.3326 StartY=3.53796 StartZ=0 EndX=25.2546 EndY=4.05249 EndZ=0
    g23: LineSegment StartX=25.2546 StartY=4.05249 StartZ=0 EndX=25.1642 EndY=4.58451 EndZ=0
    g24: LineSegment StartX=25.1642 StartY=4.58451 StartZ=0 EndX=25.1211 EndY=4.74519 EndZ=0
    g25: LineSegment StartX=25.1211 StartY=4.74519 StartZ=0 EndX=25.0493 EndY=4.90009 EndZ=0
    g26: LineSegment StartX=25.0493 StartY=4.90009 StartZ=0 EndX=24.9559 EndY=5.03652 EndZ=0
    g27: LineSegment StartX=24.9559 StartY=5.03652 StartZ=0 EndX=24.8359 EndY=5.16166 EndZ=0
    g28: LineSegment StartX=24.8359 StartY=5.16166 StartZ=0 EndX=24.7064 EndY=5.26066 EndZ=0
    g29: LineSegment StartX=24.7064 StartY=5.26066 StartZ=0 EndX=24.5515 EndY=5.33657 EndZ=0
    g30: LineSegment StartX=24.5515 StartY=5.33657 StartZ=0 EndX=24.3854 EndY=5.38889 EndZ=0
    g31: LineSegment StartX=24.3854 StartY=5.38889 StartZ=0 EndX=23.9661 EndY=5.429 EndZ=0
    g32: LineSegment StartX=23.9661 StartY=5.429 StartZ=0 EndX=23.7168 EndY=5.47721 EndZ=0
    g33: LineSegment StartX=23.7168 StartY=5.47721 StartZ=0 EndX=23.4789 EndY=5.55004 EndZ=0
    g34: LineSegment StartX=23.4789 StartY=5.55004 StartZ=0 EndX=23.244 EndY=5.64749 EndZ=0
    g35: LineSegment StartX=23.244 StartY=5.64749 StartZ=0 EndX=23.0141 EndY=5.77459 EndZ=0
    g36: LineSegment StartX=23.0141 StartY=5.77459 StartZ=0 EndX=22.81 EndY=5.91307 EndZ=0
    g37: LineSegment StartX=22.81 StartY=5.91307 StartZ=0 EndX=22.6171 EndY=6.07925 EndZ=0
    g38: LineSegment StartX=22.6171 StartY=6.07925 StartZ=0 EndX=22.4499 EndY=6.25158 EndZ=0
    g39: LineSegment StartX=22.4499 StartY=6.25158 StartZ=0 EndX=22.2897 EndY=6.45644 EndZ=0
    g40: LineSegment StartX=22.2897 StartY=6.45644 StartZ=0 EndX=22.1484 EndY=6.67133 EndZ=0
    g41: LineSegment StartX=22.1484 StartY=6.67133 StartZ=0 EndX=22.0413 EndY=6.89628 EndZ=0
    g42: LineSegment StartX=22.0413 StartY=6.89628 StartZ=0 EndX=21.9449 EndY=7.13041 EndZ=0
    g43: LineSegment StartX=21.9449 StartY=7.13041 StartZ=0 EndX=21.883 EndY=7.36574 EndZ=0
    g44: LineSegment StartX=21.883 StartY=7.36574 StartZ=0 EndX=21.842 EndY=7.61808 EndZ=0
    g45: LineSegment StartX=21.842 StartY=7.61808 StartZ=0 EndX=21.8244 EndY=7.88752 EndZ=0
    g46: LineSegment StartX=21.8244 StartY=7.88752 StartZ=0 EndX=21.8388 EndY=8.12242 EndZ=0
    g47: LineSegment StartX=21.8388 StartY=8.12242 StartZ=0 EndX=21.8716 EndY=8.3765 EndZ=0
    g48: LineSegment StartX=21.8716 StartY=8.3765 StartZ=0 EndX=21.9322 EndY=8.62371 EndZ=0
    g49: LineSegment StartX=21.9322 StartY=8.62371 StartZ=0 EndX=22.0085 EndY=8.85622 EndZ=0
    g50: LineSegment StartX=22.0085 StartY=8.85622 StartZ=0 EndX=22.1095 EndY=9.0873 EndZ=0
    g51: LineSegment StartX=22.1095 StartY=9.0873 StartZ=0 EndX=22.2564 EndY=9.30001 EndZ=0
    g52: LineSegment StartX=22.2564 StartY=9.30001 StartZ=0 EndX=22.4222 EndY=9.51816 EndZ=0
    g53: LineSegment StartX=22.4222 StartY=9.51816 StartZ=0 EndX=22.5814 EndY=9.69568 EndZ=0
    g54: LineSegment StartX=22.5814 StartY=9.69568 StartZ=0 EndX=22.7773 EndY=9.86401 EndZ=0
    g55: LineSegment StartX=22.7773 StartY=9.86401 StartZ=0 EndX=22.8829 EndY=9.96654 EndZ=0
    g56: LineSegment StartX=22.8829 StartY=9.96654 StartZ=0 EndX=22.9946 EndY=10.1027 EndZ=0
    g57: LineSegment StartX=22.9946 StartY=10.1027 StartZ=0 EndX=23.0728 EndY=10.2473 EndZ=0
    g58: LineSegment StartX=23.0728 StartY=10.2473 StartZ=0 EndX=23.1295 EndY=10.4111 EndZ=0
    g59: LineSegment StartX=23.1295 StartY=10.4111 StartZ=0 EndX=23.1555 EndY=10.5871 EndZ=0
    g60: LineSegment StartX=23.1555 StartY=10.5871 StartZ=0 EndX=23.1416 EndY=10.7621 EndZ=0
    g61: LineSegment StartX=23.1416 StartY=10.7621 StartZ=0 EndX=23.1095 EndY=10.9289 EndZ=0
    g62: LineSegment StartX=23.1095 StartY=10.9289 StartZ=0 EndX=23.0483 EndY=11.0865 EndZ=0
    g63: LineSegment StartX=23.0483 StartY=11.0865 StartZ=0 EndX=22.8718 EndY=11.4442 EndZ=0
    g64: LineSegment StartX=22.8718 StartY=11.4442 StartZ=0 EndX=22.5688 EndY=12.0257 EndZ=0
    g65: LineSegment StartX=22.5688 StartY=12.0257 StartZ=0 EndX=22.5075 EndY=12.152 EndZ=0
    g66: LineSegment StartX=22.5075 StartY=12.152 StartZ=0 EndX=22.4248 EndY=12.279 EndZ=0
    g67: LineSegment StartX=22.4248 StartY=12.279 StartZ=0 EndX=22.3208 EndY=12.3999 EndZ=0
    g68: LineSegment StartX=22.3208 StartY=12.3999 StartZ=0 EndX=22.1769 EndY=12.5009 EndZ=0
    g69: LineSegment StartX=22.1769 StartY=12.5009 StartZ=0 EndX=22.0254 EndY=12.5805 EndZ=0
    g70: LineSegment StartX=22.0254 StartY=12.5805 StartZ=0 EndX=21.8678 EndY=12.6325 EndZ=0
    g71: LineSegment StartX=21.8678 StartY=12.6325 StartZ=0 EndX=21.6949 EndY=12.6601 EndZ=0
    g72: LineSegment StartX=21.6949 StartY=12.6601 StartZ=0 EndX=21.5327 EndY=12.6555 EndZ=0
    g73: LineSegment StartX=21.5327 StartY=12.6555 StartZ=0 EndX=21.1061 EndY=12.5612 EndZ=0
    g74: LineSegment StartX=21.1061 StartY=12.5612 StartZ=0 EndX=20.8582 EndY=12.5352 EndZ=0
    g75: LineSegment StartX=20.8582 StartY=12.5352 StartZ=0 EndX=20.6087 EndY=12.5337 EndZ=0
    g76: LineSegment StartX=20.6087 StartY=12.5337 StartZ=0 EndX=20.3501 EndY=12.5536 EndZ=0
    g77: LineSegment StartX=20.3501 StartY=12.5536 StartZ=0 EndX=20.0854 EndY=12.5979 EndZ=0
    g78: LineSegment StartX=20.0854 StartY=12.5979 StartZ=0 EndX=19.8665 EndY=12.6699 EndZ=0
    g79: LineSegment StartX=19.8665 StartY=12.6699 StartZ=0 EndX=19.614 EndY=12.7678 EndZ=0
    g80: LineSegment StartX=19.614 StartY=12.7678 StartZ=0 EndX=19.4105 EndY=12.881 EndZ=0
    g81: LineSegment StartX=19.4105 StartY=12.881 StartZ=0 EndX=19.1993 EndY=13.0264 EndZ=0
    g82: LineSegment StartX=19.1993 StartY=13.0264 StartZ=0 EndX=18.9927 EndY=13.2018 EndZ=0
    g83: LineSegment StartX=18.9927 StartY=13.2018 StartZ=0 EndX=18.8259 EndY=13.3625 EndZ=0
    g84: LineSegment StartX=18.8259 StartY=13.3625 StartZ=0 EndX=18.6714 EndY=13.5553 EndZ=0
    g85: LineSegment StartX=18.6714 StartY=13.5553 StartZ=0 EndX=18.5367 EndY=13.768 EndZ=0
    g86: LineSegment StartX=18.5367 StartY=13.768 StartZ=0 EndX=18.4051 EndY=14.0083 EndZ=0
    g87: LineSegment StartX=18.4051 StartY=14.0083 StartZ=0 EndX=18.3225 EndY=14.2255 EndZ=0
    g88: LineSegment StartX=18.3225 StartY=14.2255 StartZ=0 EndX=18.2506 EndY=14.4903 EndZ=0
    g89: LineSegment StartX=18.2506 StartY=14.4903 StartZ=0 EndX=18.2154 EndY=14.7183 EndZ=0
    g90: LineSegment StartX=18.2154 StartY=14.7183 StartZ=0 EndX=18.2017 EndY=14.9876 EndZ=0
    g91: LineSegment StartX=18.2017 StartY=14.9876 StartZ=0 EndX=18.1828 EndY=15.2236 EndZ=0
    g92: LineSegment StartX=18.1828 StartY=15.2236 StartZ=0 EndX=18.2304 EndY=15.4722 EndZ=0
    g93: LineSegment StartX=18.2304 StartY=15.4722 StartZ=0 EndX=18.2815 EndY=15.714 EndZ=0
    g94: LineSegment StartX=18.2815 StartY=15.714 StartZ=0 EndX=18.3735 EndY=15.9865 EndZ=0
    g95: LineSegment StartX=18.3735 StartY=15.9865 StartZ=0 EndX=18.4796 EndY=16.216 EndZ=0
    g96: LineSegment StartX=18.4796 StartY=16.216 StartZ=0 EndX=18.6771 EndY=16.5429 EndZ=0
    g97: LineSegment StartX=18.6771 StartY=16.5429 StartZ=0 EndX=18.7452 EndY=16.7132 EndZ=0
    g98: LineSegment StartX=18.7452 StartY=16.7132 StartZ=0 EndX=18.7725 EndY=16.8562 EndZ=0
    g99: LineSegment StartX=18.7725 StartY=16.8562 StartZ=0 EndX=18.7793 EndY=17.0538 EndZ=0
    g100: LineSegment StartX=18.7793 StartY=17.0538 StartZ=0 EndX=18.7515 EndY=17.1989 EndZ=0
    g101: LineSegment StartX=18.7515 StartY=17.1989 StartZ=0 EndX=18.7073 EndY=17.3454 EndZ=0
    g102: LineSegment StartX=18.7073 StartY=17.3454 StartZ=0 EndX=18.6221 EndY=17.4986 EndZ=0
    g103: LineSegment StartX=18.6221 StartY=17.4986 StartZ=0 EndX=18.5404 EndY=17.6076 EndZ=0
    g104: LineSegment StartX=18.5404 StartY=17.6076 StartZ=0 EndX=18.4484 EndY=17.7132 EndZ=0
    g105: LineSegment StartX=18.4484 StartY=17.7132 StartZ=0 EndX=17.7843 EndY=18.3841 EndZ=0
    g106: LineSegment StartX=17.7843 StartY=18.3841 StartZ=0 EndX=17.6004 EndY=18.5476 EndZ=0
    g107: LineSegment StartX=17.6004 StartY=18.5476 StartZ=0 EndX=17.5187 EndY=18.6089 EndZ=0
    g108: LineSegment StartX=17.5187 StartY=18.6089 StartZ=0 EndX=17.3654 EndY=18.6872 EndZ=0
    g109: LineSegment StartX=17.3654 StartY=18.6872 StartZ=0 EndX=17.2156 EndY=18.7383 EndZ=0
    g110: LineSegment StartX=17.2156 StartY=18.7383 StartZ=0 EndX=17.0487 EndY=18.7621 EndZ=0
    g111: LineSegment StartX=17.0487 StartY=18.7621 StartZ=0 EndX=16.8852 EndY=18.7724 EndZ=0
    g112: LineSegment StartX=16.8852 StartY=18.7724 StartZ=0 EndX=16.7183 EndY=18.7417 EndZ=0
    g113: LineSegment StartX=16.7183 StartY=18.7417 StartZ=0 EndX=16.5651 EndY=18.694 EndZ=0
    g114: LineSegment StartX=16.5651 StartY=18.694 StartZ=0 EndX=16.3709 EndY=18.5851 EndZ=0
    g115: LineSegment StartX=16.3709 StartY=18.5851 StartZ=0 EndX=16.1496 EndY=18.4522 EndZ=0
    g116: LineSegment StartX=16.1496 StartY=18.4522 StartZ=0 EndX=15.9752 EndY=18.3739 EndZ=0
    g117: LineSegment StartX=15.9752 StartY=18.3739 StartZ=0 EndX=15.7423 EndY=18.2963 EndZ=0
    g118: LineSegment StartX=15.7423 StartY=18.2963 StartZ=0 EndX=15.5003 EndY=18.2233 EndZ=0
    g119: LineSegment StartX=15.5003 StartY=18.2233 StartZ=0 EndX=15.2492 EndY=18.1982 EndZ=0
    g120: LineSegment StartX=15.2492 StartY=18.1982 StartZ=0 EndX=14.973 EndY=18.2004 EndZ=0
    g121: LineSegment StartX=14.973 StartY=18.2004 StartZ=0 EndX=14.7241 EndY=18.2141 EndZ=0
    g122: LineSegment StartX=14.7241 StartY=18.2141 StartZ=0 EndX=14.4685 EndY=18.2484 EndZ=0
    g123: LineSegment StartX=14.4685 StartY=18.2484 StartZ=0 EndX=14.2265 EndY=18.3192 EndZ=0
    g124: LineSegment StartX=14.2265 StartY=18.3192 StartZ=0 EndX=13.9799 EndY=18.4196 EndZ=0
    g125: LineSegment StartX=13.9799 StartY=18.4196 StartZ=0 EndX=13.7736 EndY=18.5304 EndZ=0
    g126: LineSegment StartX=13.7736 StartY=18.5304 StartZ=0 EndX=13.5557 EndY=18.6666 EndZ=0
    g127: LineSegment StartX=13.5557 StartY=18.6666 StartZ=0 EndX=13.3683 EndY=18.8267 EndZ=0
    g128: LineSegment StartX=13.3683 StartY=18.8267 StartZ=0 EndX=13.1844 EndY=18.997 EndZ=0
    g129: LineSegment StartX=13.1844 StartY=18.997 StartZ=0 EndX=13.0175 EndY=19.2047 EndZ=0
    g130: LineSegment StartX=13.0175 StartY=19.2047 StartZ=0 EndX=12.9086 EndY=19.4227 EndZ=0
    g131: LineSegment StartX=12.9086 StartY=19.4227 StartZ=0 EndX=12.694 EndY=19.8518 EndZ=0
    g132: LineSegment StartX=12.694 StartY=19.8518 StartZ=0 EndX=12.5986 EndY=20.1266 EndZ=0
    g133: LineSegment StartX=12.5986 StartY=20.1266 StartZ=0 EndX=12.5373 EndY=20.3616 EndZ=0
    g134: LineSegment StartX=12.5373 StartY=20.3616 StartZ=0 EndX=12.5305 EndY=20.6613 EndZ=0
    g135: LineSegment StartX=12.5305 StartY=20.6613 StartZ=0 EndX=12.527 EndY=20.852 EndZ=0
    g136: LineSegment StartX=12.527 StartY=20.852 StartZ=0 EndX=12.5713 EndY=21.1177 EndZ=0
    g137: LineSegment StartX=12.5713 StartY=21.1177 StartZ=0 EndX=12.6565 EndY=21.5025 EndZ=0
    g138: LineSegment StartX=12.6565 StartY=21.5025 StartZ=0 EndX=12.6531 EndY=21.7205 EndZ=0
    g139: LineSegment StartX=12.6531 StartY=21.7205 StartZ=0 EndX=12.6258 EndY=21.8771 EndZ=0
    g140: LineSegment StartX=12.6258 StartY=21.8771 StartZ=0 EndX=12.5747 EndY=22.0542 EndZ=0
    g141: LineSegment StartX=12.5747 StartY=22.0542 StartZ=0 EndX=12.5027 EndY=22.1813 EndZ=0
    g142: LineSegment StartX=12.5027 StartY=22.1813 StartZ=0 EndX=12.3937 EndY=22.3278 EndZ=0
    g143: LineSegment StartX=12.3937 StartY=22.3278 StartZ=0 EndX=12.278 EndY=22.4299 EndZ=0
    g144: LineSegment StartX=12.278 StartY=22.4299 StartZ=0 EndX=12.1179 EndY=22.5287 EndZ=0
    g145: LineSegment StartX=12.1179 StartY=22.5287 StartZ=0 EndX=11.7535 EndY=22.716 EndZ=0
    g146: LineSegment StartX=11.7535 StartY=22.716 StartZ=0 EndX=11.2792 EndY=22.9552 EndZ=0
    g147: LineSegment StartX=11.2792 StartY=22.9552 StartZ=0 EndX=11.0374 EndY=23.0607 EndZ=0
    g148: LineSegment StartX=11.0374 StartY=23.0607 StartZ=0 EndX=10.8875 EndY=23.1289 EndZ=0
    g149: LineSegment StartX=10.8875 StartY=23.1289 StartZ=0 EndX=10.7036 EndY=23.1527 EndZ=0
    g150: LineSegment StartX=10.7036 StartY=23.1527 StartZ=0 EndX=10.5571 EndY=23.1391 EndZ=0
    g151: LineSegment StartX=10.5571 StartY=23.1391 StartZ=0 EndX=10.38 EndY=23.1084 EndZ=0
    g152: LineSegment StartX=10.38 StartY=23.1084 StartZ=0 EndX=10.2643 EndY=23.0641 EndZ=0
    g153: LineSegment StartX=10.2643 StartY=23.0641 StartZ=0 EndX=10.1042 EndY=22.9892 EndZ=0
    g154: LineSegment StartX=10.1042 StartY=22.9892 StartZ=0 EndX=9.97817 EndY=22.9041 EndZ=0
    g155: LineSegment StartX=9.97817 StartY=22.9041 StartZ=0 EndX=9.8181 EndY=22.727 EndZ=0
    g156: LineSegment StartX=9.8181 StartY=22.727 StartZ=0 EndX=9.68528 EndY=22.5839 EndZ=0
    g157: LineSegment StartX=9.68528 StartY=22.5839 StartZ=0 EndX=9.5184 EndY=22.4068 EndZ=0
    g158: LineSegment StartX=9.5184 StartY=22.4068 StartZ=0 EndX=9.29702 EndY=22.2672 EndZ=0
    g159: LineSegment StartX=9.29702 StartY=22.2672 StartZ=0 EndX=9.09042 EndY=22.1273 EndZ=0
    g160: LineSegment StartX=9.09042 StartY=22.1273 StartZ=0 EndX=8.85883 EndY=22.0183 EndZ=0
    g161: LineSegment StartX=8.85883 StartY=22.0183 StartZ=0 EndX=8.60681 EndY=21.9332 EndZ=0
    g162: LineSegment StartX=8.60681 StartY=21.9332 StartZ=0 EndX=8.36841 EndY=21.8719 EndZ=0
    g163: LineSegment StartX=8.36841 StartY=21.8719 StartZ=0 EndX=8.11979 EndY=21.8344 EndZ=0
    g164: LineSegment StartX=8.11979 StartY=21.8344 StartZ=0 EndX=7.84392 EndY=21.8242 EndZ=0
    g165: LineSegment StartX=7.84392 StartY=21.8242 StartZ=0 EndX=7.61915 EndY=21.8446 EndZ=0
    g166: LineSegment StartX=7.61915 StartY=21.8446 StartZ=0 EndX=7.39096 EndY=21.8753 EndZ=0
    g167: LineSegment StartX=7.39096 StartY=21.8753 StartZ=0 EndX=7.10488 EndY=21.9536 EndZ=0
    g168: LineSegment StartX=7.10488 StartY=21.9536 StartZ=0 EndX=6.8801 EndY=22.0387 EndZ=0
    g169: LineSegment StartX=6.8801 StartY=22.0387 StartZ=0 EndX=6.66554 EndY=22.1613 EndZ=0
    g170: LineSegment StartX=6.66554 StartY=22.1613 StartZ=0 EndX=6.44417 EndY=22.2908 EndZ=0
    g171: LineSegment StartX=6.44417 StartY=22.2908 StartZ=0 EndX=6.19215 EndY=22.5087 EndZ=0
    g172: LineSegment StartX=6.19215 StartY=22.5087 StartZ=0 EndX=6.02186 EndY=22.6688 EndZ=0
    g173: LineSegment StartX=6.02186 StartY=22.6688 StartZ=0 EndX=5.87882 EndY=22.8391 EndZ=0
    g174: LineSegment StartX=5.87882 StartY=22.8391 StartZ=0 EndX=5.74259 EndY=23.0809 EndZ=0
    g175: LineSegment StartX=5.74259 StartY=23.0809 StartZ=0 EndX=5.62679 EndY=23.2989 EndZ=0
    g176: LineSegment StartX=5.62679 StartY=23.2989 StartZ=0 EndX=5.54923 EndY=23.4812 EndZ=0
    g177: LineSegment StartX=5.54923 StartY=23.4812 StartZ=0 EndX=5.48987 EndY=23.7141 EndZ=0
    g178: LineSegment StartX=5.48987 StartY=23.7141 StartZ=0 EndX=5.43965 EndY=23.931 EndZ=0
    g179: LineSegment StartX=5.43965 StartY=23.931 StartZ=0 EndX=5.38283 EndY=24.3702 EndZ=0
    g180: LineSegment StartX=5.38283 StartY=24.3702 StartZ=0 EndX=5.34402 EndY=24.5505 EndZ=0
    g181: LineSegment StartX=5.34402 StartY=24.5505 StartZ=0 EndX=5.26412 EndY=24.7012 EndZ=0
    g182: LineSegment StartX=5.26412 StartY=24.7012 StartZ=0 EndX=5.15662 EndY=24.8433 EndZ=0
    g183: LineSegment StartX=5.15662 StartY=24.8433 StartZ=0 EndX=5.03563 EndY=24.9643 EndZ=0
    g184: LineSegment StartX=5.03563 StartY=24.9643 StartZ=0 EndX=4.9055 EndY=25.0534 EndZ=0
    g185: LineSegment StartX=4.9055 StartY=25.0534 StartZ=0 EndX=4.76168 EndY=25.115 EndZ=0
    g186: LineSegment StartX=4.76168 StartY=25.115 StartZ=0 EndX=4.56991 EndY=25.1698 EndZ=0
    g187: LineSegment StartX=4.56991 StartY=25.1698 StartZ=0 EndX=4.22291 EndY=25.2269 EndZ=0
    g188: LineSegment StartX=4.22291 StartY=25.2269 StartZ=0 EndX=3.72501 EndY=25.306 EndZ=0
    g189: LineSegment StartX=3.72501 StartY=25.306 StartZ=0 EndX=3.40823 EndY=25.3504 EndZ=0
    g190: LineSegment StartX=3.40823 StartY=25.3504 StartZ=0 EndX=3.25674 EndY=25.3565 EndZ=0
    g191: LineSegment StartX=3.25674 StartY=25.3565 StartZ=0 EndX=3.08534 EndY=25.3351 EndZ=0
    g192: LineSegment StartX=3.08534 StartY=25.3351 StartZ=0 EndX=2.91854 EndY=25.2876 EndZ=0
    g193: LineSegment StartX=2.91854 StartY=25.2876 StartZ=0 EndX=2.76092 EndY=25.2111 EndZ=0
    g194: LineSegment StartX=2.76092 StartY=25.2111 StartZ=0 EndX=2.62472 EndY=25.1116 EndZ=0
    g195: LineSegment StartX=2.62472 StartY=25.1116 StartZ=0 EndX=2.50842 EndY=24.9984 EndZ=0
    g196: LineSegment StartX=2.50842 StartY=24.9984 StartZ=0 EndX=2.41174 EndY=24.8483 EndZ=0
    g197: LineSegment StartX=2.41174 StartY=24.8483 StartZ=0 EndX=2.30308 EndY=24.582 EndZ=0
    g198: LineSegment StartX=2.30308 StartY=24.582 StartZ=0 EndX=2.25622 EndY=24.4788 EndZ=0
    g199: LineSegment StartX=2.25622 StartY=24.4788 StartZ=0 EndX=2.13227 EndY=24.2646 EndZ=0
    g200: LineSegment StartX=2.13227 StartY=24.2646 StartZ=0 EndX=1.96394 EndY=24.0365 EndZ=0
    g201: LineSegment StartX=1.96394 StartY=24.0365 StartZ=0 EndX=1.80479 EndY=23.856 EndZ=0
    g202: LineSegment StartX=1.80479 StartY=23.856 StartZ=0 EndX=1.62573 EndY=23.6797 EndZ=0
    g203: LineSegment StartX=1.62573 StartY=23.6797 StartZ=0 EndX=1.41955 EndY=23.5197 EndZ=0
    g204: LineSegment StartX=1.41955 StartY=23.5197 StartZ=0 EndX=1.20904 EndY=23.3867 EndZ=0
    g205: LineSegment StartX=1.20904 StartY=23.3867 StartZ=0 EndX=0.984393 EndY=23.2759 EndZ=0
    g206: LineSegment StartX=0.984393 StartY=23.2759 StartZ=0 EndX=0.742307 EndY=23.1856 EndZ=0
    g207: LineSegment StartX=0.742307 StartY=23.1856 StartZ=0 EndX=0.498622 EndY=23.1238 EndZ=0
    g208: LineSegment StartX=0.498622 StartY=23.1238 StartZ=0 EndX=0.250381 EndY=23.0889 EndZ=0
    g209: LineSegment StartX=0.250381 StartY=23.0889 StartZ=0 EndX=-0.006065 EndY=23.0756 EndZ=0
    g210: LineSegment StartX=-0.006065 StartY=23.0756 StartZ=0 EndX=0 EndY=0 EndZ=0
  constraints (212):
    c: Coincident(g0,g1)
    c: Coincident(g1,g2)
    c: Coincident(g2,g3)
    c: Coincident(g3,g4)
    c: Coincident(g4,g5)
    c: Coincident(g5,g6)
    c: Coincident(g6,g7)
    c: Coincident(g7,g8)
    c: Coincident(g8,g9)
    c: Coincident(g9,g10)
    c: Coincident(g10,g11)
    c: Coincident(g11,g12)
    c: Coincident(g12,g13)
    c: Coincident(g13,g14)
    c: Coincident(g14,g15)
    c: Coincident(g15,g16)
    c: Coincident(g16,g17)
    c: Coincident(g17,g18)
    c: Coincident(g18,g19)
    c: Coincident(g19,g20)
    c: Coincident(g20,g21)
    c: Coincident(g21,g22)
    c: Coincident(g22,g23)
    c: Coincident(g23,g24)
    c: Coincident(g24,g25)
    c: Coincident(g25,g26)
    c: Coincident(g26,g27)
    c: Coincident(g27,g28)
    c: Coincident(g28,g29)
    c: Coincident(g29,g30)
    c: Coincident(g30,g31)
    c: Coincident(g31,g32)
    c: Coincident(g32,g33)
    c: Coincident(g33,g34)
    c: Coincident(g34,g35)
    c: Coincident(g35,g36)
    c: Coincident(g36,g37)
    c: Coincident(g37,g38)
    c: Coincident(g38,g39)
    c: Coincident(g39,g40)
    c: Coincident(g40,g41)
    c: Coincident(g41,g42)
    c: Coincident(g42,g43)
    c: Coincident(g43,g44)
    c: Coincident(g44,g45)
    c: Coincident(g45,g46)
    c: Coincident(g46,g47)
    c: Coincident(g47,g48)
    c: Coincident(g48,g49)
    c: Coincident(g49,g50)
    c: Coincident(g50,g51)
    c: Coincident(g51,g52)
    c: Coincident(g52,g53)
    c: Coincident(g53,g54)
    c: Coincident(g54,g55)
    c: Coincident(g55,g56)
    c: Coincident(g56,g57)
    c: Coincident(g57,g58)
    c: Coincident(g58,g59)
    c: Coincident(g59,g60)
    c: Coincident(g60,g61)
    c: Coincident(g61,g62)
    c: Coincident(g62,g63)
    c: Coincident(g63,g64)
    c: Coincident(g64,g65)
    c: Coincident(g65,g66)
    c: Coincident(g66,g67)
    c: Coincident(g67,g68)
    c: Coincident(g68,g69)
    c: Coincident(g69,g70)
    c: Coincident(g70,g71)
    c: Coincident(g71,g72)
    c: Coincident(g72,g73)
    c: Coincident(g73,g74)
    c: Coincident(g74,g75)
    c: Coincident(g75,g76)
    c: Coincident(g76,g77)
    c: Coincident(g77,g78)
    c: Coincident(g78,g79)
    c: Coincident(g79,g80)
    c: Coincident(g80,g81)
    c: Coincident(g81,g82)
    c: Coincident(g82,g83)
    c: Coincident(g83,g84)
    c: Coincident(g84,g85)
    c: Coincident(g85,g86)
    c: Coincident(g86,g87)
    c: Coincident(g87,g88)
    c: Coincident(g88,g89)
    c: Coincident(g89,g90)
    c: Coincident(g90,g91)
    c: Coincident(g91,g92)
    c: Coincident(g92,g93)
    c: Coincident(g93,g94)
    c: Coincident(g94,g95)
    c: Coincident(g95,g96)
    c: Coincident(g96,g97)
    c: Coincident(g97,g98)
    c: Coincident(g98,g99)
    c: Coincident(g99,g100)
    c: Coincident(g100,g101)
    c: Coincident(g101,g102)
    c: Coincident(g102,g103)
    c: Coincident(g103,g104)
    c: Coincident(g104,g105)
    c: Coincident(g105,g106)
    c: Coincident(g106,g107)
    c: Coincident(g107,g108)
    c: Coincident(g108,g109)
    c: Coincident(g109,g110)
    c: Coincident(g110,g111)
    c: Coincident(g111,g112)
    c: Coincident(g112,g113)
    c: Coincident(g113,g114)
    c: Coincident(g114,g115)
    c: Coincident(g115,g116)
    c: Coincident(g116,g117)
    c: Coincident(g117,g118)
    c: Coincident(g118,g119)
    c: Coincident(g119,g120)
    c: Coincident(g120,g121)
    c: Coincident(g121,g122)
    c: Coincident(g122,g123)
    c: Coincident(g123,g124)
    c: Coincident(g124,g125)
    c: Coincident(g125,g126)
    c: Coincident(g126,g127)
    c: Coincident(g127,g128)
    c: Coincident(g128,g129)
    c: Coincident(g129,g130)
    c: Coincident(g130,g131)
    c: Coincident(g131,g132)
    c: Coincident(g132,g133)
    c: Coincident(g133,g134)
    c: Coincident(g134,g135)
    c: Coincident(g135,g136)
    c: Coincident(g136,g137)
    c: Coincident(g137,g138)
    c: Coincident(g138,g139)
    c: Coincident(g139,g140)
    c: Coincident(g140,g141)
    c: Coincident(g141,g142)
    c: Coincident(g142,g143)
    c: Coincident(g143,g144)
    c: Coincident(g144,g145)
    c: Coincident(g145,g146)
    c: Coincident(g146,g147)
    c: Coincident(g147,g148)
    c: Coincident(g148,g149)
    c: Coincident(g149,g150)
    c: Coincident(g150,g151)
    c: Coincident(g151,g152)
    c: Coincident(g152,g153)
    c: Coincident(g153,g154)
    c: Coincident(g154,g155)
    c: Coincident(g155,g156)
    c: Coincident(g156,g157)
    c: Coincident(g157,g158)
    c: Coincident(g158,g159)
    c: Coincident(g159,g160)
    c: Coincident(g160,g161)
    c: Coincident(g161,g162)
    c: Coincident(g162,g163)
    c: Coincident(g163,g164)
    c: Coincident(g164,g165)
    c: Coincident(g165,g166)
    c: Coincident(g166,g167)
    c: Coincident(g167,g168)
    c: Coincident(g168,g169)
    c: Coincident(g169,g170)
    c: Coincident(g170,g171)
    c: Coincident(g171,g172)
    c: Coincident(g172,g173)
    c: Coincident(g173,g174)
    c: Coincident(g174,g175)
    c: Coincident(g175,g176)
    c: Coincident(g176,g177)
    c: Coincident(g177,g178)
    c: Coincident(g178,g179)
    c: Coincident(g179,g180)
    c: Coincident(g180,g181)
    c: Coincident(g181,g182)
    c: Coincident(g182,g183)
    c: Coincident(g183,g184)
    c: Coincident(g184,g185)
    c: Coincident(g185,g186)
    c: Coincident(g186,g187)
    c: Coincident(g187,g188)
    c: Coincident(g188,g189)
    c: Coincident(g189,g190)
    c: Coincident(g190,g191)
    c: Coincident(g191,g192)
    c: Coincident(g192,g193)
    c: Coincident(g193,g194)
    c: Coincident(g194,g195)
    c: Coincident(g195,g196)
    c: Coincident(g196,g197)
    c: Coincident(g197,g198)
    c: Coincident(g198,g199)
    c: Coincident(g199,g200)
    c: Coincident(g200,g201)
    c: Coincident(g201,g202)
    c: Coincident(g202,g203)
    c: Coincident(g203,g204)
    c: Coincident(g204,g205)
    c: Coincident(g205,g206)
    c: Coincident(g206,g207)
    c: Coincident(g207,g208)
    c: Coincident(g208,g209)
    c: Coincident(g0,g210)
    c: Coincident(g0,g-1)
    c: Coincident(g209,g210)
FEATURE [PartDesign::Pad] Pad
  Length = 3
  Length2 = 100
  Placement = pos=(0,0,0) rot=(0.57735,0.57735,0.57735;2.0944rad)
  Profile = -> Sketch
  Type = 0
FEATURE [PartDesign::PolarPattern] PolarPattern
  Angle = 360
  Axis = -> Sketch [N_Axis]
  BaseFeature = -> Pad
  Occurrences = 4
  Originals = -> [Pad]
  Placement = pos=(0,0,0) rot=(0.57735,0.57735,0.57735;2.0944rad)
FEATURE [PartDesign::Body] Body
  Group = -> [Sketch,Pad,PolarPattern]
  Origin = -> Origin
  Tip = -> PolarPattern
FEATURE [Part::Cut] Cut
  Base = -> Body
  Placement = pos=(0,0,1) rot=(0,0,1;0rad)
  Tool = -> Body001
FEATURE [Part::MultiFuse] Fusion
  Shapes = -> [Cut,Cylinder,Cut001]
FEATURE [Part::Cut] Cut004
  Base = -> Fusion
  Tool = -> Body002
FEATURE [Part::Cut] Cut007
  Base = -> Cut004
  Tool = -> Cylinder002
FEATURE [Part::MultiFuse] Fusion002
  Shapes = -> [Cut007,Cut006,Cut008]
FEATURE [Sketcher::SketchObject] Sketch014
  MapMode = 5
  Placement = pos=(0,0,0) rot=(0.57735,0.57735,-0.57735;4.18879rad)
  Support = -> [PolarPattern011]
FEATURE [PartDesign::Pocket] Pocket
  BaseFeature = -> PolarPattern011
  Length = 1
  Length2 = 100
  Placement = pos=(0,0,0) rot=(0.57735,0.57735,0.57735;2.0944rad)
  Profile = -> Sketch012
  Reversed = true
  Type = 1
FEATURE [PartDesign::PolarPattern] PolarPattern012
  Angle = 360
  Axis = -> Sketch012 [N_Axis]
  BaseFeature = -> Pocket
  Occurrences = 2
  Originals = -> [Pocket]
  Placement = pos=(0,0,0) rot=(0.57735,0.57735,0.57735;2.0944rad)
FEATURE [Sketcher::SketchObject] Sketch015
  MapMode = 5
  Placement = pos=(0,0,0) rot=(0.57735,0.57735,-0.57735;4.18879rad)
  Support = -> [PolarPattern012]
  sketch-geometry (2):
    g0: Circle CenterX=0 CenterY=0 CenterZ=0 NormalX=0 NormalY=0 NormalZ=1 AngleXU=0 Radius=22.57
    g1: Circle CenterX=0 CenterY=0 CenterZ=0 NormalX=0 NormalY=0 NormalZ=1 AngleXU=0 Radius=2.75498
  constraints (3):
    c: Coincident(g1,g0)
    c: Coincident(g-1,g0)
    c: Radius(g0) = 22.57
FEATURE [PartDesign::Pad] Pad012
  BaseFeature = -> PolarPattern012
  Length = 5.5
  Length2 = 100
  Placement = pos=(0,0,0) rot=(0.57735,0.57735,0.57735;2.0944rad)
  Profile = -> Sketch015
  Type = 0
FEATURE [Sketcher::SketchObject] Sketch016
  MapMode = 5
  Placement = pos=(-5.5,3.7e-15,-3.7e-15) rot=(0.57735,0.57735,-0.57735;4.18879rad)
  Support = -> [Pad012]
  sketch-geometry (2):
    g0: Circle CenterX=0 CenterY=0 CenterZ=0 NormalX=0 NormalY=0 NormalZ=1 AngleXU=0 Radius=2.77794
    g1: Circle CenterX=0 CenterY=0 CenterZ=0 NormalX=0 NormalY=0 NormalZ=1 AngleXU=0 Radius=17
  constraints (3):
    c: Coincident(g0,g1)
    c: Coincident(g0,g-1)
    c: Radius(g1) = 17
FEATURE [Sketcher::SketchObject] Sketch017
  MapMode = 5
  Placement = pos=(0,0,0) rot=(0.57735,0.57735,0.57735;2.0944rad)
  Support = -> [YZ_Plane015]
  sketch-geometry (211):
    g0: LineSegment StartX=0 StartY=0 StartZ=0 EndX=23.0775 EndY=-0.007725 EndZ=0
    g1: LineSegment StartX=23.0775 StartY=-0.007725 StartZ=0 EndX=23.0915 EndY=0.254478 EndZ=0
    g2: LineSegment StartX=23.0915 StartY=0.254478 StartZ=0 EndX=23.1284 EndY=0.508391 EndZ=0
    g3: LineSegment StartX=23.1284 StartY=0.508391 StartZ=0 EndX=23.1869 EndY=0.740712 EndZ=0
    g4: LineSegment StartX=23.1869 StartY=0.740712 StartZ=0 EndX=23.2782 EndY=0.973565 EndZ=0
    g5: LineSegment StartX=23.2782 StartY=0.973565 StartZ=0 EndX=23.3963 EndY=1.22031 EndZ=0
    g6: LineSegment StartX=23.3963 StartY=1.22031 StartZ=0 EndX=23.5215 EndY=1.42239 EndZ=0
    g7: LineSegment StartX=23.5215 StartY=1.42239 StartZ=0 EndX=23.6745 EndY=1.62203 EndZ=0
    g8: LineSegment StartX=23.6745 StartY=1.62203 StartZ=0 EndX=23.8622 EndY=1.81795 EndZ=0
    g9: LineSegment StartX=23.8622 StartY=1.81795 StartZ=0 EndX=24.0428 EndY=1.97182 EndZ=0
    g10: LineSegment StartX=24.0428 StartY=1.97182 StartZ=0 EndX=24.2535 EndY=2.11914 EndZ=0
    g11: LineSegment StartX=24.2535 StartY=2.11914 StartZ=0 EndX=24.4771 EndY=2.24429 EndZ=0
    g12: LineSegment StartX=24.4771 StartY=2.24429 StartZ=0 EndX=24.7643 EndY=2.36841 EndZ=0
    g13: LineSegment StartX=24.7643 StartY=2.36841 StartZ=0 EndX=24.8553 EndY=2.41105 EndZ=0
    g14: LineSegment StartX=24.8553 StartY=2.41105 StartZ=0 EndX=24.9955 EndY=2.50386 EndZ=0
    g15: LineSegment StartX=24.9955 StartY=2.50386 StartZ=0 EndX=25.1151 EndY=2.62736 EndZ=0
    g16: LineSegment StartX=25.1151 StartY=2.62736 StartZ=0 EndX=25.2142 EndY=2.76003 EndZ=0
    g17: LineSegment StartX=25.2142 StartY=2.76003 StartZ=0 EndX=25.2969 EndY=2.93426 EndZ=0
    g18: LineSegment StartX=25.2969 StartY=2.93426 StartZ=0 EndX=25.3426 EndY=3.08419 EndZ=0
    g19: LineSegment StartX=25.3426 StartY=3.08419 StartZ=0 EndX=25.3551 EndY=3.24413 EndZ=0
    g20: LineSegment StartX=25.3551 StartY=3.24413 StartZ=0 EndX=25.349 EndY=3.41794 EndZ=0
    g21: LineSegment StartX=25.349 StartY=3.41794 StartZ=0 EndX=25.3326 EndY=3.53796 EndZ=0
    g22: LineSegment StartX=25.3326 StartY=3.53796 StartZ=0 EndX=25.2546 EndY=4.05249 EndZ=0
    g23: LineSegment StartX=25.2546 StartY=4.05249 StartZ=0 EndX=25.1642 EndY=4.58451 EndZ=0
    g24: LineSegment StartX=25.1642 StartY=4.58451 StartZ=0 EndX=25.1211 EndY=4.74519 EndZ=0
    g25: LineSegment StartX=25.1211 StartY=4.74519 StartZ=0 EndX=25.0493 EndY=4.90009 EndZ=0
    g26: LineSegment StartX=25.0493 StartY=4.90009 StartZ=0 EndX=24.9559 EndY=5.03652 EndZ=0
    g27: LineSegment StartX=24.9559 StartY=5.03652 StartZ=0 EndX=24.8359 EndY=5.16166 EndZ=0
    g28: LineSegment StartX=24.8359 StartY=5.16166 StartZ=0 EndX=24.7064 EndY=5.26066 EndZ=0
    g29: LineSegment StartX=24.7064 StartY=5.26066 StartZ=0 EndX=24.5515 EndY=5.33657 EndZ=0
    g30: LineSegment StartX=24.5515 StartY=5.33657 StartZ=0 EndX=24.3854 EndY=5.38889 EndZ=0
    g31: LineSegment StartX=24.3854 StartY=5.38889 StartZ=0 EndX=23.9661 EndY=5.429 EndZ=0
    g32: LineSegment StartX=23.9661 StartY=5.429 StartZ=0 EndX=23.7168 EndY=5.47721 EndZ=0
    g33: LineSegment StartX=23.7168 StartY=5.47721 StartZ=0 EndX=23.4789 EndY=5.55004 EndZ=0
    g34: LineSegment StartX=23.4789 StartY=5.55004 StartZ=0 EndX=23.244 EndY=5.64749 EndZ=0
    g35: LineSegment StartX=23.244 StartY=5.64749 StartZ=0 EndX=23.0141 EndY=5.77459 EndZ=0
    g36: LineSegment StartX=23.0141 StartY=5.77459 StartZ=0 EndX=22.81 EndY=5.91307 EndZ=0
    g37: LineSegment StartX=22.81 StartY=5.91307 StartZ=0 EndX=22.6171 EndY=6.07925 EndZ=0
    g38: LineSegment StartX=22.6171 StartY=6.07925 StartZ=0 EndX=22.4499 EndY=6.25158 EndZ=0
    g39: LineSegment StartX=22.4499 StartY=6.25158 StartZ=0 EndX=22.2897 EndY=6.45644 EndZ=0
    g40: LineSegment StartX=22.2897 StartY=6.45644 StartZ=0 EndX=22.1484 EndY=6.67133 EndZ=0
    g41: LineSegment StartX=22.1484 StartY=6.67133 StartZ=0 EndX=22.0413 EndY=6.89628 EndZ=0
    g42: LineSegment StartX=22.0413 StartY=6.89628 StartZ=0 EndX=21.9449 EndY=7.13041 EndZ=0
    g43: LineSegment StartX=21.9449 StartY=7.13041 StartZ=0 EndX=21.883 EndY=7.36574 EndZ=0
    g44: LineSegment StartX=21.883 StartY=7.36574 StartZ=0 EndX=21.842 EndY=7.61808 EndZ=0
    g45: LineSegment StartX=21.842 StartY=7.61808 StartZ=0 EndX=21.8244 EndY=7.88752 EndZ=0
    g46: LineSegment StartX=21.8244 StartY=7.88752 StartZ=0 EndX=21.8388 EndY=8.12242 EndZ=0
    g47: LineSegment StartX=21.8388 StartY=8.12242 StartZ=0 EndX=21.8716 EndY=8.3765 EndZ=0
    g48: LineSegment StartX=21.8716 StartY=8.3765 StartZ=0 EndX=21.9322 EndY=8.62371 EndZ=0
    g49: LineSegment StartX=21.9322 StartY=8.62371 StartZ=0 EndX=22.0085 EndY=8.85622 EndZ=0
    g50: LineSegment StartX=22.0085 StartY=8.85622 StartZ=0 EndX=22.1095 EndY=9.0873 EndZ=0
    g51: LineSegment StartX=22.1095 StartY=9.0873 StartZ=0 EndX=22.2564 EndY=9.30001 EndZ=0
    g52: LineSegment StartX=22.2564 StartY=9.30001 StartZ=0 EndX=22.4222 EndY=9.51816 EndZ=0
    g53: LineSegment StartX=22.4222 StartY=9.51816 StartZ=0 EndX=22.5814 EndY=9.69568 EndZ=0
    g54: LineSegment StartX=22.5814 StartY=9.69568 StartZ=0 EndX=22.7773 EndY=9.86401 EndZ=0
    g55: LineSegment StartX=22.7773 StartY=9.86401 StartZ=0 EndX=22.8829 EndY=9.96654 EndZ=0
    g56: LineSegment StartX=22.8829 StartY=9.96654 StartZ=0 EndX=22.9946 EndY=10.1027 EndZ=0
    g57: LineSegment StartX=22.9946 StartY=10.1027 StartZ=0 EndX=23.0728 EndY=10.2473 EndZ=0
    g58: LineSegment StartX=23.0728 StartY=10.2473 StartZ=0 EndX=23.1295 EndY=10.4111 EndZ=0
    g59: LineSegment StartX=23.1295 StartY=10.4111 StartZ=0 EndX=23.1555 EndY=10.5871 EndZ=0
    g60: LineSegment StartX=23.1555 StartY=10.5871 StartZ=0 EndX=23.1416 EndY=10.7621 EndZ=0
    g61: LineSegment StartX=23.1416 StartY=10.7621 StartZ=0 EndX=23.1095 EndY=10.9289 EndZ=0
    g62: LineSegment StartX=23.1095 StartY=10.9289 StartZ=0 EndX=23.0483 EndY=11.0865 EndZ=0
    g63: LineSegment StartX=23.0483 StartY=11.0865 StartZ=0 EndX=22.8718 EndY=11.4442 EndZ=0
    g64: LineSegment StartX=22.8718 StartY=11.4442 StartZ=0 EndX=22.5688 EndY=12.0257 EndZ=0
    g65: LineSegment StartX=22.5688 StartY=12.0257 StartZ=0 EndX=22.5075 EndY=12.152 EndZ=0
    g66: LineSegment StartX=22.5075 StartY=12.152 StartZ=0 EndX=22.4248 EndY=12.279 EndZ=0
    g67: LineSegment StartX=22.4248 StartY=12.279 StartZ=0 EndX=22.3208 EndY=12.3999 EndZ=0
    g68: LineSegment StartX=22.3208 StartY=12.3999 StartZ=0 EndX=22.1769 EndY=12.5009 EndZ=0
    g69: LineSegment StartX=22.1769 StartY=12.5009 StartZ=0 EndX=22.0254 EndY=12.5805 EndZ=0
    g70: LineSegment StartX=22.0254 StartY=12.5805 StartZ=0 EndX=21.8678 EndY=12.6325 EndZ=0
    g71: LineSegment StartX=21.8678 StartY=12.6325 StartZ=0 EndX=21.6949 EndY=12.6601 EndZ=0
    g72: LineSegment StartX=21.6949 StartY=12.6601 StartZ=0 EndX=21.5327 EndY=12.6555 EndZ=0
    g73: LineSegment StartX=21.5327 StartY=12.6555 StartZ=0 EndX=21.1061 EndY=12.5612 EndZ=0
    g74: LineSegment StartX=21.1061 StartY=12.5612 StartZ=0 EndX=20.8582 EndY=12.5352 EndZ=0
    g75: LineSegment StartX=20.8582 StartY=12.5352 StartZ=0 EndX=20.6087 EndY=12.5337 EndZ=0
    g76: LineSegment StartX=20.6087 StartY=12.5337 StartZ=0 EndX=20.3501 EndY=12.5536 EndZ=0
    g77: LineSegment StartX=20.3501 StartY=12.5536 StartZ=0 EndX=20.0854 EndY=12.5979 EndZ=0
    g78: LineSegment StartX=20.0854 StartY=12.5979 StartZ=0 EndX=19.8665 EndY=12.6699 EndZ=0
    g79: LineSegment StartX=19.8665 StartY=12.6699 StartZ=0 EndX=19.614 EndY=12.7678 EndZ=0
    g80: LineSegment StartX=19.614 StartY=12.7678 StartZ=0 EndX=19.4105 EndY=12.881 EndZ=0
    g81: LineSegment StartX=19.4105 StartY=12.881 StartZ=0 EndX=19.1993 EndY=13.0264 EndZ=0
    g82: LineSegment StartX=19.1993 StartY=13.0264 StartZ=0 EndX=18.9927 EndY=13.2018 EndZ=0
    g83: LineSegment StartX=18.9927 StartY=13.2018 StartZ=0 EndX=18.8259 EndY=13.3625 EndZ=0
    g84: LineSegment StartX=18.8259 StartY=13.3625 StartZ=0 EndX=18.6714 EndY=13.5553 EndZ=0
    g85: LineSegment StartX=18.6714 StartY=13.5553 StartZ=0 EndX=18.5367 EndY=13.768 EndZ=0
    g86: LineSegment StartX=18.5367 StartY=13.768 StartZ=0 EndX=18.4051 EndY=14.0083 EndZ=0
    g87: LineSegment StartX=18.4051 StartY=14.0083 StartZ=0 EndX=18.3225 EndY=14.2255 EndZ=0
    g88: LineSegment StartX=18.3225 StartY=14.2255 StartZ=0 EndX=18.2506 EndY=14.4903 EndZ=0
    g89: LineSegment StartX=18.2506 StartY=14.4903 StartZ=0 EndX=18.2154 EndY=14.7183 EndZ=0
    g90: LineSegment StartX=18.2154 StartY=14.7183 StartZ=0 EndX=18.2017 EndY=14.9876 EndZ=0
    g91: LineSegment StartX=18.2017 StartY=14.9876 StartZ=0 EndX=18.1828 EndY=15.2236 EndZ=0
    g92: LineSegment StartX=18.1828 StartY=15.2236 StartZ=0 EndX=18.2304 EndY=15.4722 EndZ=0
    g93: LineSegment StartX=18.2304 StartY=15.4722 StartZ=0 EndX=18.2815 EndY=15.714 EndZ=0
    g94: LineSegment StartX=18.2815 StartY=15.714 StartZ=0 EndX=18.3735 EndY=15.9865 EndZ=0
    g95: LineSegment StartX=18.3735 StartY=15.9865 StartZ=0 EndX=18.4796 EndY=16.216 EndZ=0
    g96: LineSegment StartX=18.4796 StartY=16.216 StartZ=0 EndX=18.6771 EndY=16.5429 EndZ=0
    g97: LineSegment StartX=18.6771 StartY=16.5429 StartZ=0 EndX=18.7452 EndY=16.7132 EndZ=0
    g98: LineSegment StartX=18.7452 StartY=16.7132 StartZ=0 EndX=18.7725 EndY=16.8562 EndZ=0
    g99: LineSegment StartX=18.7725 StartY=16.8562 StartZ=0 EndX=18.7793 EndY=17.0538 EndZ=0
    g100: LineSegment StartX=18.7793 StartY=17.0538 StartZ=0 EndX=18.7515 EndY=17.1989 EndZ=0
    g101: LineSegment StartX=18.7515 StartY=17.1989 StartZ=0 EndX=18.7073 EndY=17.3454 EndZ=0
    g102: LineSegment StartX=18.7073 StartY=17.3454 StartZ=0 EndX=18.6221 EndY=17.4986 EndZ=0
    g103: LineSegment StartX=18.6221 StartY=17.4986 StartZ=0 EndX=18.5404 EndY=17.6076 EndZ=0
    g104: LineSegment StartX=18.5404 StartY=17.6076 StartZ=0 EndX=18.4484 EndY=17.7132 EndZ=0
    g105: LineSegment StartX=18.4484 StartY=17.7132 StartZ=0 EndX=17.7843 EndY=18.3841 EndZ=0
    g106: LineSegment StartX=17.7843 StartY=18.3841 StartZ=0 EndX=17.6004 EndY=18.5476 EndZ=0
    g107: LineSegment StartX=17.6004 StartY=18.5476 StartZ=0 EndX=17.5187 EndY=18.6089 EndZ=0
    g108: LineSegment StartX=17.5187 StartY=18.6089 StartZ=0 EndX=17.3654 EndY=18.6872 EndZ=0
    g109: LineSegment StartX=17.3654 StartY=18.6872 StartZ=0 EndX=17.2156 EndY=18.7383 EndZ=0
    g110: LineSegment StartX=17.2156 StartY=18.7383 StartZ=0 EndX=17.0487 EndY=18.7621 EndZ=0
    g111: LineSegment StartX=17.0487 StartY=18.7621 StartZ=0 EndX=16.8852 EndY=18.7724 EndZ=0
    g112: LineSegment StartX=16.8852 StartY=18.7724 StartZ=0 EndX=16.7183 EndY=18.7417 EndZ=0
    g113: LineSegment StartX=16.7183 StartY=18.7417 StartZ=0 EndX=16.5651 EndY=18.694 EndZ=0
    g114: LineSegment StartX=16.5651 StartY=18.694 StartZ=0 EndX=16.3709 EndY=18.5851 EndZ=0
    g115: LineSegment StartX=16.3709 StartY=18.5851 StartZ=0 EndX=16.1496 EndY=18.4522 EndZ=0
    g116: LineSegment StartX=16.1496 StartY=18.4522 StartZ=0 EndX=15.9752 EndY=18.3739 EndZ=0
    g117: LineSegment StartX=15.9752 StartY=18.3739 StartZ=0 EndX=15.7423 EndY=18.2963 EndZ=0
    g118: LineSegment StartX=15.7423 StartY=18.2963 StartZ=0 EndX=15.5003 EndY=18.2233 EndZ=0
    g119: LineSegment StartX=15.5003 StartY=18.2233 StartZ=0 EndX=15.2492 EndY=18.1982 EndZ=0
    g120: LineSegment StartX=15.2492 StartY=18.1982 StartZ=0 EndX=14.973 EndY=18.2004 EndZ=0
    g121: LineSegment StartX=14.973 StartY=18.2004 StartZ=0 EndX=14.7241 EndY=18.2141 EndZ=0
    g122: LineSegment StartX=14.7241 StartY=18.2141 StartZ=0 EndX=14.4685 EndY=18.2484 EndZ=0
    g123: LineSegment StartX=14.4685 StartY=18.2484 StartZ=0 EndX=14.2265 EndY=18.3192 EndZ=0
    g124: LineSegment StartX=14.2265 StartY=18.3192 StartZ=0 EndX=13.9799 EndY=18.4196 EndZ=0
    g125: LineSegment StartX=13.9799 StartY=18.4196 StartZ=0 EndX=13.7736 EndY=18.5304 EndZ=0
    g126: LineSegment StartX=13.7736 StartY=18.5304 StartZ=0 EndX=13.5557 EndY=18.6666 EndZ=0
    g127: LineSegment StartX=13.5557 StartY=18.6666 StartZ=0 EndX=13.3683 EndY=18.8267 EndZ=0
    g128: LineSegment StartX=13.3683 StartY=18.8267 StartZ=0 EndX=13.1844 EndY=18.997 EndZ=0
    g129: LineSegment StartX=13.1844 StartY=18.997 StartZ=0 EndX=13.0175 EndY=19.2047 EndZ=0
    g130: LineSegment StartX=13.0175 StartY=19.2047 StartZ=0 EndX=12.9086 EndY=19.4227 EndZ=0
    g131: LineSegment StartX=12.9086 StartY=19.4227 StartZ=0 EndX=12.694 EndY=19.8518 EndZ=0
    g132: LineSegment StartX=12.694 StartY=19.8518 StartZ=0 EndX=12.5986 EndY=20.1266 EndZ=0
    g133: LineSegment StartX=12.5986 StartY=20.1266 StartZ=0 EndX=12.5373 EndY=20.3616 EndZ=0
    g134: LineSegment StartX=12.5373 StartY=20.3616 StartZ=0 EndX=12.5305 EndY=20.6613 EndZ=0
    g135: LineSegment StartX=12.5305 StartY=20.6613 StartZ=0 EndX=12.527 EndY=20.852 EndZ=0
    g136: LineSegment StartX=12.527 StartY=20.852 StartZ=0 EndX=12.5713 EndY=21.1177 EndZ=0
    g137: LineSegment StartX=12.5713 StartY=21.1177 StartZ=0 EndX=12.6565 EndY=21.5025 EndZ=0
    g138: LineSegment StartX=12.6565 StartY=21.5025 StartZ=0 EndX=12.6531 EndY=21.7205 EndZ=0
    g139: LineSegment StartX=12.6531 StartY=21.7205 StartZ=0 EndX=12.6258 EndY=21.8771 EndZ=0
    g140: LineSegment StartX=12.6258 StartY=21.8771 StartZ=0 EndX=12.5747 EndY=22.0542 EndZ=0
    g141: LineSegment StartX=12.5747 StartY=22.0542 StartZ=0 EndX=12.5027 EndY=22.1813 EndZ=0
    g142: LineSegment StartX=12.5027 StartY=22.1813 StartZ=0 EndX=12.3937 EndY=22.3278 EndZ=0
    g143: LineSegment StartX=12.3937 StartY=22.3278 StartZ=0 EndX=12.278 EndY=22.4299 EndZ=0
    g144: LineSegment StartX=12.278 StartY=22.4299 StartZ=0 EndX=12.1179 EndY=22.5287 EndZ=0
    g145: LineSegment StartX=12.1179 StartY=22.5287 StartZ=0 EndX=11.7535 EndY=22.716 EndZ=0
    g146: LineSegment StartX=11.7535 StartY=22.716 StartZ=0 EndX=11.2792 EndY=22.9552 EndZ=0
    g147: LineSegment StartX=11.2792 StartY=22.9552 StartZ=0 EndX=11.0374 EndY=23.0607 EndZ=0
    g148: LineSegment StartX=11.0374 StartY=23.0607 StartZ=0 EndX=10.8875 EndY=23.1289 EndZ=0
    g149: LineSegment StartX=10.8875 StartY=23.1289 StartZ=0 EndX=10.7036 EndY=23.1527 EndZ=0
    g150: LineSegment StartX=10.7036 StartY=23.1527 StartZ=0 EndX=10.5571 EndY=23.1391 EndZ=0
    g151: LineSegment StartX=10.5571 StartY=23.1391 StartZ=0 EndX=10.38 EndY=23.1084 EndZ=0
    g152: LineSegment StartX=10.38 StartY=23.1084 StartZ=0 EndX=10.2643 EndY=23.0641 EndZ=0
    g153: LineSegment StartX=10.2643 StartY=23.0641 StartZ=0 EndX=10.1042 EndY=22.9892 EndZ=0
    g154: LineSegment StartX=10.1042 StartY=22.9892 StartZ=0 EndX=9.97817 EndY=22.9041 EndZ=0
    g155: LineSegment StartX=9.97817 StartY=22.9041 StartZ=0 EndX=9.8181 EndY=22.727 EndZ=0
    g156: LineSegment StartX=9.8181 StartY=22.727 StartZ=0 EndX=9.68528 EndY=22.5839 EndZ=0
    g157: LineSegment StartX=9.68528 StartY=22.5839 StartZ=0 EndX=9.5184 EndY=22.4068 EndZ=0
    g158: LineSegment StartX=9.5184 StartY=22.4068 StartZ=0 EndX=9.29702 EndY=22.2672 EndZ=0
    g159: LineSegment StartX=9.29702 StartY=22.2672 StartZ=0 EndX=9.09042 EndY=22.1273 EndZ=0
    g160: LineSegment StartX=9.09042 StartY=22.1273 StartZ=0 EndX=8.85883 EndY=22.0183 EndZ=0
    g161: LineSegment StartX=8.85883 StartY=22.0183 StartZ=0 EndX=8.60681 EndY=21.9332 EndZ=0
    g162: LineSegment StartX=8.60681 StartY=21.9332 StartZ=0 EndX=8.36841 EndY=21.8719 EndZ=0
    g163: LineSegment StartX=8.36841 StartY=21.8719 StartZ=0 EndX=8.11979 EndY=21.8344 EndZ=0
    g164: LineSegment StartX=8.11979 StartY=21.8344 StartZ=0 EndX=7.84392 EndY=21.8242 EndZ=0
    g165: LineSegment StartX=7.84392 StartY=21.8242 StartZ=0 EndX=7.61915 EndY=21.8446 EndZ=0
    g166: LineSegment StartX=7.61915 StartY=21.8446 StartZ=0 EndX=7.39096 EndY=21.8753 EndZ=0
    g167: LineSegment StartX=7.39096 StartY=21.8753 StartZ=0 EndX=7.10488 EndY=21.9536 EndZ=0
    g168: LineSegment StartX=7.10488 StartY=21.9536 StartZ=0 EndX=6.8801 EndY=22.0387 EndZ=0
    g169: LineSegment StartX=6.8801 StartY=22.0387 StartZ=0 EndX=6.66554 EndY=22.1613 EndZ=0
    g170: LineSegment StartX=6.66554 StartY=22.1613 StartZ=0 EndX=6.44417 EndY=22.2908 EndZ=0
    g171: LineSegment StartX=6.44417 StartY=22.2908 StartZ=0 EndX=6.19215 EndY=22.5087 EndZ=0
    g172: LineSegment StartX=6.19215 StartY=22.5087 StartZ=0 EndX=6.02186 EndY=22.6688 EndZ=0
    g173: LineSegment StartX=6.02186 StartY=22.6688 StartZ=0 EndX=5.87882 EndY=22.8391 EndZ=0
    g174: LineSegment StartX=5.87882 StartY=22.8391 StartZ=0 EndX=5.74259 EndY=23.0809 EndZ=0
    g175: LineSegment StartX=5.74259 StartY=23.0809 StartZ=0 EndX=5.62679 EndY=23.2989 EndZ=0
    g176: LineSegment StartX=5.62679 StartY=23.2989 StartZ=0 EndX=5.54923 EndY=23.4812 EndZ=0
    g177: LineSegment StartX=5.54923 StartY=23.4812 StartZ=0 EndX=5.48987 EndY=23.7141 EndZ=0
    g178: LineSegment StartX=5.48987 StartY=23.7141 StartZ=0 EndX=5.43965 EndY=23.931 EndZ=0
    g179: LineSegment StartX=5.43965 StartY=23.931 StartZ=0 EndX=5.38283 EndY=24.3702 EndZ=0
    g180: LineSegment StartX=5.38283 StartY=24.3702 StartZ=0 EndX=5.34402 EndY=24.5505 EndZ=0
    g181: LineSegment StartX=5.34402 StartY=24.5505 StartZ=0 EndX=5.26412 EndY=24.7012 EndZ=0
    g182: LineSegment StartX=5.26412 StartY=24.7012 StartZ=0 EndX=5.15662 EndY=24.8433 EndZ=0
    g183: LineSegment StartX=5.15662 StartY=24.8433 StartZ=0 EndX=5.03563 EndY=24.9643 EndZ=0
    g184: LineSegment StartX=5.03563 StartY=24.9643 StartZ=0 EndX=4.9055 EndY=25.0534 EndZ=0
    g185: LineSegment StartX=4.9055 StartY=25.0534 StartZ=0 EndX=4.76168 EndY=25.115 EndZ=0
    g186: LineSegment StartX=4.76168 StartY=25.115 StartZ=0 EndX=4.56991 EndY=25.1698 EndZ=0
    g187: LineSegment StartX=4.56991 StartY=25.1698 StartZ=0 EndX=4.22291 EndY=25.2269 EndZ=0
    g188: LineSegment StartX=4.22291 StartY=25.2269 StartZ=0 EndX=3.72501 EndY=25.306 EndZ=0
    g189: LineSegment StartX=3.72501 StartY=25.306 StartZ=0 EndX=3.40823 EndY=25.3504 EndZ=0
    g190: LineSegment StartX=3.40823 StartY=25.3504 StartZ=0 EndX=3.25674 EndY=25.3565 EndZ=0
    g191: LineSegment StartX=3.25674 StartY=25.3565 StartZ=0 EndX=3.08534 EndY=25.3351 EndZ=0
    g192: LineSegment StartX=3.08534 StartY=25.3351 StartZ=0 EndX=2.91854 EndY=25.2876 EndZ=0
    g193: LineSegment StartX=2.91854 StartY=25.2876 StartZ=0 EndX=2.76092 EndY=25.2111 EndZ=0
    g194: LineSegment StartX=2.76092 StartY=25.2111 StartZ=0 EndX=2.62472 EndY=25.1116 EndZ=0
    g195: LineSegment StartX=2.62472 StartY=25.1116 StartZ=0 EndX=2.50842 EndY=24.9984 EndZ=0
    g196: LineSegment StartX=2.50842 StartY=24.9984 StartZ=0 EndX=2.41174 EndY=24.8483 EndZ=0
    g197: LineSegment StartX=2.41174 StartY=24.8483 StartZ=0 EndX=2.30308 EndY=24.582 EndZ=0
    g198: LineSegment StartX=2.30308 StartY=24.582 StartZ=0 EndX=2.25622 EndY=24.4788 EndZ=0
    g199: LineSegment StartX=2.25622 StartY=24.4788 StartZ=0 EndX=2.13227 EndY=24.2646 EndZ=0
    g200: LineSegment StartX=2.13227 StartY=24.2646 StartZ=0 EndX=1.96394 EndY=24.0365 EndZ=0
    g201: LineSegment StartX=1.96394 StartY=24.0365 StartZ=0 EndX=1.80479 EndY=23.856 EndZ=0
    g202: LineSegment StartX=1.80479 StartY=23.856 StartZ=0 EndX=1.62573 EndY=23.6797 EndZ=0
    g203: LineSegment StartX=1.62573 StartY=23.6797 StartZ=0 EndX=1.41955 EndY=23.5197 EndZ=0
    g204: LineSegment StartX=1.41955 StartY=23.5197 StartZ=0 EndX=1.20904 EndY=23.3867 EndZ=0
    g205: LineSegment StartX=1.20904 StartY=23.3867 StartZ=0 EndX=0.984393 EndY=23.2759 EndZ=0
    g206: LineSegment StartX=0.984393 StartY=23.2759 StartZ=0 EndX=0.742307 EndY=23.1856 EndZ=0
    g207: LineSegment StartX=0.742307 StartY=23.1856 StartZ=0 EndX=0.498622 EndY=23.1238 EndZ=0
    g208: LineSegment StartX=0.498622 StartY=23.1238 StartZ=0 EndX=0.250381 EndY=23.0889 EndZ=0
    g209: LineSegment StartX=0.250381 StartY=23.0889 StartZ=0 EndX=-0.006065 EndY=23.0756 EndZ=0
    g210: LineSegment StartX=-0.006065 StartY=23.0756 StartZ=0 EndX=0 EndY=0 EndZ=0
  constraints (212):
    c: Coincident(g0,g1)
    c: Coincident(g1,g2)
    c: Coincident(g2,g3)
    c: Coincident(g3,g4)
    c: Coincident(g4,g5)
    c: Coincident(g5,g6)
    c: Coincident(g6,g7)
    c: Coincident(g7,g8)
    c: Coincident(g8,g9)
    c: Coincident(g9,g10)
    c: Coincident(g10,g11)
    c: Coincident(g11,g12)
    c: Coincident(g12,g13)
    c: Coincident(g13,g14)
    c: Coincident(g14,g15)
    c: Coincident(g15,g16)
    c: Coincident(g16,g17)
    c: Coincident(g17,g18)
    c: Coincident(g18,g19)
    c: Coincident(g19,g20)
    c: Coincident(g20,g21)
    c: Coincident(g21,g22)
    c: Coincident(g22,g23)
    c: Coincident(g23,g24)
    c: Coincident(g24,g25)
    c: Coincident(g25,g26)
    c: Coincident(g26,g27)
    c: Coincident(g27,g28)
    c: Coincident(g28,g29)
    c: Coincident(g29,g30)
    c: Coincident(g30,g31)
    c: Coincident(g31,g32)
    c: Coincident(g32,g33)
    c: Coincident(g33,g34)
    c: Coincident(g34,g35)
    c: Coincident(g35,g36)
    c: Coincident(g36,g37)
    c: Coincident(g37,g38)
    c: Coincident(g38,g39)
    c: Coincident(g39,g40)
    c: Coincident(g40,g41)
    c: Coincident(g41,g42)
    c: Coincident(g42,g43)
    c: Coincident(g43,g44)
    c: Coincident(g44,g45)
    c: Coincident(g45,g46)
    c: Coincident(g46,g47)
    c: Coincident(g47,g48)
    c: Coincident(g48,g49)
    c: Coincident(g49,g50)
    c: Coincident(g50,g51)
    c: Coincident(g51,g52)
    c: Coincident(g52,g53)
    c: Coincident(g53,g54)
    c: Coincident(g54,g55)
    c: Coincident(g55,g56)
    c: Coincident(g56,g57)
    c: Coincident(g57,g58)
    c: Coincident(g58,g59)
    c: Coincident(g59,g60)
    c: Coincident(g60,g61)
    c: Coincident(g61,g62)
    c: Coincident(g62,g63)
    c: Coincident(g63,g64)
    c: Coincident(g64,g65)
    c: Coincident(g65,g66)
    c: Coincident(g66,g67)
    c: Coincident(g67,g68)
    c: Coincident(g68,g69)
    c: Coincident(g69,g70)
    c: Coincident(g70,g71)
    c: Coincident(g71,g72)
    c: Coincident(g72,g73)
    c: Coincident(g73,g74)
    c: Coincident(g74,g75)
    c: Coincident(g75,g76)
    c: Coincident(g76,g77)
    c: Coincident(g77,g78)
    c: Coincident(g78,g79)
    c: Coincident(g79,g80)
    c: Coincident(g80,g81)
    c: Coincident(g81,g82)
    c: Coincident(g82,g83)
    c: Coincident(g83,g84)
    c: Coincident(g84,g85)
    c: Coincident(g85,g86)
    c: Coincident(g86,g87)
    c: Coincident(g87,g88)
    c: Coincident(g88,g89)
    c: Coincident(g89,g90)
    c: Coincident(g90,g91)
    c: Coincident(g91,g92)
    c: Coincident(g92,g93)
    c: Coincident(g93,g94)
    c: Coincident(g94,g95)
    c: Coincident(g95,g96)
    c: Coincident(g96,g97)
    c: Coincident(g97,g98)
    c: Coincident(g98,g99)
    c: Coincident(g99,g100)
    c: Coincident(g100,g101)
    c: Coincident(g101,g102)
    c: Coincident(g102,g103)
    c: Coincident(g103,g104)
    c: Coincident(g104,g105)
    c: Coincident(g105,g106)
    c: Coincident(g106,g107)
    c: Coincident(g107,g108)
    c: Coincident(g108,g109)
    c: Coincident(g109,g110)
    c: Coincident(g110,g111)
    c: Coincident(g111,g112)
    c: Coincident(g112,g113)
    c: Coincident(g113,g114)
    c: Coincident(g114,g115)
    c: Coincident(g115,g116)
    c: Coincident(g116,g117)
    c: Coincident(g117,g118)
    c: Coincident(g118,g119)
    c: Coincident(g119,g120)
    c: Coincident(g120,g121)
    c: Coincident(g121,g122)
    c: Coincident(g122,g123)
    c: Coincident(g123,g124)
    c: Coincident(g124,g125)
    c: Coincident(g125,g126)
    c: Coincident(g126,g127)
    c: Coincident(g127,g128)
    c: Coincident(g128,g129)
    c: Coincident(g129,g130)
    c: Coincident(g130,g131)
    c: Coincident(g131,g132)
    c: Coincident(g132,g133)
    c: Coincident(g133,g134)
    c: Coincident(g134,g135)
    c: Coincident(g135,g136)
    c: Coincident(g136,g137)
    c: Coincident(g137,g138)
    c: Coincident(g138,g139)
    c: Coincident(g139,g140)
    c: Coincident(g140,g141)
    c: Coincident(g141,g142)
    c: Coincident(g142,g143)
    c: Coincident(g143,g144)
    c: Coincident(g144,g145)
    c: Coincident(g145,g146)
    c: Coincident(g146,g147)
    c: Coincident(g147,g148)
    c: Coincident(g148,g149)
    c: Coincident(g149,g150)
    c: Coincident(g150,g151)
    c: Coincident(g151,g152)
    c: Coincident(g152,g153)
    c: Coincident(g153,g154)
    c: Coincident(g154,g155)
    c: Coincident(g155,g156)
    c: Coincident(g156,g157)
    c: Coincident(g157,g158)
    c: Coincident(g158,g159)
    c: Coincident(g159,g160)
    c: Coincident(g160,g161)
    c: Coincident(g161,g162)
    c: Coincident(g162,g163)
    c: Coincident(g163,g164)
    c: Coincident(g164,g165)
    c: Coincident(g165,g166)
    c: Coincident(g166,g167)
    c: Coincident(g167,g168)
    c: Coincident(g168,g169)
    c: Coincident(g169,g170)
    c: Coincident(g170,g171)
    c: Coincident(g171,g172)
    c: Coincident(g172,g173)
    c: Coincident(g173,g174)
    c: Coincident(g174,g175)
    c: Coincident(g175,g176)
    c: Coincident(g176,g177)
    c: Coincident(g177,g178)
    c: Coincident(g178,g179)
    c: Coincident(g179,g180)
    c: Coincident(g180,g181)
    c: Coincident(g181,g182)
    c: Coincident(g182,g183)
    c: Coincident(g183,g184)
    c: Coincident(g184,g185)
    c: Coincident(g185,g186)
    c: Coincident(g186,g187)
    c: Coincident(g187,g188)
    c: Coincident(g188,g189)
    c: Coincident(g189,g190)
    c: Coincident(g190,g191)
    c: Coincident(g191,g192)
    c: Coincident(g192,g193)
    c: Coincident(g193,g194)
    c: Coincident(g194,g195)
    c: Coincident(g195,g196)
    c: Coincident(g196,g197)
    c: Coincident(g197,g198)
    c: Coincident(g198,g199)
    c: Coincident(g199,g200)
    c: Coincident(g200,g201)
    c: Coincident(g201,g202)
    c: Coincident(g202,g203)
    c: Coincident(g203,g204)
    c: Coincident(g204,g205)
    c: Coincident(g205,g206)
    c: Coincident(g206,g207)
    c: Coincident(g207,g208)
    c: Coincident(g208,g209)
    c: Coincident(g0,g210)
    c: Coincident(g0,g-1)
    c: Coincident(g209,g210)
FEATURE [PartDesign::Pad] Pad013
  Length = 2.5
  Length2 = 100
  Placement = pos=(0,0,0) rot=(0.57735,0.57735,0.57735;2.0944rad)
  Profile = -> Sketch017
  Type = 0
FEATURE [Sketcher::SketchObject] Sketch018
  MapMode = 5
  Placement = pos=(0,0,0) rot=(0.57735,0.57735,0.57735;2.0944rad)
  Support = -> [YZ_Plane015]
  sketch-geometry (20):
    g0: LineSegment StartX=1.84977 StartY=-2.03462 StartZ=0 EndX=1.64219 EndY=-2.20542 EndZ=0
    g1: LineSegment StartX=1.64219 StartY=-2.20542 StartZ=0 EndX=1.4178 EndY=-2.35642 EndZ=0
    g2: LineSegment StartX=1.4178 StartY=-2.35642 StartZ=0 EndX=1.1786 EndY=-2.48192 EndZ=0
    g3: LineSegment StartX=1.1786 StartY=-2.48192 StartZ=0 EndX=0.933165 EndY=-2.58946 EndZ=0
    g4: LineSegment StartX=0.933165 StartY=-2.58946 StartZ=0 EndX=0.669297 EndY=-2.66615 EndZ=0
    g5: LineSegment StartX=0.669297 StartY=-2.66615 StartZ=0 EndX=0.401357 EndY=-2.72007 EndZ=0
    g6: LineSegment StartX=0.401357 StartY=-2.72007 StartZ=0 EndX=0.133198 EndY=-2.74689 EndZ=0
    g7: LineSegment StartX=0.133198 StartY=-2.74689 StartZ=0 EndX=-0.13715 EndY=-2.74708 EndZ=0
    g8: LineSegment StartX=-0.13715 StartY=-2.74708 StartZ=0 EndX=-0.688499 EndY=-2.66151 EndZ=0
    g9: LineSegment StartX=-0.688499 StartY=-2.66151 StartZ=0 EndX=-0.94393 EndY=-2.58392 EndZ=0
    g10: LineSegment StartX=-0.94393 StartY=-2.58392 StartZ=0 EndX=-1.18786 EndY=-2.4818 EndZ=0
    g11: LineSegment StartX=-1.18786 StartY=-2.4818 StartZ=0 EndX=-1.42897 EndY=-2.34335 EndZ=0
    g12: LineSegment StartX=-1.42897 StartY=-2.34335 StartZ=0 EndX=-1.64859 EndY=-2.19653 EndZ=0
    g13: LineSegment StartX=-1.64859 StartY=-2.19653 StartZ=0 EndX=-1.84554 EndY=-2.0342 EndZ=0
    g14: LineSegment StartX=-1.84554 StartY=-2.0342 StartZ=0 EndX=-1.84465 EndY=-1.22163 EndZ=0
    g15: LineSegment StartX=-1.84465 StartY=-1.22163 StartZ=0 EndX=-1.84999 EndY=-0.000151 EndZ=0
    g16: LineSegment StartX=-1.84999 StartY=-0.000151 StartZ=0 EndX=-1.85002 EndY=0.00099 EndZ=0
    g17: LineSegment StartX=-1.85002 StartY=0.00099 StartZ=0 EndX=1.85015 EndY=0.005067 EndZ=0
    g18: LineSegment StartX=1.84931 StartY=-2.02283 StartZ=0 EndX=1.84977 EndY=-2.03462 EndZ=0
    g19: LineSegment StartX=1.85015 StartY=0.005067 StartZ=0 EndX=1.84931 EndY=-2.02283 EndZ=0
  constraints (20):
    c: Coincident(g0,g1)
    c: Coincident(g1,g2)
    c: Coincident(g2,g3)
    c: Coincident(g3,g4)
    c: Coincident(g4,g5)
    c: Coincident(g5,g6)
    c: Coincident(g8,g9)
    c: Coincident(g9,g10)
    c: Coincident(g10,g11)
    c: Coincident(g11,g12)
    c: Coincident(g12,g13)
    c: Coincident(g13,g14)
    c: Coincident(g14,g15)
    c: Coincident(g15,g16)
    c: Coincident(g16,g17)
    c: Coincident(g0,g18)
    c: Coincident(g7,g8)
    c: Coincident(g6,g7)
    c: Coincident(g18,g19)
    c: Coincident(g17,g19)
FEATURE [PartDesign::PolarPattern] PolarPattern013
  Angle = 360
  Axis = -> Sketch017 [N_Axis]
  BaseFeature = -> Pad013
  Occurrences = 4
  Originals = -> [Pad013]
  Placement = pos=(0,0,0) rot=(0.57735,0.57735,0.57735;2.0944rad)
FEATURE [PartDesign::Pocket] Pocket001
  BaseFeature = -> PolarPattern013
  Length = 1
  Length2 = 100
  Placement = pos=(0,0,0) rot=(0.57735,0.57735,0.57735;2.0944rad)
  Profile = -> Sketch018
  Reversed = true
  Type = 1
FEATURE [Sketcher::SketchObject] Sketch019
  MapMode = 5
  Placement = pos=(0,0,0) rot=(0.57735,0.57735,-0.57735;4.18879rad)
  Support = -> [PolarPattern013]
FEATURE [PartDesign::PolarPattern] PolarPattern014
  Angle = 360
  Axis = -> Sketch018 [N_Axis]
  BaseFeature = -> Pocket001
  Occurrences = 2
  Originals = -> [Pocket001]
  Placement = pos=(0,0,0) rot=(0.57735,0.57735,0.57735;2.0944rad)
FEATURE [Sketcher::SketchObject] Sketch020
  MapMode = 5
  Placement = pos=(0,0,0) rot=(0.57735,0.57735,-0.57735;4.18879rad)
  Support = -> [PolarPattern014]
  sketch-geometry (2):
    g0: Circle CenterX=0 CenterY=0 CenterZ=0 NormalX=0 NormalY=0 NormalZ=1 AngleXU=0 Radius=20.57
    g1: Circle CenterX=0 CenterY=0 CenterZ=0 NormalX=0 NormalY=0 NormalZ=1 AngleXU=0 Radius=2.75498
  constraints (3):
    c: Coincident(g1,g0)
    c: Coincident(g-1,g0)
    c: Radius(g0) = 20.57
FEATURE [PartDesign::Pad] Pad014
  BaseFeature = -> PolarPattern014
  Length = 5.5
  Length2 = 100
  Placement = pos=(0,0,0) rot=(0.57735,0.57735,0.57735;2.0944rad)
  Profile = -> Sketch020
  Type = 0
FEATURE [Sketcher::SketchObject] Sketch021
  MapMode = 5
  Placement = pos=(-5.5,3.7e-15,-3.7e-15) rot=(0.57735,0.57735,-0.57735;4.18879rad)
  Support = -> [Pad014]
  sketch-geometry (2):
    g0: Circle CenterX=0 CenterY=0 CenterZ=0 NormalX=0 NormalY=0 NormalZ=1 AngleXU=0 Radius=2.77794
    g1: Circle CenterX=0 CenterY=0 CenterZ=0 NormalX=0 NormalY=0 NormalZ=1 AngleXU=0 Radius=17
  constraints (3):
    c: Coincident(g0,g1)
    c: Coincident(g0,g-1)
    c: Radius(g1) = 17
FEATURE [PartDesign::Body] Body012
  Group = -> [Sketch018,Sketch017,Pad013,PolarPattern013,Sketch019,Pocket001,PolarPattern014,Sketch020,Pad014,Sketch021]
  Origin = -> Origin012
  Placement = pos=(-26,0,0) rot=(1,0,0;0.174533rad)
  Tip = -> Pad014
FEATURE [Mesh::Feature] Trak_WALL_E  label="Trak_WALL-E"
  Placement = pos=(-74.75,-3,26.6) rot=(0,1,0;1.5708rad)
FEATURE [PartDesign::Pad] Pad019
  BaseFeature = -> Pad012
  Length = 12.5
  Length2 = 100
  Placement = pos=(0,0,0) rot=(0.57735,0.57735,0.57735;2.0944rad)
  Profile = -> Sketch016
  Type = 0
FEATURE [Sketcher::SketchObject] Sketch032
  MapMode = 5
  Placement = pos=(-18,1.6e-14,-1.57e-14) rot=(-0.57735,-0.57735,0.57735;2.0944rad)
  Support = -> [Pad019]
  sketch-geometry (2):
    g0: Circle CenterX=0 CenterY=0 CenterZ=0 NormalX=0 NormalY=0 NormalZ=1 AngleXU=0 Radius=2.74985
    g1: Circle CenterX=0 CenterY=0 CenterZ=0 NormalX=0 NormalY=0 NormalZ=1 AngleXU=0 Radius=22.5957
  constraints (2):
    c: Coincident(g0,g1)
    c: Coincident(g0,g-1)
FEATURE [PartDesign::Pad] Pad020
  BaseFeature = -> Pad019
  Length = 5.5
  Length2 = 100
  Placement = pos=(0,0,0) rot=(0.57735,0.57735,0.57735;2.0944rad)
  Profile = -> Sketch032
  Type = 0
FEATURE [PartDesign::Body] Body011
  Group = -> [Sketch012,Sketch013,Pad011,PolarPattern011,Sketch014,Pocket,PolarPattern012,Sketch015,Pad012,Sketch016,Pad019,Sketch032,Pad020]
  Origin = -> Origin011
  Placement = pos=(0,0,0) rot=(1,0,0;0.174533rad)
  Tip = -> Pad020
FEATURE [Part::MultiFuse] Fusion003
  Shapes = -> [Body012,Body011]
FEATURE [App::MeasureDistance] Distance002  label="Distance: 50,66 mm"
  Distance = 50.6592
  P1 = (2.5,-23.9095,-8.163)
  P2 = (2.5,24.075,8.0806)
FEATURE [App::MeasureDistance] Distance003  label="Distance: 46,17 mm"
  Distance = 46.1685
  P1 = (2.5,20.3733,10.8328)
  P2 = (2.5,-20.5089,-10.6189)
FEATURE [Sketcher::SketchObject] Sketch033
  MapMode = 5
  Placement = pos=(0,0,0) rot=(0.57735,0.57735,0.57735;2.0944rad)
  Support = -> [YZ_Plane016]
  sketch-geometry (20):
    g0: LineSegment StartX=1.84977 StartY=-2.03462 StartZ=0 EndX=1.64219 EndY=-2.20542 EndZ=0
    g1: LineSegment StartX=1.64219 StartY=-2.20542 StartZ=0 EndX=1.4178 EndY=-2.35642 EndZ=0
    g2: LineSegment StartX=1.4178 StartY=-2.35642 StartZ=0 EndX=1.1786 EndY=-2.48192 EndZ=0
    g3: LineSegment StartX=1.1786 StartY=-2.48192 StartZ=0 EndX=0.933165 EndY=-2.58946 EndZ=0
    g4: LineSegment StartX=0.933165 StartY=-2.58946 StartZ=0 EndX=0.669297 EndY=-2.66615 EndZ=0
    g5: LineSegment StartX=0.669297 StartY=-2.66615 StartZ=0 EndX=0.401357 EndY=-2.72007 EndZ=0
    g6: LineSegment StartX=0.401357 StartY=-2.72007 StartZ=0 EndX=0.133198 EndY=-2.74689 EndZ=0
    g7: LineSegment StartX=0.133198 StartY=-2.74689 StartZ=0 EndX=-0.13715 EndY=-2.74708 EndZ=0
    g8: LineSegment StartX=-0.13715 StartY=-2.74708 StartZ=0 EndX=-0.688499 EndY=-2.66151 EndZ=0
    g9: LineSegment StartX=-0.688499 StartY=-2.66151 StartZ=0 EndX=-0.94393 EndY=-2.58392 EndZ=0
    g10: LineSegment StartX=-0.94393 StartY=-2.58392 StartZ=0 EndX=-1.18786 EndY=-2.4818 EndZ=0
    g11: LineSegment StartX=-1.18786 StartY=-2.4818 StartZ=0 EndX=-1.42897 EndY=-2.34335 EndZ=0
    g12: LineSegment StartX=-1.42897 StartY=-2.34335 StartZ=0 EndX=-1.64859 EndY=-2.19653 EndZ=0
    g13: LineSegment StartX=-1.64859 StartY=-2.19653 StartZ=0 EndX=-1.84554 EndY=-2.0342 EndZ=0
    g14: LineSegment StartX=-1.84554 StartY=-2.0342 StartZ=0 EndX=-1.84465 EndY=-1.22163 EndZ=0
    g15: LineSegment StartX=-1.84465 StartY=-1.22163 StartZ=0 EndX=-1.84999 EndY=-0.000151 EndZ=0
    g16: LineSegment StartX=-1.84999 StartY=-0.000151 StartZ=0 EndX=-1.85002 EndY=0.00099 EndZ=0
    g17: LineSegment StartX=-1.85002 StartY=0.00099 StartZ=0 EndX=1.85015 EndY=0.005067 EndZ=0
    g18: LineSegment StartX=1.84931 StartY=-2.02283 StartZ=0 EndX=1.84977 EndY=-2.03462 EndZ=0
    g19: LineSegment StartX=1.85015 StartY=0.005067 StartZ=0 EndX=1.84931 EndY=-2.02283 EndZ=0
  constraints (20):
    c: Coincident(g0,g1)
    c: Coincident(g1,g2)
    c: Coincident(g2,g3)
    c: Coincident(g3,g4)
    c: Coincident(g4,g5)
    c: Coincident(g5,g6)
    c: Coincident(g8,g9)
    c: Coincident(g9,g10)
    c: Coincident(g10,g11)
    c: Coincident(g11,g12)
    c: Coincident(g12,g13)
    c: Coincident(g13,g14)
    c: Coincident(g14,g15)
    c: Coincident(g15,g16)
    c: Coincident(g16,g17)
    c: Coincident(g0,g18)
    c: Coincident(g7,g8)
    c: Coincident(g6,g7)
    c: Coincident(g18,g19)
    c: Coincident(g17,g19)
FEATURE [Sketcher::SketchObject] Sketch035
  MapMode = 5
  Placement = pos=(0,0,0) rot=(0.57735,0.57735,0.57735;2.0944rad)
  Support = -> [YZ_Plane016]
  sketch-geometry (211):
    g0: LineSegment StartX=0 StartY=0 StartZ=0 EndX=23.0775 EndY=-0.007725 EndZ=0
    g1: LineSegment StartX=23.0775 StartY=-0.007725 StartZ=0 EndX=23.0915 EndY=0.254478 EndZ=0
    g2: LineSegment StartX=23.0915 StartY=0.254478 StartZ=0 EndX=23.1284 EndY=0.508391 EndZ=0
    g3: LineSegment StartX=23.1284 StartY=0.508391 StartZ=0 EndX=23.1869 EndY=0.740712 EndZ=0
    g4: LineSegment StartX=23.1869 StartY=0.740712 StartZ=0 EndX=23.2782 EndY=0.973565 EndZ=0
    g5: LineSegment StartX=23.2782 StartY=0.973565 StartZ=0 EndX=23.3963 EndY=1.22031 EndZ=0
    g6: LineSegment StartX=23.3963 StartY=1.22031 StartZ=0 EndX=23.5215 EndY=1.42239 EndZ=0
    g7: LineSegment StartX=23.5215 StartY=1.42239 StartZ=0 EndX=23.6745 EndY=1.62203 EndZ=0
    g8: LineSegment StartX=23.6745 StartY=1.62203 StartZ=0 EndX=23.8622 EndY=1.81795 EndZ=0
    g9: LineSegment StartX=23.8622 StartY=1.81795 StartZ=0 EndX=24.0428 EndY=1.97182 EndZ=0
    g10: LineSegment StartX=24.0428 StartY=1.97182 StartZ=0 EndX=24.2535 EndY=2.11914 EndZ=0
    g11: LineSegment StartX=24.2535 StartY=2.11914 StartZ=0 EndX=24.4771 EndY=2.24429 EndZ=0
    g12: LineSegment StartX=24.4771 StartY=2.24429 StartZ=0 EndX=24.7643 EndY=2.36841 EndZ=0
    g13: LineSegment StartX=24.7643 StartY=2.36841 StartZ=0 EndX=24.8553 EndY=2.41105 EndZ=0
    g14: LineSegment StartX=24.8553 StartY=2.41105 StartZ=0 EndX=24.9955 EndY=2.50386 EndZ=0
    g15: LineSegment StartX=24.9955 StartY=2.50386 StartZ=0 EndX=25.1151 EndY=2.62736 EndZ=0
    g16: LineSegment StartX=25.1151 StartY=2.62736 StartZ=0 EndX=25.2142 EndY=2.76003 EndZ=0
    g17: LineSegment StartX=25.2142 StartY=2.76003 StartZ=0 EndX=25.2969 EndY=2.93426 EndZ=0
    g18: LineSegment StartX=25.2969 StartY=2.93426 StartZ=0 EndX=25.3426 EndY=3.08419 EndZ=0
    g19: LineSegment StartX=25.3426 StartY=3.08419 StartZ=0 EndX=25.3551 EndY=3.24413 EndZ=0
    g20: LineSegment StartX=25.3551 StartY=3.24413 StartZ=0 EndX=25.349 EndY=3.41794 EndZ=0
    g21: LineSegment StartX=25.349 StartY=3.41794 StartZ=0 EndX=25.3326 EndY=3.53796 EndZ=0
    g22: LineSegment StartX=25.3326 StartY=3.53796 StartZ=0 EndX=25.2546 EndY=4.05249 EndZ=0
    g23: LineSegment StartX=25.2546 StartY=4.05249 StartZ=0 EndX=25.1642 EndY=4.58451 EndZ=0
    g24: LineSegment StartX=25.1642 StartY=4.58451 StartZ=0 EndX=25.1211 EndY=4.74519 EndZ=0
    g25: LineSegment StartX=25.1211 StartY=4.74519 StartZ=0 EndX=25.0493 EndY=4.90009 EndZ=0
    g26: LineSegment StartX=25.0493 StartY=4.90009 StartZ=0 EndX=24.9559 EndY=5.03652 EndZ=0
    g27: LineSegment StartX=24.9559 StartY=5.03652 StartZ=0 EndX=24.8359 EndY=5.16166 EndZ=0
    g28: LineSegment StartX=24.8359 StartY=5.16166 StartZ=0 EndX=24.7064 EndY=5.26066 EndZ=0
    g29: LineSegment StartX=24.7064 StartY=5.26066 StartZ=0 EndX=24.5515 EndY=5.33657 EndZ=0
    g30: LineSegment StartX=24.5515 StartY=5.33657 StartZ=0 EndX=24.3854 EndY=5.38889 EndZ=0
    g31: LineSegment StartX=24.3854 StartY=5.38889 StartZ=0 EndX=23.9661 EndY=5.429 EndZ=0
    g32: LineSegment StartX=23.9661 StartY=5.429 StartZ=0 EndX=23.7168 EndY=5.47721 EndZ=0
    g33: LineSegment StartX=23.7168 StartY=5.47721 StartZ=0 EndX=23.4789 EndY=5.55004 EndZ=0
    g34: LineSegment StartX=23.4789 StartY=5.55004 StartZ=0 EndX=23.244 EndY=5.64749 EndZ=0
    g35: LineSegment StartX=23.244 StartY=5.64749 StartZ=0 EndX=23.0141 EndY=5.77459 EndZ=0
    g36: LineSegment StartX=23.0141 StartY=5.77459 StartZ=0 EndX=22.81 EndY=5.91307 EndZ=0
    g37: LineSegment StartX=22.81 StartY=5.91307 StartZ=0 EndX=22.6171 EndY=6.07925 EndZ=0
    g38: LineSegment StartX=22.6171 StartY=6.07925 StartZ=0 EndX=22.4499 EndY=6.25158 EndZ=0
    g39: LineSegment StartX=22.4499 StartY=6.25158 StartZ=0 EndX=22.2897 EndY=6.45644 EndZ=0
    g40: LineSegment StartX=22.2897 StartY=6.45644 StartZ=0 EndX=22.1484 EndY=6.67133 EndZ=0
    g41: LineSegment StartX=22.1484 StartY=6.67133 StartZ=0 EndX=22.0413 EndY=6.89628 EndZ=0
    g42: LineSegment StartX=22.0413 StartY=6.89628 StartZ=0 EndX=21.9449 EndY=7.13041 EndZ=0
    g43: LineSegment StartX=21.9449 StartY=7.13041 StartZ=0 EndX=21.883 EndY=7.36574 EndZ=0
    g44: LineSegment StartX=21.883 StartY=7.36574 StartZ=0 EndX=21.842 EndY=7.61808 EndZ=0
    g45: LineSegment StartX=21.842 StartY=7.61808 StartZ=0 EndX=21.8244 EndY=7.88752 EndZ=0
    g46: LineSegment StartX=21.8244 StartY=7.88752 StartZ=0 EndX=21.8388 EndY=8.12242 EndZ=0
    g47: LineSegment StartX=21.8388 StartY=8.12242 StartZ=0 EndX=21.8716 EndY=8.3765 EndZ=0
    g48: LineSegment StartX=21.8716 StartY=8.3765 StartZ=0 EndX=21.9322 EndY=8.62371 EndZ=0
    g49: LineSegment StartX=21.9322 StartY=8.62371 StartZ=0 EndX=22.0085 EndY=8.85622 EndZ=0
    g50: LineSegment StartX=22.0085 StartY=8.85622 StartZ=0 EndX=22.1095 EndY=9.0873 EndZ=0
    g51: LineSegment StartX=22.1095 StartY=9.0873 StartZ=0 EndX=22.2564 EndY=9.30001 EndZ=0
    g52: LineSegment StartX=22.2564 StartY=9.30001 StartZ=0 EndX=22.4222 EndY=9.51816 EndZ=0
    g53: LineSegment StartX=22.4222 StartY=9.51816 StartZ=0 EndX=22.5814 EndY=9.69568 EndZ=0
    g54: LineSegment StartX=22.5814 StartY=9.69568 StartZ=0 EndX=22.7773 EndY=9.86401 EndZ=0
    g55: LineSegment StartX=22.7773 StartY=9.86401 StartZ=0 EndX=22.8829 EndY=9.96654 EndZ=0
    g56: LineSegment StartX=22.8829 StartY=9.96654 StartZ=0 EndX=22.9946 EndY=10.1027 EndZ=0
    g57: LineSegment StartX=22.9946 StartY=10.1027 StartZ=0 EndX=23.0728 EndY=10.2473 EndZ=0
    g58: LineSegment StartX=23.0728 StartY=10.2473 StartZ=0 EndX=23.1295 EndY=10.4111 EndZ=0
    g59: LineSegment StartX=23.1295 StartY=10.4111 StartZ=0 EndX=23.1555 EndY=10.5871 EndZ=0
    g60: LineSegment StartX=23.1555 StartY=10.5871 StartZ=0 EndX=23.1416 EndY=10.7621 EndZ=0
    g61: LineSegment StartX=23.1416 StartY=10.7621 StartZ=0 EndX=23.1095 EndY=10.9289 EndZ=0
    g62: LineSegment StartX=23.1095 StartY=10.9289 StartZ=0 EndX=23.0483 EndY=11.0865 EndZ=0
    g63: LineSegment StartX=23.0483 StartY=11.0865 StartZ=0 EndX=22.8718 EndY=11.4442 EndZ=0
    g64: LineSegment StartX=22.8718 StartY=11.4442 StartZ=0 EndX=22.5688 EndY=12.0257 EndZ=0
    g65: LineSegment StartX=22.5688 StartY=12.0257 StartZ=0 EndX=22.5075 EndY=12.152 EndZ=0
    g66: LineSegment StartX=22.5075 StartY=12.152 StartZ=0 EndX=22.4248 EndY=12.279 EndZ=0
    g67: LineSegment StartX=22.4248 StartY=12.279 StartZ=0 EndX=22.3208 EndY=12.3999 EndZ=0
    g68: LineSegment StartX=22.3208 StartY=12.3999 StartZ=0 EndX=22.1769 EndY=12.5009 EndZ=0
    g69: LineSegment StartX=22.1769 StartY=12.5009 StartZ=0 EndX=22.0254 EndY=12.5805 EndZ=0
    g70: LineSegment StartX=22.0254 StartY=12.5805 StartZ=0 EndX=21.8678 EndY=12.6325 EndZ=0
    g71: LineSegment StartX=21.8678 StartY=12.6325 StartZ=0 EndX=21.6949 EndY=12.6601 EndZ=0
    g72: LineSegment StartX=21.6949 StartY=12.6601 StartZ=0 EndX=21.5327 EndY=12.6555 EndZ=0
    g73: LineSegment StartX=21.5327 StartY=12.6555 StartZ=0 EndX=21.1061 EndY=12.5612 EndZ=0
    g74: LineSegment StartX=21.1061 StartY=12.5612 StartZ=0 EndX=20.8582 EndY=12.5352 EndZ=0
    g75: LineSegment StartX=20.8582 StartY=12.5352 StartZ=0 EndX=20.6087 EndY=12.5337 EndZ=0
    g76: LineSegment StartX=20.6087 StartY=12.5337 StartZ=0 EndX=20.3501 EndY=12.5536 EndZ=0
    g77: LineSegment StartX=20.3501 StartY=12.5536 StartZ=0 EndX=20.0854 EndY=12.5979 EndZ=0
    g78: LineSegment StartX=20.0854 StartY=12.5979 StartZ=0 EndX=19.8665 EndY=12.6699 EndZ=0
    g79: LineSegment StartX=19.8665 StartY=12.6699 StartZ=0 EndX=19.614 EndY=12.7678 EndZ=0
    g80: LineSegment StartX=19.614 StartY=12.7678 StartZ=0 EndX=19.4105 EndY=12.881 EndZ=0
    g81: LineSegment StartX=19.4105 StartY=12.881 StartZ=0 EndX=19.1993 EndY=13.0264 EndZ=0
    g82: LineSegment StartX=19.1993 StartY=13.0264 StartZ=0 EndX=18.9927 EndY=13.2018 EndZ=0
    g83: LineSegment StartX=18.9927 StartY=13.2018 StartZ=0 EndX=18.8259 EndY=13.3625 EndZ=0
    g84: LineSegment StartX=18.8259 StartY=13.3625 StartZ=0 EndX=18.6714 EndY=13.5553 EndZ=0
    g85: LineSegment StartX=18.6714 StartY=13.5553 StartZ=0 EndX=18.5367 EndY=13.768 EndZ=0
    g86: LineSegment StartX=18.5367 StartY=13.768 StartZ=0 EndX=18.4051 EndY=14.0083 EndZ=0
    g87: LineSegment StartX=18.4051 StartY=14.0083 StartZ=0 EndX=18.3225 EndY=14.2255 EndZ=0
    g88: LineSegment StartX=18.3225 StartY=14.2255 StartZ=0 EndX=18.2506 EndY=14.4903 EndZ=0
    g89: LineSegment StartX=18.2506 StartY=14.4903 StartZ=0 EndX=18.2154 EndY=14.7183 EndZ=0
    g90: LineSegment StartX=18.2154 StartY=14.7183 StartZ=0 EndX=18.2017 EndY=14.9876 EndZ=0
    g91: LineSegment StartX=18.2017 StartY=14.9876 StartZ=0 EndX=18.1828 EndY=15.2236 EndZ=0
    g92: LineSegment StartX=18.1828 StartY=15.2236 StartZ=0 EndX=18.2304 EndY=15.4722 EndZ=0
    g93: LineSegment StartX=18.2304 StartY=15.4722 StartZ=0 EndX=18.2815 EndY=15.714 EndZ=0
    g94: LineSegment StartX=18.2815 StartY=15.714 StartZ=0 EndX=18.3735 EndY=15.9865 EndZ=0
    g95: LineSegment StartX=18.3735 StartY=15.9865 StartZ=0 EndX=18.4796 EndY=16.216 EndZ=0
    g96: LineSegment StartX=18.4796 StartY=16.216 StartZ=0 EndX=18.6771 EndY=16.5429 EndZ=0
    g97: LineSegment StartX=18.6771 StartY=16.5429 StartZ=0 EndX=18.7452 EndY=16.7132 EndZ=0
    g98: LineSegment StartX=18.7452 StartY=16.7132 StartZ=0 EndX=18.7725 EndY=16.8562 EndZ=0
    g99: LineSegment StartX=18.7725 StartY=16.8562 StartZ=0 EndX=18.7793 EndY=17.0538 EndZ=0
    g100: LineSegment StartX=18.7793 StartY=17.0538 StartZ=0 EndX=18.7515 EndY=17.1989 EndZ=0
    g101: LineSegment StartX=18.7515 StartY=17.1989 StartZ=0 EndX=18.7073 EndY=17.3454 EndZ=0
    g102: LineSegment StartX=18.7073 StartY=17.3454 StartZ=0 EndX=18.6221 EndY=17.4986 EndZ=0
    g103: LineSegment StartX=18.6221 StartY=17.4986 StartZ=0 EndX=18.5404 EndY=17.6076 EndZ=0
    g104: LineSegment StartX=18.5404 StartY=17.6076 StartZ=0 EndX=18.4484 EndY=17.7132 EndZ=0
    g105: LineSegment StartX=18.4484 StartY=17.7132 StartZ=0 EndX=17.7843 EndY=18.3841 EndZ=0
    g106: LineSegment StartX=17.7843 StartY=18.3841 StartZ=0 EndX=17.6004 EndY=18.5476 EndZ=0
    g107: LineSegment StartX=17.6004 StartY=18.5476 StartZ=0 EndX=17.5187 EndY=18.6089 EndZ=0
    g108: LineSegment StartX=17.5187 StartY=18.6089 StartZ=0 EndX=17.3654 EndY=18.6872 EndZ=0
    g109: LineSegment StartX=17.3654 StartY=18.6872 StartZ=0 EndX=17.2156 EndY=18.7383 EndZ=0
    g110: LineSegment StartX=17.2156 StartY=18.7383 StartZ=0 EndX=17.0487 EndY=18.7621 EndZ=0
    g111: LineSegment StartX=17.0487 StartY=18.7621 StartZ=0 EndX=16.8852 EndY=18.7724 EndZ=0
    g112: LineSegment StartX=16.8852 StartY=18.7724 StartZ=0 EndX=16.7183 EndY=18.7417 EndZ=0
    g113: LineSegment StartX=16.7183 StartY=18.7417 StartZ=0 EndX=16.5651 EndY=18.694 EndZ=0
    g114: LineSegment StartX=16.5651 StartY=18.694 StartZ=0 EndX=16.3709 EndY=18.5851 EndZ=0
    g115: LineSegment StartX=16.3709 StartY=18.5851 StartZ=0 EndX=16.1496 EndY=18.4522 EndZ=0
    g116: LineSegment StartX=16.1496 StartY=18.4522 StartZ=0 EndX=15.9752 EndY=18.3739 EndZ=0
    g117: LineSegment StartX=15.9752 StartY=18.3739 StartZ=0 EndX=15.7423 EndY=18.2963 EndZ=0
    g118: LineSegment StartX=15.7423 StartY=18.2963 StartZ=0 EndX=15.5003 EndY=18.2233 EndZ=0
    g119: LineSegment StartX=15.5003 StartY=18.2233 StartZ=0 EndX=15.2492 EndY=18.1982 EndZ=0
    g120: LineSegment StartX=15.2492 StartY=18.1982 StartZ=0 EndX=14.973 EndY=18.2004 EndZ=0
    g121: LineSegment StartX=14.973 StartY=18.2004 StartZ=0 EndX=14.7241 EndY=18.2141 EndZ=0
    g122: LineSegment StartX=14.7241 StartY=18.2141 StartZ=0 EndX=14.4685 EndY=18.2484 EndZ=0
    g123: LineSegment StartX=14.4685 StartY=18.2484 StartZ=0 EndX=14.2265 EndY=18.3192 EndZ=0
    g124: LineSegment StartX=14.2265 StartY=18.3192 StartZ=0 EndX=13.9799 EndY=18.4196 EndZ=0
    g125: LineSegment StartX=13.9799 StartY=18.4196 StartZ=0 EndX=13.7736 EndY=18.5304 EndZ=0
    g126: LineSegment StartX=13.7736 StartY=18.5304 StartZ=0 EndX=13.5557 EndY=18.6666 EndZ=0
    g127: LineSegment StartX=13.5557 StartY=18.6666 StartZ=0 EndX=13.3683 EndY=18.8267 EndZ=0
    g128: LineSegment StartX=13.3683 StartY=18.8267 StartZ=0 EndX=13.1844 EndY=18.997 EndZ=0
    g129: LineSegment StartX=13.1844 StartY=18.997 StartZ=0 EndX=13.0175 EndY=19.2047 EndZ=0
    g130: LineSegment StartX=13.0175 StartY=19.2047 StartZ=0 EndX=12.9086 EndY=19.4227 EndZ=0
    g131: LineSegment StartX=12.9086 StartY=19.4227 StartZ=0 EndX=12.694 EndY=19.8518 EndZ=0
    g132: LineSegment StartX=12.694 StartY=19.8518 StartZ=0 EndX=12.5986 EndY=20.1266 EndZ=0
    g133: LineSegment StartX=12.5986 StartY=20.1266 StartZ=0 EndX=12.5373 EndY=20.3616 EndZ=0
    g134: LineSegment StartX=12.5373 StartY=20.3616 StartZ=0 EndX=12.5305 EndY=20.6613 EndZ=0
    g135: LineSegment StartX=12.5305 StartY=20.6613 StartZ=0 EndX=12.527 EndY=20.852 EndZ=0
    g136: LineSegment StartX=12.527 StartY=20.852 StartZ=0 EndX=12.5713 EndY=21.1177 EndZ=0
    g137: LineSegment StartX=12.5713 StartY=21.1177 StartZ=0 EndX=12.6565 EndY=21.5025 EndZ=0
    g138: LineSegment StartX=12.6565 StartY=21.5025 StartZ=0 EndX=12.6531 EndY=21.7205 EndZ=0
    g139: LineSegment StartX=12.6531 StartY=21.7205 StartZ=0 EndX=12.6258 EndY=21.8771 EndZ=0
    g140: LineSegment StartX=12.6258 StartY=21.8771 StartZ=0 EndX=12.5747 EndY=22.0542 EndZ=0
    g141: LineSegment StartX=12.5747 StartY=22.0542 StartZ=0 EndX=12.5027 EndY=22.1813 EndZ=0
    g142: LineSegment StartX=12.5027 StartY=22.1813 StartZ=0 EndX=12.3937 EndY=22.3278 EndZ=0
    g143: LineSegment StartX=12.3937 StartY=22.3278 StartZ=0 EndX=12.278 EndY=22.4299 EndZ=0
    g144: LineSegment StartX=12.278 StartY=22.4299 StartZ=0 EndX=12.1179 EndY=22.5287 EndZ=0
    g145: LineSegment StartX=12.1179 StartY=22.5287 StartZ=0 EndX=11.7535 EndY=22.716 EndZ=0
    g146: LineSegment StartX=11.7535 StartY=22.716 StartZ=0 EndX=11.2792 EndY=22.9552 EndZ=0
    g147: LineSegment StartX=11.2792 StartY=22.9552 StartZ=0 EndX=11.0374 EndY=23.0607 EndZ=0
    g148: LineSegment StartX=11.0374 StartY=23.0607 StartZ=0 EndX=10.8875 EndY=23.1289 EndZ=0
    g149: LineSegment StartX=10.8875 StartY=23.1289 StartZ=0 EndX=10.7036 EndY=23.1527 EndZ=0
    g150: LineSegment StartX=10.7036 StartY=23.1527 StartZ=0 EndX=10.5571 EndY=23.1391 EndZ=0
    g151: LineSegment StartX=10.5571 StartY=23.1391 StartZ=0 EndX=10.38 EndY=23.1084 EndZ=0
    g152: LineSegment StartX=10.38 StartY=23.1084 StartZ=0 EndX=10.2643 EndY=23.0641 EndZ=0
    g153: LineSegment StartX=10.2643 StartY=23.0641 StartZ=0 EndX=10.1042 EndY=22.9892 EndZ=0
    g154: LineSegment StartX=10.1042 StartY=22.9892 StartZ=0 EndX=9.97817 EndY=22.9041 EndZ=0
    g155: LineSegment StartX=9.97817 StartY=22.9041 StartZ=0 EndX=9.8181 EndY=22.727 EndZ=0
    g156: LineSegment StartX=9.8181 StartY=22.727 StartZ=0 EndX=9.68528 EndY=22.5839 EndZ=0
    g157: LineSegment StartX=9.68528 StartY=22.5839 StartZ=0 EndX=9.5184 EndY=22.4068 EndZ=0
    g158: LineSegment StartX=9.5184 StartY=22.4068 StartZ=0 EndX=9.29702 EndY=22.2672 EndZ=0
    g159: LineSegment StartX=9.29702 StartY=22.2672 StartZ=0 EndX=9.09042 EndY=22.1273 EndZ=0
    g160: LineSegment StartX=9.09042 StartY=22.1273 StartZ=0 EndX=8.85883 EndY=22.0183 EndZ=0
    g161: LineSegment StartX=8.85883 StartY=22.0183 StartZ=0 EndX=8.60681 EndY=21.9332 EndZ=0
    g162: LineSegment StartX=8.60681 StartY=21.9332 StartZ=0 EndX=8.36841 EndY=21.8719 EndZ=0
    g163: LineSegment StartX=8.36841 StartY=21.8719 StartZ=0 EndX=8.11979 EndY=21.8344 EndZ=0
    g164: LineSegment StartX=8.11979 StartY=21.8344 StartZ=0 EndX=7.84392 EndY=21.8242 EndZ=0
    g165: LineSegment StartX=7.84392 StartY=21.8242 StartZ=0 EndX=7.61915 EndY=21.8446 EndZ=0
    g166: LineSegment StartX=7.61915 StartY=21.8446 StartZ=0 EndX=7.39096 EndY=21.8753 EndZ=0
    g167: LineSegment StartX=7.39096 StartY=21.8753 StartZ=0 EndX=7.10488 EndY=21.9536 EndZ=0
    g168: LineSegment StartX=7.10488 StartY=21.9536 StartZ=0 EndX=6.8801 EndY=22.0387 EndZ=0
    g169: LineSegment StartX=6.8801 StartY=22.0387 StartZ=0 EndX=6.66554 EndY=22.1613 EndZ=0
    g170: LineSegment StartX=6.66554 StartY=22.1613 StartZ=0 EndX=6.44417 EndY=22.2908 EndZ=0
    g171: LineSegment StartX=6.44417 StartY=22.2908 StartZ=0 EndX=6.19215 EndY=22.5087 EndZ=0
    g172: LineSegment StartX=6.19215 StartY=22.5087 StartZ=0 EndX=6.02186 EndY=22.6688 EndZ=0
    g173: LineSegment StartX=6.02186 StartY=22.6688 StartZ=0 EndX=5.87882 EndY=22.8391 EndZ=0
    g174: LineSegment StartX=5.87882 StartY=22.8391 StartZ=0 EndX=5.74259 EndY=23.0809 EndZ=0
    g175: LineSegment StartX=5.74259 StartY=23.0809 StartZ=0 EndX=5.62679 EndY=23.2989 EndZ=0
    g176: LineSegment StartX=5.62679 StartY=23.2989 StartZ=0 EndX=5.54923 EndY=23.4812 EndZ=0
    g177: LineSegment StartX=5.54923 StartY=23.4812 StartZ=0 EndX=5.48987 EndY=23.7141 EndZ=0
    g178: LineSegment StartX=5.48987 StartY=23.7141 StartZ=0 EndX=5.43965 EndY=23.931 EndZ=0
    g179: LineSegment StartX=5.43965 StartY=23.931 StartZ=0 EndX=5.38283 EndY=24.3702 EndZ=0
    g180: LineSegment StartX=5.38283 StartY=24.3702 StartZ=0 EndX=5.34402 EndY=24.5505 EndZ=0
    g181: LineSegment StartX=5.34402 StartY=24.5505 StartZ=0 EndX=5.26412 EndY=24.7012 EndZ=0
    g182: LineSegment StartX=5.26412 StartY=24.7012 StartZ=0 EndX=5.15662 EndY=24.8433 EndZ=0
    g183: LineSegment StartX=5.15662 StartY=24.8433 StartZ=0 EndX=5.03563 EndY=24.9643 EndZ=0
    g184: LineSegment StartX=5.03563 StartY=24.9643 StartZ=0 EndX=4.9055 EndY=25.0534 EndZ=0
    g185: LineSegment StartX=4.9055 StartY=25.0534 StartZ=0 EndX=4.76168 EndY=25.115 EndZ=0
    g186: LineSegment StartX=4.76168 StartY=25.115 StartZ=0 EndX=4.56991 EndY=25.1698 EndZ=0
    g187: LineSegment StartX=4.56991 StartY=25.1698 StartZ=0 EndX=4.22291 EndY=25.2269 EndZ=0
    g188: LineSegment StartX=4.22291 StartY=25.2269 StartZ=0 EndX=3.72501 EndY=25.306 EndZ=0
    g189: LineSegment StartX=3.72501 StartY=25.306 StartZ=0 EndX=3.40823 EndY=25.3504 EndZ=0
    g190: LineSegment StartX=3.40823 StartY=25.3504 StartZ=0 EndX=3.25674 EndY=25.3565 EndZ=0
    g191: LineSegment StartX=3.25674 StartY=25.3565 StartZ=0 EndX=3.08534 EndY=25.3351 EndZ=0
    g192: LineSegment StartX=3.08534 StartY=25.3351 StartZ=0 EndX=2.91854 EndY=25.2876 EndZ=0
    g193: LineSegment StartX=2.91854 StartY=25.2876 StartZ=0 EndX=2.76092 EndY=25.2111 EndZ=0
    g194: LineSegment StartX=2.76092 StartY=25.2111 StartZ=0 EndX=2.62472 EndY=25.1116 EndZ=0
    g195: LineSegment StartX=2.62472 StartY=25.1116 StartZ=0 EndX=2.50842 EndY=24.9984 EndZ=0
    g196: LineSegment StartX=2.50842 StartY=24.9984 StartZ=0 EndX=2.41174 EndY=24.8483 EndZ=0
    g197: LineSegment StartX=2.41174 StartY=24.8483 StartZ=0 EndX=2.30308 EndY=24.582 EndZ=0
    g198: LineSegment StartX=2.30308 StartY=24.582 StartZ=0 EndX=2.25622 EndY=24.4788 EndZ=0
    g199: LineSegment StartX=2.25622 StartY=24.4788 StartZ=0 EndX=2.13227 EndY=24.2646 EndZ=0
    g200: LineSegment StartX=2.13227 StartY=24.2646 StartZ=0 EndX=1.96394 EndY=24.0365 EndZ=0
    g201: LineSegment StartX=1.96394 StartY=24.0365 StartZ=0 EndX=1.80479 EndY=23.856 EndZ=0
    g202: LineSegment StartX=1.80479 StartY=23.856 StartZ=0 EndX=1.62573 EndY=23.6797 EndZ=0
    g203: LineSegment StartX=1.62573 StartY=23.6797 StartZ=0 EndX=1.41955 EndY=23.5197 EndZ=0
    g204: LineSegment StartX=1.41955 StartY=23.5197 StartZ=0 EndX=1.20904 EndY=23.3867 EndZ=0
    g205: LineSegment StartX=1.20904 StartY=23.3867 StartZ=0 EndX=0.984393 EndY=23.2759 EndZ=0
    g206: LineSegment StartX=0.984393 StartY=23.2759 StartZ=0 EndX=0.742307 EndY=23.1856 EndZ=0
    g207: LineSegment StartX=0.742307 StartY=23.1856 StartZ=0 EndX=0.498622 EndY=23.1238 EndZ=0
    g208: LineSegment StartX=0.498622 StartY=23.1238 StartZ=0 EndX=0.250381 EndY=23.0889 EndZ=0
    g209: LineSegment StartX=0.250381 StartY=23.0889 StartZ=0 EndX=-0.006065 EndY=23.0756 EndZ=0
    g210: LineSegment StartX=-0.006065 StartY=23.0756 StartZ=0 EndX=0 EndY=0 EndZ=0
  constraints (212):
    c: Coincident(g0,g1)
    c: Coincident(g1,g2)
    c: Coincident(g2,g3)
    c: Coincident(g3,g4)
    c: Coincident(g4,g5)
    c: Coincident(g5,g6)
    c: Coincident(g6,g7)
    c: Coincident(g7,g8)
    c: Coincident(g8,g9)
    c: Coincident(g9,g10)
    c: Coincident(g10,g11)
    c: Coincident(g11,g12)
    c: Coincident(g12,g13)
    c: Coincident(g13,g14)
    c: Coincident(g14,g15)
    c: Coincident(g15,g16)
    c: Coincident(g16,g17)
    c: Coincident(g17,g18)
    c: Coincident(g18,g19)
    c: Coincident(g19,g20)
    c: Coincident(g20,g21)
    c: Coincident(g21,g22)
    c: Coincident(g22,g23)
    c: Coincident(g23,g24)
    c: Coincident(g24,g25)
    c: Coincident(g25,g26)
    c: Coincident(g26,g27)
    c: Coincident(g27,g28)
    c: Coincident(g28,g29)
    c: Coincident(g29,g30)
    c: Coincident(g30,g31)
    c: Coincident(g31,g32)
    c: Coincident(g32,g33)
    c: Coincident(g33,g34)
    c: Coincident(g34,g35)
    c: Coincident(g35,g36)
    c: Coincident(g36,g37)
    c: Coincident(g37,g38)
    c: Coincident(g38,g39)
    c: Coincident(g39,g40)
    c: Coincident(g40,g41)
    c: Coincident(g41,g42)
    c: Coincident(g42,g43)
    c: Coincident(g43,g44)
    c: Coincident(g44,g45)
    c: Coincident(g45,g46)
    c: Coincident(g46,g47)
    c: Coincident(g47,g48)
    c: Coincident(g48,g49)
    c: Coincident(g49,g50)
    c: Coincident(g50,g51)
    c: Coincident(g51,g52)
    c: Coincident(g52,g53)
    c: Coincident(g53,g54)
    c: Coincident(g54,g55)
    c: Coincident(g55,g56)
    c: Coincident(g56,g57)
    c: Coincident(g57,g58)
    c: Coincident(g58,g59)
    c: Coincident(g59,g60)
    c: Coincident(g60,g61)
    c: Coincident(g61,g62)
    c: Coincident(g62,g63)
    c: Coincident(g63,g64)
    c: Coincident(g64,g65)
    c: Coincident(g65,g66)
    c: Coincident(g66,g67)
    c: Coincident(g67,g68)
    c: Coincident(g68,g69)
    c: Coincident(g69,g70)
    c: Coincident(g70,g71)
    c: Coincident(g71,g72)
    c: Coincident(g72,g73)
    c: Coincident(g73,g74)
    c: Coincident(g74,g75)
    c: Coincident(g75,g76)
    c: Coincident(g76,g77)
    c: Coincident(g77,g78)
    c: Coincident(g78,g79)
    c: Coincident(g79,g80)
    c: Coincident(g80,g81)
    c: Coincident(g81,g82)
    c: Coincident(g82,g83)
    c: Coincident(g83,g84)
    c: Coincident(g84,g85)
    c: Coincident(g85,g86)
    c: Coincident(g86,g87)
    c: Coincident(g87,g88)
    c: Coincident(g88,g89)
    c: Coincident(g89,g90)
    c: Coincident(g90,g91)
    c: Coincident(g91,g92)
    c: Coincident(g92,g93)
    c: Coincident(g93,g94)
    c: Coincident(g94,g95)
    c: Coincident(g95,g96)
    c: Coincident(g96,g97)
    c: Coincident(g97,g98)
    c: Coincident(g98,g99)
    c: Coincident(g99,g100)
    c: Coincident(g100,g101)
    c: Coincident(g101,g102)
    c: Coincident(g102,g103)
    c: Coincident(g103,g104)
    c: Coincident(g104,g105)
    c: Coincident(g105,g106)
    c: Coincident(g106,g107)
    c: Coincident(g107,g108)
    c: Coincident(g108,g109)
    c: Coincident(g109,g110)
    c: Coincident(g110,g111)
    c: Coincident(g111,g112)
    c: Coincident(g112,g113)
    c: Coincident(g113,g114)
    c: Coincident(g114,g115)
    c: Coincident(g115,g116)
    c: Coincident(g116,g117)
    c: Coincident(g117,g118)
    c: Coincident(g118,g119)
    c: Coincident(g119,g120)
    c: Coincident(g120,g121)
    c: Coincident(g121,g122)
    c: Coincident(g122,g123)
    c: Coincident(g123,g124)
    c: Coincident(g124,g125)
    c: Coincident(g125,g126)
    c: Coincident(g126,g127)
    c: Coincident(g127,g128)
    c: Coincident(g128,g129)
    c: Coincident(g129,g130)
    c: Coincident(g130,g131)
    c: Coincident(g131,g132)
    c: Coincident(g132,g133)
    c: Coincident(g133,g134)
    c: Coincident(g134,g135)
    c: Coincident(g135,g136)
    c: Coincident(g136,g137)
    c: Coincident(g137,g138)
    c: Coincident(g138,g139)
    c: Coincident(g139,g140)
    c: Coincident(g140,g141)
    c: Coincident(g141,g142)
    c: Coincident(g142,g143)
    c: Coincident(g143,g144)
    c: Coincident(g144,g145)
    c: Coincident(g145,g146)
    c: Coincident(g146,g147)
    c: Coincident(g147,g148)
    c: Coincident(g148,g149)
    c: Coincident(g149,g150)
    c: Coincident(g150,g151)
    c: Coincident(g151,g152)
    c: Coincident(g152,g153)
    c: Coincident(g153,g154)
    c: Coincident(g154,g155)
    c: Coincident(g155,g156)
    c: Coincident(g156,g157)
    c: Coincident(g157,g158)
    c: Coincident(g158,g159)
    c: Coincident(g159,g160)
    c: Coincident(g160,g161)
    c: Coincident(g161,g162)
    c: Coincident(g162,g163)
    c: Coincident(g163,g164)
    c: Coincident(g164,g165)
    c: Coincident(g165,g166)
    c: Coincident(g166,g167)
    c: Coincident(g167,g168)
    c: Coincident(g168,g169)
    c: Coincident(g169,g170)
    c: Coincident(g170,g171)
    c: Coincident(g171,g172)
    c: Coincident(g172,g173)
    c: Coincident(g173,g174)
    c: Coincident(g174,g175)
    c: Coincident(g175,g176)
    c: Coincident(g176,g177)
    c: Coincident(g177,g178)
    c: Coincident(g178,g179)
    c: Coincident(g179,g180)
    c: Coincident(g180,g181)
    c: Coincident(g181,g182)
    c: Coincident(g182,g183)
    c: Coincident(g183,g184)
    c: Coincident(g184,g185)
    c: Coincident(g185,g186)
    c: Coincident(g186,g187)
    c: Coincident(g187,g188)
    c: Coincident(g188,g189)
    c: Coincident(g189,g190)
    c: Coincident(g190,g191)
    c: Coincident(g191,g192)
    c: Coincident(g192,g193)
    c: Coincident(g193,g194)
    c: Coincident(g194,g195)
    c: Coincident(g195,g196)
    c: Coincident(g196,g197)
    c: Coincident(g197,g198)
    c: Coincident(g198,g199)
    c: Coincident(g199,g200)
    c: Coincident(g200,g201)
    c: Coincident(g201,g202)
    c: Coincident(g202,g203)
    c: Coincident(g203,g204)
    c: Coincident(g204,g205)
    c: Coincident(g205,g206)
    c: Coincident(g206,g207)
    c: Coincident(g207,g208)
    c: Coincident(g208,g209)
    c: Coincident(g0,g210)
    c: Coincident(g0,g-1)
    c: Coincident(g209,g210)
FEATURE [PartDesign::Pad] Pad022
  Length = 2.5
  Length2 = 100
  Placement = pos=(0,0,0) rot=(0.57735,0.57735,0.57735;2.0944rad)
  Profile = -> Sketch035
  Type = 0
FEATURE [PartDesign::PolarPattern] PolarPattern015
  Angle = 360
  Axis = -> Sketch035 [N_Axis]
  BaseFeature = -> Pad022
  Occurrences = 4
  Originals = -> [Pad022]
  Placement = pos=(0,0,0) rot=(0.57735,0.57735,0.57735;2.0944rad)
FEATURE [PartDesign::Pocket] Pocket002
  BaseFeature = -> PolarPattern015
  Length = 1
  Length2 = 100
  Placement = pos=(0,0,0) rot=(0.57735,0.57735,0.57735;2.0944rad)
  Profile = -> Sketch033
  Reversed = true
  Type = 1
FEATURE [PartDesign::PolarPattern] PolarPattern016
  Angle = 360
  Axis = -> Sketch033 [N_Axis]
  BaseFeature = -> Pocket002
  Occurrences = 2
  Originals = -> [Pocket002]
  Placement = pos=(0,0,0) rot=(0.57735,0.57735,0.57735;2.0944rad)
FEATURE [Sketcher::SketchObject] Sketch036
  MapMode = 5
  Placement = pos=(0,0,0) rot=(0.57735,0.57735,-0.57735;4.18879rad)
  Support = -> [PolarPattern015]
FEATURE [Sketcher::SketchObject] Sketch037
  MapMode = 5
  Placement = pos=(0,0,0) rot=(0.57735,0.57735,0.57735;2.0944rad)
  Support = -> [YZ_Plane017]
  sketch-geometry (20):
    g0: LineSegment StartX=1.84977 StartY=-2.03462 StartZ=0 EndX=1.64219 EndY=-2.20542 EndZ=0
    g1: LineSegment StartX=1.64219 StartY=-2.20542 StartZ=0 EndX=1.4178 EndY=-2.35642 EndZ=0
    g2: LineSegment StartX=1.4178 StartY=-2.35642 StartZ=0 EndX=1.1786 EndY=-2.48192 EndZ=0
    g3: LineSegment StartX=1.1786 StartY=-2.48192 StartZ=0 EndX=0.933165 EndY=-2.58946 EndZ=0
    g4: LineSegment StartX=0.933165 StartY=-2.58946 StartZ=0 EndX=0.669297 EndY=-2.66615 EndZ=0
    g5: LineSegment StartX=0.669297 StartY=-2.66615 StartZ=0 EndX=0.401357 EndY=-2.72007 EndZ=0
    g6: LineSegment StartX=0.401357 StartY=-2.72007 StartZ=0 EndX=0.133198 EndY=-2.74689 EndZ=0
    g7: LineSegment StartX=0.133198 StartY=-2.74689 StartZ=0 EndX=-0.13715 EndY=-2.74708 EndZ=0
    g8: LineSegment StartX=-0.13715 StartY=-2.74708 StartZ=0 EndX=-0.688499 EndY=-2.66151 EndZ=0
    g9: LineSegment StartX=-0.688499 StartY=-2.66151 StartZ=0 EndX=-0.94393 EndY=-2.58392 EndZ=0
    g10: LineSegment StartX=-0.94393 StartY=-2.58392 StartZ=0 EndX=-1.18786 EndY=-2.4818 EndZ=0
    g11: LineSegment StartX=-1.18786 StartY=-2.4818 StartZ=0 EndX=-1.42897 EndY=-2.34335 EndZ=0
    g12: LineSegment StartX=-1.42897 StartY=-2.34335 StartZ=0 EndX=-1.64859 EndY=-2.19653 EndZ=0
    g13: LineSegment StartX=-1.64859 StartY=-2.19653 StartZ=0 EndX=-1.84554 EndY=-2.0342 EndZ=0
    g14: LineSegment StartX=-1.84554 StartY=-2.0342 StartZ=0 EndX=-1.84465 EndY=-1.22163 EndZ=0
    g15: LineSegment StartX=-1.84465 StartY=-1.22163 StartZ=0 EndX=-1.84999 EndY=-0.000151 EndZ=0
    g16: LineSegment StartX=-1.84999 StartY=-0.000151 StartZ=0 EndX=-1.85002 EndY=0.00099 EndZ=0
    g17: LineSegment StartX=-1.85002 StartY=0.00099 StartZ=0 EndX=1.85015 EndY=0.005067 EndZ=0
    g18: LineSegment StartX=1.84931 StartY=-2.02283 StartZ=0 EndX=1.84977 EndY=-2.03462 EndZ=0
    g19: LineSegment StartX=1.85015 StartY=0.005067 StartZ=0 EndX=1.84931 EndY=-2.02283 EndZ=0
  constraints (20):
    c: Coincident(g0,g1)
    c: Coincident(g1,g2)
    c: Coincident(g2,g3)
    c: Coincident(g3,g4)
    c: Coincident(g4,g5)
    c: Coincident(g5,g6)
    c: Coincident(g8,g9)
    c: Coincident(g9,g10)
    c: Coincident(g10,g11)
    c: Coincident(g11,g12)
    c: Coincident(g12,g13)
    c: Coincident(g13,g14)
    c: Coincident(g14,g15)
    c: Coincident(g15,g16)
    c: Coincident(g16,g17)
    c: Coincident(g0,g18)
    c: Coincident(g7,g8)
    c: Coincident(g6,g7)
    c: Coincident(g18,g19)
    c: Coincident(g17,g19)
FEATURE [Sketcher::SketchObject] Sketch038
  MapMode = 5
  Placement = pos=(0,0,0) rot=(0.57735,0.57735,-0.57735;4.18879rad)
  Support = -> [PolarPattern016]
  sketch-geometry (2):
    g0: Circle CenterX=0 CenterY=0 CenterZ=0 NormalX=0 NormalY=0 NormalZ=1 AngleXU=0 Radius=22.57
    g1: Circle CenterX=0 CenterY=0 CenterZ=0 NormalX=0 NormalY=0 NormalZ=1 AngleXU=0 Radius=2.75498
  constraints (3):
    c: Coincident(g1,g0)
    c: Coincident(g-1,g0)
    c: Radius(g0) = 22.57
FEATURE [PartDesign::Pad] Pad023
  BaseFeature = -> PolarPattern016
  Length = 5.5
  Length2 = 100
  Placement = pos=(0,0,0) rot=(0.57735,0.57735,0.57735;2.0944rad)
  Profile = -> Sketch038
  Type = 0
FEATURE [Sketcher::SketchObject] Sketch039
  MapMode = 5
  Placement = pos=(-5.5,3.7e-15,-3.7e-15) rot=(0.57735,0.57735,-0.57735;4.18879rad)
  Support = -> [Pad023]
  sketch-geometry (2):
    g0: Circle CenterX=0 CenterY=0 CenterZ=0 NormalX=0 NormalY=0 NormalZ=1 AngleXU=0 Radius=2.77794
    g1: Circle CenterX=0 CenterY=0 CenterZ=0 NormalX=0 NormalY=0 NormalZ=1 AngleXU=0 Radius=17
  constraints (3):
    c: Coincident(g0,g1)
    c: Coincident(g0,g-1)
    c: Radius(g1) = 17
FEATURE [Sketcher::SketchObject] Sketch040
  MapMode = 5
  Placement = pos=(0,0,0) rot=(0.57735,0.57735,0.57735;2.0944rad)
  Support = -> [YZ_Plane017]
  sketch-geometry (211):
    g0: LineSegment StartX=0 StartY=0 StartZ=0 EndX=23.0775 EndY=-0.007725 EndZ=0
    g1: LineSegment StartX=23.0775 StartY=-0.007725 StartZ=0 EndX=23.0915 EndY=0.254478 EndZ=0
    g2: LineSegment StartX=23.0915 StartY=0.254478 StartZ=0 EndX=23.1284 EndY=0.508391 EndZ=0
    g3: LineSegment StartX=23.1284 StartY=0.508391 StartZ=0 EndX=23.1869 EndY=0.740712 EndZ=0
    g4: LineSegment StartX=23.1869 StartY=0.740712 StartZ=0 EndX=23.2782 EndY=0.973565 EndZ=0
    g5: LineSegment StartX=23.2782 StartY=0.973565 StartZ=0 EndX=23.3963 EndY=1.22031 EndZ=0
    g6: LineSegment StartX=23.3963 StartY=1.22031 StartZ=0 EndX=23.5215 EndY=1.42239 EndZ=0
    g7: LineSegment StartX=23.5215 StartY=1.42239 StartZ=0 EndX=23.6745 EndY=1.62203 EndZ=0
    g8: LineSegment StartX=23.6745 StartY=1.62203 StartZ=0 EndX=23.8622 EndY=1.81795 EndZ=0
    g9: LineSegment StartX=23.8622 StartY=1.81795 StartZ=0 EndX=24.0428 EndY=1.97182 EndZ=0
    g10: LineSegment StartX=24.0428 StartY=1.97182 StartZ=0 EndX=24.2535 EndY=2.11914 EndZ=0
    g11: LineSegment StartX=24.2535 StartY=2.11914 StartZ=0 EndX=24.4771 EndY=2.24429 EndZ=0
    g12: LineSegment StartX=24.4771 StartY=2.24429 StartZ=0 EndX=24.7643 EndY=2.36841 EndZ=0
    g13: LineSegment StartX=24.7643 StartY=2.36841 StartZ=0 EndX=24.8553 EndY=2.41105 EndZ=0
    g14: LineSegment StartX=24.8553 StartY=2.41105 StartZ=0 EndX=24.9955 EndY=2.50386 EndZ=0
    g15: LineSegment StartX=24.9955 StartY=2.50386 StartZ=0 EndX=25.1151 EndY=2.62736 EndZ=0
    g16: LineSegment StartX=25.1151 StartY=2.62736 StartZ=0 EndX=25.2142 EndY=2.76003 EndZ=0
    g17: LineSegment StartX=25.2142 StartY=2.76003 StartZ=0 EndX=25.2969 EndY=2.93426 EndZ=0
    g18: LineSegment StartX=25.2969 StartY=2.93426 StartZ=0 EndX=25.3426 EndY=3.08419 EndZ=0
    g19: LineSegment StartX=25.3426 StartY=3.08419 StartZ=0 EndX=25.3551 EndY=3.24413 EndZ=0
    g20: LineSegment StartX=25.3551 StartY=3.24413 StartZ=0 EndX=25.349 EndY=3.41794 EndZ=0
    g21: LineSegment StartX=25.349 StartY=3.41794 StartZ=0 EndX=25.3326 EndY=3.53796 EndZ=0
    g22: LineSegment StartX=25.3326 StartY=3.53796 StartZ=0 EndX=25.2546 EndY=4.05249 EndZ=0
    g23: LineSegment StartX=25.2546 StartY=4.05249 StartZ=0 EndX=25.1642 EndY=4.58451 EndZ=0
    g24: LineSegment StartX=25.1642 StartY=4.58451 StartZ=0 EndX=25.1211 EndY=4.74519 EndZ=0
    g25: LineSegment StartX=25.1211 StartY=4.74519 StartZ=0 EndX=25.0493 EndY=4.90009 EndZ=0
    g26: LineSegment StartX=25.0493 StartY=4.90009 StartZ=0 EndX=24.9559 EndY=5.03652 EndZ=0
    g27: LineSegment StartX=24.9559 StartY=5.03652 StartZ=0 EndX=24.8359 EndY=5.16166 EndZ=0
    g28: LineSegment StartX=24.8359 StartY=5.16166 StartZ=0 EndX=24.7064 EndY=5.26066 EndZ=0
    g29: LineSegment StartX=24.7064 StartY=5.26066 StartZ=0 EndX=24.5515 EndY=5.33657 EndZ=0
    g30: LineSegment StartX=24.5515 StartY=5.33657 StartZ=0 EndX=24.3854 EndY=5.38889 EndZ=0
    g31: LineSegment StartX=24.3854 StartY=5.38889 StartZ=0 EndX=23.9661 EndY=5.429 EndZ=0
    g32: LineSegment StartX=23.9661 StartY=5.429 StartZ=0 EndX=23.7168 EndY=5.47721 EndZ=0
    g33: LineSegment StartX=23.7168 StartY=5.47721 StartZ=0 EndX=23.4789 EndY=5.55004 EndZ=0
    g34: LineSegment StartX=23.4789 StartY=5.55004 StartZ=0 EndX=23.244 EndY=5.64749 EndZ=0
    g35: LineSegment StartX=23.244 StartY=5.64749 StartZ=0 EndX=23.0141 EndY=5.77459 EndZ=0
    g36: LineSegment StartX=23.0141 StartY=5.77459 StartZ=0 EndX=22.81 EndY=5.91307 EndZ=0
    g37: LineSegment StartX=22.81 StartY=5.91307 StartZ=0 EndX=22.6171 EndY=6.07925 EndZ=0
    g38: LineSegment StartX=22.6171 StartY=6.07925 StartZ=0 EndX=22.4499 EndY=6.25158 EndZ=0
    g39: LineSegment StartX=22.4499 StartY=6.25158 StartZ=0 EndX=22.2897 EndY=6.45644 EndZ=0
    g40: LineSegment StartX=22.2897 StartY=6.45644 StartZ=0 EndX=22.1484 EndY=6.67133 EndZ=0
    g41: LineSegment StartX=22.1484 StartY=6.67133 StartZ=0 EndX=22.0413 EndY=6.89628 EndZ=0
    g42: LineSegment StartX=22.0413 StartY=6.89628 StartZ=0 EndX=21.9449 EndY=7.13041 EndZ=0
    g43: LineSegment StartX=21.9449 StartY=7.13041 StartZ=0 EndX=21.883 EndY=7.36574 EndZ=0
    g44: LineSegment StartX=21.883 StartY=7.36574 StartZ=0 EndX=21.842 EndY=7.61808 EndZ=0
    g45: LineSegment StartX=21.842 StartY=7.61808 StartZ=0 EndX=21.8244 EndY=7.88752 EndZ=0
    g46: LineSegment StartX=21.8244 StartY=7.88752 StartZ=0 EndX=21.8388 EndY=8.12242 EndZ=0
    g47: LineSegment StartX=21.8388 StartY=8.12242 StartZ=0 EndX=21.8716 EndY=8.3765 EndZ=0
    g48: LineSegment StartX=21.8716 StartY=8.3765 StartZ=0 EndX=21.9322 EndY=8.62371 EndZ=0
    g49: LineSegment StartX=21.9322 StartY=8.62371 StartZ=0 EndX=22.0085 EndY=8.85622 EndZ=0
    g50: LineSegment StartX=22.0085 StartY=8.85622 StartZ=0 EndX=22.1095 EndY=9.0873 EndZ=0
    g51: LineSegment StartX=22.1095 StartY=9.0873 StartZ=0 EndX=22.2564 EndY=9.30001 EndZ=0
    g52: LineSegment StartX=22.2564 StartY=9.30001 StartZ=0 EndX=22.4222 EndY=9.51816 EndZ=0
    g53: LineSegment StartX=22.4222 StartY=9.51816 StartZ=0 EndX=22.5814 EndY=9.69568 EndZ=0
    g54: LineSegment StartX=22.5814 StartY=9.69568 StartZ=0 EndX=22.7773 EndY=9.86401 EndZ=0
    g55: LineSegment StartX=22.7773 StartY=9.86401 StartZ=0 EndX=22.8829 EndY=9.96654 EndZ=0
    g56: LineSegment StartX=22.8829 StartY=9.96654 StartZ=0 EndX=22.9946 EndY=10.1027 EndZ=0
    g57: LineSegment StartX=22.9946 StartY=10.1027 StartZ=0 EndX=23.0728 EndY=10.2473 EndZ=0
    g58: LineSegment StartX=23.0728 StartY=10.2473 StartZ=0 EndX=23.1295 EndY=10.4111 EndZ=0
    g59: LineSegment StartX=23.1295 StartY=10.4111 StartZ=0 EndX=23.1555 EndY=10.5871 EndZ=0
    g60: LineSegment StartX=23.1555 StartY=10.5871 StartZ=0 EndX=23.1416 EndY=10.7621 EndZ=0
    g61: LineSegment StartX=23.1416 StartY=10.7621 StartZ=0 EndX=23.1095 EndY=10.9289 EndZ=0
    g62: LineSegment StartX=23.1095 StartY=10.9289 StartZ=0 EndX=23.0483 EndY=11.0865 EndZ=0
    g63: LineSegment StartX=23.0483 StartY=11.0865 StartZ=0 EndX=22.8718 EndY=11.4442 EndZ=0
    g64: LineSegment StartX=22.8718 StartY=11.4442 StartZ=0 EndX=22.5688 EndY=12.0257 EndZ=0
    g65: LineSegment StartX=22.5688 StartY=12.0257 StartZ=0 EndX=22.5075 EndY=12.152 EndZ=0
    g66: LineSegment StartX=22.5075 StartY=12.152 StartZ=0 EndX=22.4248 EndY=12.279 EndZ=0
    g67: LineSegment StartX=22.4248 StartY=12.279 StartZ=0 EndX=22.3208 EndY=12.3999 EndZ=0
    g68: LineSegment StartX=22.3208 StartY=12.3999 StartZ=0 EndX=22.1769 EndY=12.5009 EndZ=0
    g69: LineSegment StartX=22.1769 StartY=12.5009 StartZ=0 EndX=22.0254 EndY=12.5805 EndZ=0
    g70: LineSegment StartX=22.0254 StartY=12.5805 StartZ=0 EndX=21.8678 EndY=12.6325 EndZ=0
    g71: LineSegment StartX=21.8678 StartY=12.6325 StartZ=0 EndX=21.6949 EndY=12.6601 EndZ=0
    g72: LineSegment StartX=21.6949 StartY=12.6601 StartZ=0 EndX=21.5327 EndY=12.6555 EndZ=0
    g73: LineSegment StartX=21.5327 StartY=12.6555 StartZ=0 EndX=21.1061 EndY=12.5612 EndZ=0
    g74: LineSegment StartX=21.1061 StartY=12.5612 StartZ=0 EndX=20.8582 EndY=12.5352 EndZ=0
    g75: LineSegment StartX=20.8582 StartY=12.5352 StartZ=0 EndX=20.6087 EndY=12.5337 EndZ=0
    g76: LineSegment StartX=20.6087 StartY=12.5337 StartZ=0 EndX=20.3501 EndY=12.5536 EndZ=0
    g77: LineSegment StartX=20.3501 StartY=12.5536 StartZ=0 EndX=20.0854 EndY=12.5979 EndZ=0
    g78: LineSegment StartX=20.0854 StartY=12.5979 StartZ=0 EndX=19.8665 EndY=12.6699 EndZ=0
    g79: LineSegment StartX=19.8665 StartY=12.6699 StartZ=0 EndX=19.614 EndY=12.7678 EndZ=0
    g80: LineSegment StartX=19.614 StartY=12.7678 StartZ=0 EndX=19.4105 EndY=12.881 EndZ=0
    g81: LineSegment StartX=19.4105 StartY=12.881 StartZ=0 EndX=19.1993 EndY=13.0264 EndZ=0
    g82: LineSegment StartX=19.1993 StartY=13.0264 StartZ=0 EndX=18.9927 EndY=13.2018 EndZ=0
    g83: LineSegment StartX=18.9927 StartY=13.2018 StartZ=0 EndX=18.8259 EndY=13.3625 EndZ=0
    g84: LineSegment StartX=18.8259 StartY=13.3625 StartZ=0 EndX=18.6714 EndY=13.5553 EndZ=0
    g85: LineSegment StartX=18.6714 StartY=13.5553 StartZ=0 EndX=18.5367 EndY=13.768 EndZ=0
    g86: LineSegment StartX=18.5367 StartY=13.768 StartZ=0 EndX=18.4051 EndY=14.0083 EndZ=0
    g87: LineSegment StartX=18.4051 StartY=14.0083 StartZ=0 EndX=18.3225 EndY=14.2255 EndZ=0
    g88: LineSegment StartX=18.3225 StartY=14.2255 StartZ=0 EndX=18.2506 EndY=14.4903 EndZ=0
    g89: LineSegment StartX=18.2506 StartY=14.4903 StartZ=0 EndX=18.2154 EndY=14.7183 EndZ=0
    g90: LineSegment StartX=18.2154 StartY=14.7183 StartZ=0 EndX=18.2017 EndY=14.9876 EndZ=0
    g91: LineSegment StartX=18.2017 StartY=14.9876 StartZ=0 EndX=18.1828 EndY=15.2236 EndZ=0
    g92: LineSegment StartX=18.1828 StartY=15.2236 StartZ=0 EndX=18.2304 EndY=15.4722 EndZ=0
    g93: LineSegment StartX=18.2304 StartY=15.4722 StartZ=0 EndX=18.2815 EndY=15.714 EndZ=0
    g94: LineSegment StartX=18.2815 StartY=15.714 StartZ=0 EndX=18.3735 EndY=15.9865 EndZ=0
    g95: LineSegment StartX=18.3735 StartY=15.9865 StartZ=0 EndX=18.4796 EndY=16.216 EndZ=0
    g96: LineSegment StartX=18.4796 StartY=16.216 StartZ=0 EndX=18.6771 EndY=16.5429 EndZ=0
    g97: LineSegment StartX=18.6771 StartY=16.5429 StartZ=0 EndX=18.7452 EndY=16.7132 EndZ=0
    g98: LineSegment StartX=18.7452 StartY=16.7132 StartZ=0 EndX=18.7725 EndY=16.8562 EndZ=0
    g99: LineSegment StartX=18.7725 StartY=16.8562 StartZ=0 EndX=18.7793 EndY=17.0538 EndZ=0
    g100: LineSegment StartX=18.7793 StartY=17.0538 StartZ=0 EndX=18.7515 EndY=17.1989 EndZ=0
    g101: LineSegment StartX=18.7515 StartY=17.1989 StartZ=0 EndX=18.7073 EndY=17.3454 EndZ=0
    g102: LineSegment StartX=18.7073 StartY=17.3454 StartZ=0 EndX=18.6221 EndY=17.4986 EndZ=0
    g103: LineSegment StartX=18.6221 StartY=17.4986 StartZ=0 EndX=18.5404 EndY=17.6076 EndZ=0
    g104: LineSegment StartX=18.5404 StartY=17.6076 StartZ=0 EndX=18.4484 EndY=17.7132 EndZ=0
    g105: LineSegment StartX=18.4484 StartY=17.7132 StartZ=0 EndX=17.7843 EndY=18.3841 EndZ=0
    g106: LineSegment StartX=17.7843 StartY=18.3841 StartZ=0 EndX=17.6004 EndY=18.5476 EndZ=0
    g107: LineSegment StartX=17.6004 StartY=18.5476 StartZ=0 EndX=17.5187 EndY=18.6089 EndZ=0
    g108: LineSegment StartX=17.5187 StartY=18.6089 StartZ=0 EndX=17.3654 EndY=18.6872 EndZ=0
    g109: LineSegment StartX=17.3654 StartY=18.6872 StartZ=0 EndX=17.2156 EndY=18.7383 EndZ=0
    g110: LineSegment StartX=17.2156 StartY=18.7383 StartZ=0 EndX=17.0487 EndY=18.7621 EndZ=0
    g111: LineSegment StartX=17.0487 StartY=18.7621 StartZ=0 EndX=16.8852 EndY=18.7724 EndZ=0
    g112: LineSegment StartX=16.8852 StartY=18.7724 StartZ=0 EndX=16.7183 EndY=18.7417 EndZ=0
    g113: LineSegment StartX=16.7183 StartY=18.7417 StartZ=0 EndX=16.5651 EndY=18.694 EndZ=0
    g114: LineSegment StartX=16.5651 StartY=18.694 StartZ=0 EndX=16.3709 EndY=18.5851 EndZ=0
    g115: LineSegment StartX=16.3709 StartY=18.5851 StartZ=0 EndX=16.1496 EndY=18.4522 EndZ=0
    g116: LineSegment StartX=16.1496 StartY=18.4522 StartZ=0 EndX=15.9752 EndY=18.3739 EndZ=0
    g117: LineSegment StartX=15.9752 StartY=18.3739 StartZ=0 EndX=15.7423 EndY=18.2963 EndZ=0
    g118: LineSegment StartX=15.7423 StartY=18.2963 StartZ=0 EndX=15.5003 EndY=18.2233 EndZ=0
    g119: LineSegment StartX=15.5003 StartY=18.2233 StartZ=0 EndX=15.2492 EndY=18.1982 EndZ=0
    g120: LineSegment StartX=15.2492 StartY=18.1982 StartZ=0 EndX=14.973 EndY=18.2004 EndZ=0
    g121: LineSegment StartX=14.973 StartY=18.2004 StartZ=0 EndX=14.7241 EndY=18.2141 EndZ=0
    g122: LineSegment StartX=14.7241 StartY=18.2141 StartZ=0 EndX=14.4685 EndY=18.2484 EndZ=0
    g123: LineSegment StartX=14.4685 StartY=18.2484 StartZ=0 EndX=14.2265 EndY=18.3192 EndZ=0
    g124: LineSegment StartX=14.2265 StartY=18.3192 StartZ=0 EndX=13.9799 EndY=18.4196 EndZ=0
    g125: LineSegment StartX=13.9799 StartY=18.4196 StartZ=0 EndX=13.7736 EndY=18.5304 EndZ=0
    g126: LineSegment StartX=13.7736 StartY=18.5304 StartZ=0 EndX=13.5557 EndY=18.6666 EndZ=0
    g127: LineSegment StartX=13.5557 StartY=18.6666 StartZ=0 EndX=13.3683 EndY=18.8267 EndZ=0
    g128: LineSegment StartX=13.3683 StartY=18.8267 StartZ=0 EndX=13.1844 EndY=18.997 EndZ=0
    g129: LineSegment StartX=13.1844 StartY=18.997 StartZ=0 EndX=13.0175 EndY=19.2047 EndZ=0
    g130: LineSegment StartX=13.0175 StartY=19.2047 StartZ=0 EndX=12.9086 EndY=19.4227 EndZ=0
    g131: LineSegment StartX=12.9086 StartY=19.4227 StartZ=0 EndX=12.694 EndY=19.8518 EndZ=0
    g132: LineSegment StartX=12.694 StartY=19.8518 StartZ=0 EndX=12.5986 EndY=20.1266 EndZ=0
    g133: LineSegment StartX=12.5986 StartY=20.1266 StartZ=0 EndX=12.5373 EndY=20.3616 EndZ=0
    g134: LineSegment StartX=12.5373 StartY=20.3616 StartZ=0 EndX=12.5305 EndY=20.6613 EndZ=0
    g135: LineSegment StartX=12.5305 StartY=20.6613 StartZ=0 EndX=12.527 EndY=20.852 EndZ=0
    g136: LineSegment StartX=12.527 StartY=20.852 StartZ=0 EndX=12.5713 EndY=21.1177 EndZ=0
    g137: LineSegment StartX=12.5713 StartY=21.1177 StartZ=0 EndX=12.6565 EndY=21.5025 EndZ=0
    g138: LineSegment StartX=12.6565 StartY=21.5025 StartZ=0 EndX=12.6531 EndY=21.7205 EndZ=0
    g139: LineSegment StartX=12.6531 StartY=21.7205 StartZ=0 EndX=12.6258 EndY=21.8771 EndZ=0
    g140: LineSegment StartX=12.6258 StartY=21.8771 StartZ=0 EndX=12.5747 EndY=22.0542 EndZ=0
    g141: LineSegment StartX=12.5747 StartY=22.0542 StartZ=0 EndX=12.5027 EndY=22.1813 EndZ=0
    g142: LineSegment StartX=12.5027 StartY=22.1813 StartZ=0 EndX=12.3937 EndY=22.3278 EndZ=0
    g143: LineSegment StartX=12.3937 StartY=22.3278 StartZ=0 EndX=12.278 EndY=22.4299 EndZ=0
    g144: LineSegment StartX=12.278 StartY=22.4299 StartZ=0 EndX=12.1179 EndY=22.5287 EndZ=0
    g145: LineSegment StartX=12.1179 StartY=22.5287 StartZ=0 EndX=11.7535 EndY=22.716 EndZ=0
    g146: LineSegment StartX=11.7535 StartY=22.716 StartZ=0 EndX=11.2792 EndY=22.9552 EndZ=0
    g147: LineSegment StartX=11.2792 StartY=22.9552 StartZ=0 EndX=11.0374 EndY=23.0607 EndZ=0
    g148: LineSegment StartX=11.0374 StartY=23.0607 StartZ=0 EndX=10.8875 EndY=23.1289 EndZ=0
    g149: LineSegment StartX=10.8875 StartY=23.1289 StartZ=0 EndX=10.7036 EndY=23.1527 EndZ=0
    g150: LineSegment StartX=10.7036 StartY=23.1527 StartZ=0 EndX=10.5571 EndY=23.1391 EndZ=0
    g151: LineSegment StartX=10.5571 StartY=23.1391 StartZ=0 EndX=10.38 EndY=23.1084 EndZ=0
    g152: LineSegment StartX=10.38 StartY=23.1084 StartZ=0 EndX=10.2643 EndY=23.0641 EndZ=0
    g153: LineSegment StartX=10.2643 StartY=23.0641 StartZ=0 EndX=10.1042 EndY=22.9892 EndZ=0
    g154: LineSegment StartX=10.1042 StartY=22.9892 StartZ=0 EndX=9.97817 EndY=22.9041 EndZ=0
    g155: LineSegment StartX=9.97817 StartY=22.9041 StartZ=0 EndX=9.8181 EndY=22.727 EndZ=0
    g156: LineSegment StartX=9.8181 StartY=22.727 StartZ=0 EndX=9.68528 EndY=22.5839 EndZ=0
    g157: LineSegment StartX=9.68528 StartY=22.5839 StartZ=0 EndX=9.5184 EndY=22.4068 EndZ=0
    g158: LineSegment StartX=9.5184 StartY=22.4068 StartZ=0 EndX=9.29702 EndY=22.2672 EndZ=0
    g159: LineSegment StartX=9.29702 StartY=22.2672 StartZ=0 EndX=9.09042 EndY=22.1273 EndZ=0
    g160: LineSegment StartX=9.09042 StartY=22.1273 StartZ=0 EndX=8.85883 EndY=22.0183 EndZ=0
    g161: LineSegment StartX=8.85883 StartY=22.0183 StartZ=0 EndX=8.60681 EndY=21.9332 EndZ=0
    g162: LineSegment StartX=8.60681 StartY=21.9332 StartZ=0 EndX=8.36841 EndY=21.8719 EndZ=0
    g163: LineSegment StartX=8.36841 StartY=21.8719 StartZ=0 EndX=8.11979 EndY=21.8344 EndZ=0
    g164: LineSegment StartX=8.11979 StartY=21.8344 StartZ=0 EndX=7.84392 EndY=21.8242 EndZ=0
    g165: LineSegment StartX=7.84392 StartY=21.8242 StartZ=0 EndX=7.61915 EndY=21.8446 EndZ=0
    g166: LineSegment StartX=7.61915 StartY=21.8446 StartZ=0 EndX=7.39096 EndY=21.8753 EndZ=0
    g167: LineSegment StartX=7.39096 StartY=21.8753 StartZ=0 EndX=7.10488 EndY=21.9536 EndZ=0
    g168: LineSegment StartX=7.10488 StartY=21.9536 StartZ=0 EndX=6.8801 EndY=22.0387 EndZ=0
    g169: LineSegment StartX=6.8801 StartY=22.0387 StartZ=0 EndX=6.66554 EndY=22.1613 EndZ=0
    g170: LineSegment StartX=6.66554 StartY=22.1613 StartZ=0 EndX=6.44417 EndY=22.2908 EndZ=0
    g171: LineSegment StartX=6.44417 StartY=22.2908 StartZ=0 EndX=6.19215 EndY=22.5087 EndZ=0
    g172: LineSegment StartX=6.19215 StartY=22.5087 StartZ=0 EndX=6.02186 EndY=22.6688 EndZ=0
    g173: LineSegment StartX=6.02186 StartY=22.6688 StartZ=0 EndX=5.87882 EndY=22.8391 EndZ=0
    g174: LineSegment StartX=5.87882 StartY=22.8391 StartZ=0 EndX=5.74259 EndY=23.0809 EndZ=0
    g175: LineSegment StartX=5.74259 StartY=23.0809 StartZ=0 EndX=5.62679 EndY=23.2989 EndZ=0
    g176: LineSegment StartX=5.62679 StartY=23.2989 StartZ=0 EndX=5.54923 EndY=23.4812 EndZ=0
    g177: LineSegment StartX=5.54923 StartY=23.4812 StartZ=0 EndX=5.48987 EndY=23.7141 EndZ=0
    g178: LineSegment StartX=5.48987 StartY=23.7141 StartZ=0 EndX=5.43965 EndY=23.931 EndZ=0
    g179: LineSegment StartX=5.43965 StartY=23.931 StartZ=0 EndX=5.38283 EndY=24.3702 EndZ=0
    g180: LineSegment StartX=5.38283 StartY=24.3702 StartZ=0 EndX=5.34402 EndY=24.5505 EndZ=0
    g181: LineSegment StartX=5.34402 StartY=24.5505 StartZ=0 EndX=5.26412 EndY=24.7012 EndZ=0
    g182: LineSegment StartX=5.26412 StartY=24.7012 StartZ=0 EndX=5.15662 EndY=24.8433 EndZ=0
    g183: LineSegment StartX=5.15662 StartY=24.8433 StartZ=0 EndX=5.03563 EndY=24.9643 EndZ=0
    g184: LineSegment StartX=5.03563 StartY=24.9643 StartZ=0 EndX=4.9055 EndY=25.0534 EndZ=0
    g185: LineSegment StartX=4.9055 StartY=25.0534 StartZ=0 EndX=4.76168 EndY=25.115 EndZ=0
    g186: LineSegment StartX=4.76168 StartY=25.115 StartZ=0 EndX=4.56991 EndY=25.1698 EndZ=0
    g187: LineSegment StartX=4.56991 StartY=25.1698 StartZ=0 EndX=4.22291 EndY=25.2269 EndZ=0
    g188: LineSegment StartX=4.22291 StartY=25.2269 StartZ=0 EndX=3.72501 EndY=25.306 EndZ=0
    g189: LineSegment StartX=3.72501 StartY=25.306 StartZ=0 EndX=3.40823 EndY=25.3504 EndZ=0
    g190: LineSegment StartX=3.40823 StartY=25.3504 StartZ=0 EndX=3.25674 EndY=25.3565 EndZ=0
    g191: LineSegment StartX=3.25674 StartY=25.3565 StartZ=0 EndX=3.08534 EndY=25.3351 EndZ=0
    g192: LineSegment StartX=3.08534 StartY=25.3351 StartZ=0 EndX=2.91854 EndY=25.2876 EndZ=0
    g193: LineSegment StartX=2.91854 StartY=25.2876 StartZ=0 EndX=2.76092 EndY=25.2111 EndZ=0
    g194: LineSegment StartX=2.76092 StartY=25.2111 StartZ=0 EndX=2.62472 EndY=25.1116 EndZ=0
    g195: LineSegment StartX=2.62472 StartY=25.1116 StartZ=0 EndX=2.50842 EndY=24.9984 EndZ=0
    g196: LineSegment StartX=2.50842 StartY=24.9984 StartZ=0 EndX=2.41174 EndY=24.8483 EndZ=0
    g197: LineSegment StartX=2.41174 StartY=24.8483 StartZ=0 EndX=2.30308 EndY=24.582 EndZ=0
    g198: LineSegment StartX=2.30308 StartY=24.582 StartZ=0 EndX=2.25622 EndY=24.4788 EndZ=0
    g199: LineSegment StartX=2.25622 StartY=24.4788 StartZ=0 EndX=2.13227 EndY=24.2646 EndZ=0
    g200: LineSegment StartX=2.13227 StartY=24.2646 StartZ=0 EndX=1.96394 EndY=24.0365 EndZ=0
    g201: LineSegment StartX=1.96394 StartY=24.0365 StartZ=0 EndX=1.80479 EndY=23.856 EndZ=0
    g202: LineSegment StartX=1.80479 StartY=23.856 StartZ=0 EndX=1.62573 EndY=23.6797 EndZ=0
    g203: LineSegment StartX=1.62573 StartY=23.6797 StartZ=0 EndX=1.41955 EndY=23.5197 EndZ=0
    g204: LineSegment StartX=1.41955 StartY=23.5197 StartZ=0 EndX=1.20904 EndY=23.3867 EndZ=0
    g205: LineSegment StartX=1.20904 StartY=23.3867 StartZ=0 EndX=0.984393 EndY=23.2759 EndZ=0
    g206: LineSegment StartX=0.984393 StartY=23.2759 StartZ=0 EndX=0.742307 EndY=23.1856 EndZ=0
    g207: LineSegment StartX=0.742307 StartY=23.1856 StartZ=0 EndX=0.498622 EndY=23.1238 EndZ=0
    g208: LineSegment StartX=0.498622 StartY=23.1238 StartZ=0 EndX=0.250381 EndY=23.0889 EndZ=0
    g209: LineSegment StartX=0.250381 StartY=23.0889 StartZ=0 EndX=-0.006065 EndY=23.0756 EndZ=0
    g210: LineSegment StartX=-0.006065 StartY=23.0756 StartZ=0 EndX=0 EndY=0 EndZ=0
  constraints (212):
    c: Coincident(g0,g1)
    c: Coincident(g1,g2)
    c: Coincident(g2,g3)
    c: Coincident(g3,g4)
    c: Coincident(g4,g5)
    c: Coincident(g5,g6)
    c: Coincident(g6,g7)
    c: Coincident(g7,g8)
    c: Coincident(g8,g9)
    c: Coincident(g9,g10)
    c: Coincident(g10,g11)
    c: Coincident(g11,g12)
    c: Coincident(g12,g13)
    c: Coincident(g13,g14)
    c: Coincident(g14,g15)
    c: Coincident(g15,g16)
    c: Coincident(g16,g17)
    c: Coincident(g17,g18)
    c: Coincident(g18,g19)
    c: Coincident(g19,g20)
    c: Coincident(g20,g21)
    c: Coincident(g21,g22)
    c: Coincident(g22,g23)
    c: Coincident(g23,g24)
    c: Coincident(g24,g25)
    c: Coincident(g25,g26)
    c: Coincident(g26,g27)
    c: Coincident(g27,g28)
    c: Coincident(g28,g29)
    c: Coincident(g29,g30)
    c: Coincident(g30,g31)
    c: Coincident(g31,g32)
    c: Coincident(g32,g33)
    c: Coincident(g33,g34)
    c: Coincident(g34,g35)
    c: Coincident(g35,g36)
    c: Coincident(g36,g37)
    c: Coincident(g37,g38)
    c: Coincident(g38,g39)
    c: Coincident(g39,g40)
    c: Coincident(g40,g41)
    c: Coincident(g41,g42)
    c: Coincident(g42,g43)
    c: Coincident(g43,g44)
    c: Coincident(g44,g45)
    c: Coincident(g45,g46)
    c: Coincident(g46,g47)
    c: Coincident(g47,g48)
    c: Coincident(g48,g49)
    c: Coincident(g49,g50)
    c: Coincident(g50,g51)
    c: Coincident(g51,g52)
    c: Coincident(g52,g53)
    c: Coincident(g53,g54)
    c: Coincident(g54,g55)
    c: Coincident(g55,g56)
    c: Coincident(g56,g57)
    c: Coincident(g57,g58)
    c: Coincident(g58,g59)
    c: Coincident(g59,g60)
    c: Coincident(g60,g61)
    c: Coincident(g61,g62)
    c: Coincident(g62,g63)
    c: Coincident(g63,g64)
    c: Coincident(g64,g65)
    c: Coincident(g65,g66)
    c: Coincident(g66,g67)
    c: Coincident(g67,g68)
    c: Coincident(g68,g69)
    c: Coincident(g69,g70)
    c: Coincident(g70,g71)
    c: Coincident(g71,g72)
    c: Coincident(g72,g73)
    c: Coincident(g73,g74)
    c: Coincident(g74,g75)
    c: Coincident(g75,g76)
    c: Coincident(g76,g77)
    c: Coincident(g77,g78)
    c: Coincident(g78,g79)
    c: Coincident(g79,g80)
    c: Coincident(g80,g81)
    c: Coincident(g81,g82)
    c: Coincident(g82,g83)
    c: Coincident(g83,g84)
    c: Coincident(g84,g85)
    c: Coincident(g85,g86)
    c: Coincident(g86,g87)
    c: Coincident(g87,g88)
    c: Coincident(g88,g89)
    c: Coincident(g89,g90)
    c: Coincident(g90,g91)
    c: Coincident(g91,g92)
    c: Coincident(g92,g93)
    c: Coincident(g93,g94)
    c: Coincident(g94,g95)
    c: Coincident(g95,g96)
    c: Coincident(g96,g97)
    c: Coincident(g97,g98)
    c: Coincident(g98,g99)
    c: Coincident(g99,g100)
    c: Coincident(g100,g101)
    c: Coincident(g101,g102)
    c: Coincident(g102,g103)
    c: Coincident(g103,g104)
    c: Coincident(g104,g105)
    c: Coincident(g105,g106)
    c: Coincident(g106,g107)
    c: Coincident(g107,g108)
    c: Coincident(g108,g109)
    c: Coincident(g109,g110)
    c: Coincident(g110,g111)
    c: Coincident(g111,g112)
    c: Coincident(g112,g113)
    c: Coincident(g113,g114)
    c: Coincident(g114,g115)
    c: Coincident(g115,g116)
    c: Coincident(g116,g117)
    c: Coincident(g117,g118)
    c: Coincident(g118,g119)
    c: Coincident(g119,g120)
    c: Coincident(g120,g121)
    c: Coincident(g121,g122)
    c: Coincident(g122,g123)
    c: Coincident(g123,g124)
    c: Coincident(g124,g125)
    c: Coincident(g125,g126)
    c: Coincident(g126,g127)
    c: Coincident(g127,g128)
    c: Coincident(g128,g129)
    c: Coincident(g129,g130)
    c: Coincident(g130,g131)
    c: Coincident(g131,g132)
    c: Coincident(g132,g133)
    c: Coincident(g133,g134)
    c: Coincident(g134,g135)
    c: Coincident(g135,g136)
    c: Coincident(g136,g137)
    c: Coincident(g137,g138)
    c: Coincident(g138,g139)
    c: Coincident(g139,g140)
    c: Coincident(g140,g141)
    c: Coincident(g141,g142)
    c: Coincident(g142,g143)
    c: Coincident(g143,g144)
    c: Coincident(g144,g145)
    c: Coincident(g145,g146)
    c: Coincident(g146,g147)
    c: Coincident(g147,g148)
    c: Coincident(g148,g149)
    c: Coincident(g149,g150)
    c: Coincident(g150,g151)
    c: Coincident(g151,g152)
    c: Coincident(g152,g153)
    c: Coincident(g153,g154)
    c: Coincident(g154,g155)
    c: Coincident(g155,g156)
    c: Coincident(g156,g157)
    c: Coincident(g157,g158)
    c: Coincident(g158,g159)
    c: Coincident(g159,g160)
    c: Coincident(g160,g161)
    c: Coincident(g161,g162)
    c: Coincident(g162,g163)
    c: Coincident(g163,g164)
    c: Coincident(g164,g165)
    c: Coincident(g165,g166)
    c: Coincident(g166,g167)
    c: Coincident(g167,g168)
    c: Coincident(g168,g169)
    c: Coincident(g169,g170)
    c: Coincident(g170,g171)
    c: Coincident(g171,g172)
    c: Coincident(g172,g173)
    c: Coincident(g173,g174)
    c: Coincident(g174,g175)
    c: Coincident(g175,g176)
    c: Coincident(g176,g177)
    c: Coincident(g177,g178)
    c: Coincident(g178,g179)
    c: Coincident(g179,g180)
    c: Coincident(g180,g181)
    c: Coincident(g181,g182)
    c: Coincident(g182,g183)
    c: Coincident(g183,g184)
    c: Coincident(g184,g185)
    c: Coincident(g185,g186)
    c: Coincident(g186,g187)
    c: Coincident(g187,g188)
    c: Coincident(g188,g189)
    c: Coincident(g189,g190)
    c: Coincident(g190,g191)
    c: Coincident(g191,g192)
    c: Coincident(g192,g193)
    c: Coincident(g193,g194)
    c: Coincident(g194,g195)
    c: Coincident(g195,g196)
    c: Coincident(g196,g197)
    c: Coincident(g197,g198)
    c: Coincident(g198,g199)
    c: Coincident(g199,g200)
    c: Coincident(g200,g201)
    c: Coincident(g201,g202)
    c: Coincident(g202,g203)
    c: Coincident(g203,g204)
    c: Coincident(g204,g205)
    c: Coincident(g205,g206)
    c: Coincident(g206,g207)
    c: Coincident(g207,g208)
    c: Coincident(g208,g209)
    c: Coincident(g0,g210)
    c: Coincident(g0,g-1)
    c: Coincident(g209,g210)
FEATURE [PartDesign::Pad] Pad021
  Length = 2.5
  Length2 = 100
  Placement = pos=(0,0,0) rot=(0.57735,0.57735,0.57735;2.0944rad)
  Profile = -> Sketch040
  Type = 0
FEATURE [PartDesign::PolarPattern] PolarPattern018
  Angle = 360
  Axis = -> Sketch040 [N_Axis]
  BaseFeature = -> Pad021
  Occurrences = 4
  Originals = -> [Pad021]
  Placement = pos=(0,0,0) rot=(0.57735,0.57735,0.57735;2.0944rad)
FEATURE [Sketcher::SketchObject] Sketch034
  MapMode = 5
  Placement = pos=(0,0,0) rot=(0.57735,0.57735,-0.57735;4.18879rad)
  Support = -> [PolarPattern018]
FEATURE [PartDesign::Pocket] Pocket003
  BaseFeature = -> PolarPattern018
  Length = 1
  Length2 = 100
  Placement = pos=(0,0,0) rot=(0.57735,0.57735,0.57735;2.0944rad)
  Profile = -> Sketch037
  Reversed = true
  Type = 1
FEATURE [PartDesign::PolarPattern] PolarPattern017
  Angle = 360
  Axis = -> Sketch037 [N_Axis]
  BaseFeature = -> Pocket003
  Occurrences = 2
  Originals = -> [Pocket003]
  Placement = pos=(0,0,0) rot=(0.57735,0.57735,0.57735;2.0944rad)
FEATURE [Sketcher::SketchObject] Sketch041
  MapMode = 5
  Placement = pos=(0,0,0) rot=(0.57735,0.57735,-0.57735;4.18879rad)
  Support = -> [PolarPattern017]
  sketch-geometry (2):
    g0: Circle CenterX=0 CenterY=0 CenterZ=0 NormalX=0 NormalY=0 NormalZ=1 AngleXU=0 Radius=20.57
    g1: Circle CenterX=0 CenterY=0 CenterZ=0 NormalX=0 NormalY=0 NormalZ=1 AngleXU=0 Radius=2.75498
  constraints (3):
    c: Coincident(g1,g0)
    c: Coincident(g-1,g0)
    c: Radius(g0) = 20.57
FEATURE [PartDesign::Pad] Pad025
  BaseFeature = -> PolarPattern017
  Length = 5.5
  Length2 = 100
  Placement = pos=(0,0,0) rot=(0.57735,0.57735,0.57735;2.0944rad)
  Profile = -> Sketch041
  Type = 0
FEATURE [Sketcher::SketchObject] Sketch042
  MapMode = 5
  Placement = pos=(-5.5,3.7e-15,-3.7e-15) rot=(0.57735,0.57735,-0.57735;4.18879rad)
  Support = -> [Pad025]
  sketch-geometry (2):
    g0: Circle CenterX=0 CenterY=0 CenterZ=0 NormalX=0 NormalY=0 NormalZ=1 AngleXU=0 Radius=2.77794
    g1: Circle CenterX=0 CenterY=0 CenterZ=0 NormalX=0 NormalY=0 NormalZ=1 AngleXU=0 Radius=17
  constraints (3):
    c: Coincident(g0,g1)
    c: Coincident(g0,g-1)
    c: Radius(g1) = 17
FEATURE [PartDesign::Body] Body013
  Group = -> [Sketch037,Sketch040,Pad021,PolarPattern018,Sketch034,Pocket003,PolarPattern017,Sketch041,Pad025,Sketch042]
  Origin = -> Origin013
  Placement = pos=(-26,0,0) rot=(1,0,0;0.174533rad)
  Tip = -> Pad025
FEATURE [PartDesign::Pad] Pad026
  BaseFeature = -> Pad023
  Length = 12.5
  Length2 = 100
  Placement = pos=(0,0,0) rot=(0.57735,0.57735,0.57735;2.0944rad)
  Profile = -> Sketch039
  Type = 0
FEATURE [Sketcher::SketchObject] Sketch043
  MapMode = 5
  Placement = pos=(-18,1.6e-14,-1.57e-14) rot=(-0.57735,-0.57735,0.57735;2.0944rad)
  Support = -> [Pad026]
  sketch-geometry (2):
    g0: Circle CenterX=0 CenterY=0 CenterZ=0 NormalX=0 NormalY=0 NormalZ=1 AngleXU=0 Radius=2.74985
    g1: Circle CenterX=0 CenterY=0 CenterZ=0 NormalX=0 NormalY=0 NormalZ=1 AngleXU=0 Radius=22.5957
  constraints (2):
    c: Coincident(g0,g1)
    c: Coincident(g0,g-1)
FEATURE [PartDesign::Pad] Pad024
  BaseFeature = -> Pad026
  Length = 5.5
  Length2 = 100
  Placement = pos=(0,0,0) rot=(0.57735,0.57735,0.57735;2.0944rad)
  Profile = -> Sketch043
  Type = 0
FEATURE [PartDesign::Body] Body014
  Group = -> [Sketch033,Sketch035,Pad022,PolarPattern015,Sketch036,Pocket002,PolarPattern016,Sketch038,Pad023,Sketch039,Pad026,Sketch043,Pad024]
  Origin = -> Origin014
  Placement = pos=(0,0,0) rot=(1,0,0;0.174533rad)
  Tip = -> Pad024
FEATURE [Part::MultiFuse] Fusion004
  Placement = pos=(-68.5,0,0) rot=(0,-0.173648,0.984808;3.14159rad)
  Shapes = -> [Body013,Body014]
FEATURE [Mesh::Feature] Trak_WALL_E001  label="Trak_WALL-E001"
  Placement = pos=(-29.25,-3,26.6) rot=(0,1,0;1.5708rad)
FEATURE [Part::Cylinder] Cylinder006  label="Цилиндр006"
  Angle = 360
  AttacherType = Attacher::AttachEngine3D
  Height = 6
  Placement = pos=(-31,0,0) rot=(0,-1,0;1.5708rad)
  Radius = 20
FEATURE [Part::Cylinder] Cylinder007  label="Цилиндр007"
  Angle = 360
  AttacherType = Attacher::AttachEngine3D
  Height = 6
  Placement = pos=(-37,0,0) rot=(0,1,0;1.5708rad)
  Radius = 3
FEATURE [Part::Cut] Cut009
  Base = -> Cylinder006
  Tool = -> Cylinder007
FEATURE [Part::MultiFuse] Fusion005
  Shapes = -> [Fusion003,Cut009,Fusion004]
